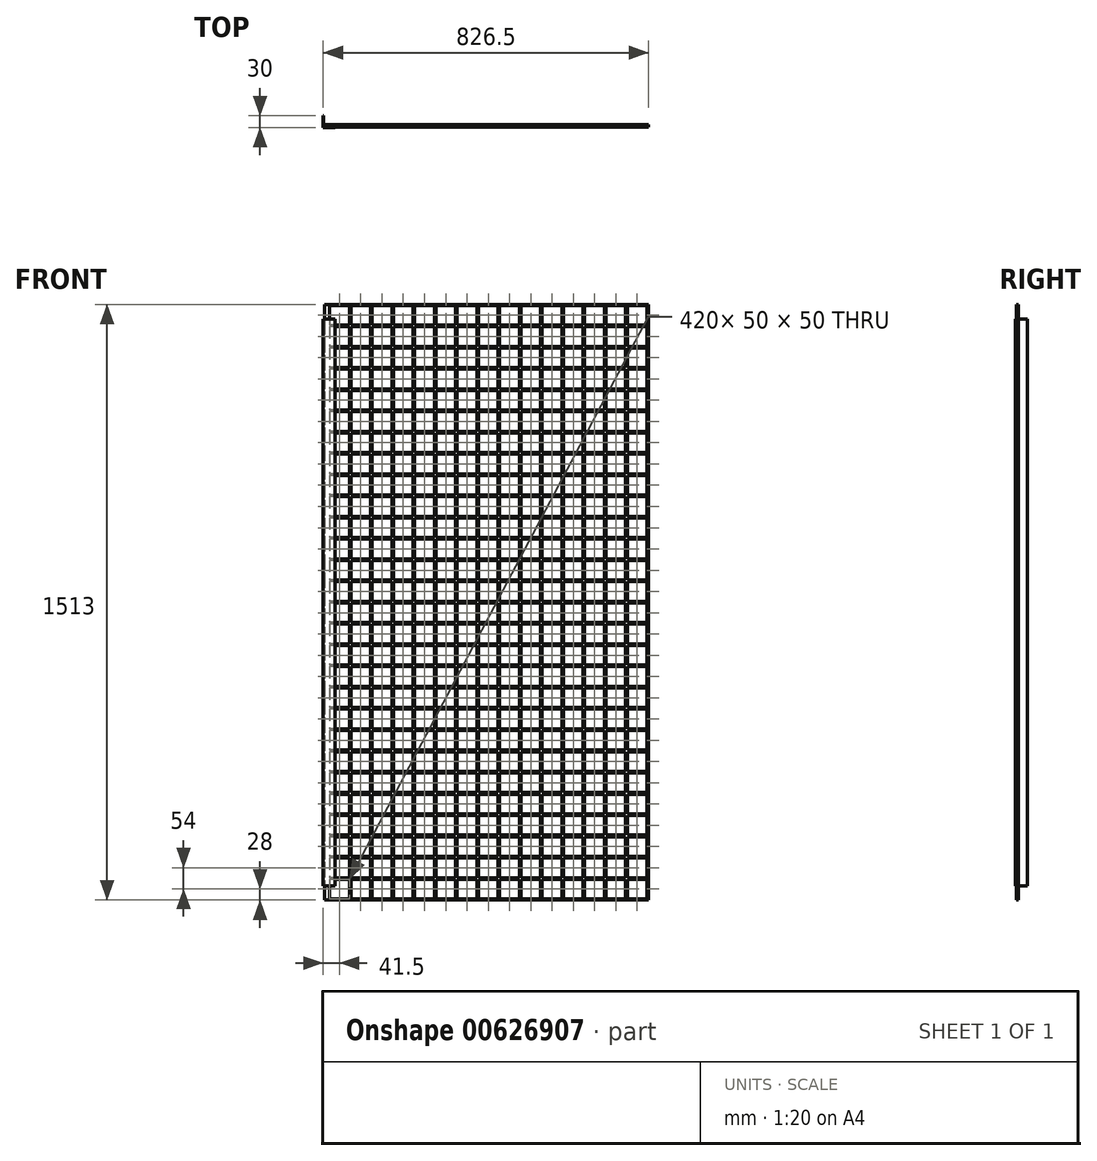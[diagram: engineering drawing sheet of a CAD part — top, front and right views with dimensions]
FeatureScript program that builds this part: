
annotation { "Feature Type Name" : "Feature", "Feature Type Description" : "" }
export const myFeature = defineFeature(function(context is Context, id is Id, definition is map)
    precondition{}
    {
        {
            var Q0;
            Q0=qCreatedBy(makeId("Front.planeOp"),FACE);
            var sketch = newSketch(context, id + "F0", { "sketchPlane" : qUnion([Q0])});
            skLineSegment(sketch, "E0.bottom", {"start": v(0, 0) * mm, "end": v(830, 0) * mm});
            skLineSegment(sketch, "E0.top", {"start": v(0, 1520) * mm, "end": v(830, 1520) * mm});
            skLineSegment(sketch, "E0.left", {"start": v(0, 0) * mm, "end": v(0, 1520) * mm});
            skLineSegment(sketch, "E0.right", {"start": v(830, 0) * mm, "end": v(830, 1520) * mm});
            skLineSegment(sketch, "E1.bottom", {"start": v(830, 1520) * mm, "end": v(800, 1520) * mm});
            skLineSegment(sketch, "E1.top", {"start": v(830, 0) * mm, "end": v(800, 0) * mm});
            skLineSegment(sketch, "E1.left", {"start": v(830, 1520) * mm, "end": v(830, 0) * mm});
            skLineSegment(sketch, "E1.right", {"start": v(800, 1520) * mm, "end": v(800, 0) * mm});
            skLineSegment(sketch, "E2.bottom", {"start": v(0, 1520) * mm, "end": v(800, 1520) * mm});
            skLineSegment(sketch, "E2.top", {"start": v(0, 1490) * mm, "end": v(800, 1490) * mm});
            skLineSegment(sketch, "E2.left", {"start": v(0, 1520) * mm, "end": v(0, 1490) * mm});
            skLineSegment(sketch, "E2.right", {"start": v(800, 1520) * mm, "end": v(800, 1490) * mm});
            skLineSegment(sketch, "E3.bottom", {"start": v(800, 0) * mm, "end": v(0, 0) * mm});
            skLineSegment(sketch, "E3.top", {"start": v(800, 30) * mm, "end": v(0, 30) * mm});
            skLineSegment(sketch, "E3.left", {"start": v(800, 0) * mm, "end": v(800, 30) * mm});
            skLineSegment(sketch, "E3.right", {"start": v(0, 0) * mm, "end": v(0, 30) * mm});
            skLineSegment(sketch, "E4.bottom", {"start": v(0, 1480) * mm, "end": v(30, 1480) * mm});
            skLineSegment(sketch, "E4.top", {"start": v(0, 40) * mm, "end": v(30, 40) * mm});
            skLineSegment(sketch, "E4.left", {"start": v(0, 1480) * mm, "end": v(0, 40) * mm});
            skLineSegment(sketch, "E4.right", {"start": v(30, 1480) * mm, "end": v(30, 40) * mm});
            skSolve(sketch);
        }
        {
            var Q0;
            Q0=makeQuery(id+"F0.imprint","IMPRINT",FACE,{"disambiguationData":[TD([[makeQuery(id+"F0.imprint","IMPRINT",EDGE,{"derivedFrom":sQuery(id+"F0.wireOp",EDGE,"E2.bottom")}),-1.0]])]});
            var Q1;
            Q1=makeQuery(id+"F0.imprint","IMPRINT",FACE,{"disambiguationData":[TD([[makeQuery(id+"F0.imprint","IMPRINT",EDGE,{"derivedFrom":sQuery(id+"F0.wireOp",EDGE,"E1.bottom")}),1.0]])]});
            var Q2;
            Q2=makeQuery(id+"F0.imprint","IMPRINT",FACE,{"disambiguationData":[TD([[makeQuery(id+"F0.imprint","IMPRINT",EDGE,{"derivedFrom":sQuery(id+"F0.wireOp",EDGE,"E3.bottom")}),-1.0]])]});
            var Q3;
            Q3=makeQuery(id+"F0.imprint","IMPRINT",FACE,{"disambiguationData":[TD([[makeQuery(id+"F0.imprint","IMPRINT",EDGE,{"derivedFrom":sQuery(id+"F0.wireOp",EDGE,"E4.bottom")}),-1.0]])]});
            extrude(context, id + "F1", {"entities" : qUnion([Q0, Q1, Q2, Q3]), "depth" : 30 * mm, "offsetDistance" : 25 * mm});
        }
        {
            var Q0;
            Q0=makeQuery(id+"F1.opExtrude","SWEPT_FACE",FACE,{"disambiguationData":[OSD([sQuery(id+"F0.wireOp",EDGE,"E2.top")])]});
            var Q1;
            Q1=makeQuery(id+"F1.opExtrude","SWEPT_FACE",FACE,{"disambiguationData":[OSD([sQuery(id+"F0.wireOp",EDGE,"E1.right")])]});
            var Q2;
            Q2=makeQuery(id+"F1.opExtrude","SWEPT_FACE",FACE,{"disambiguationData":[OSD([sQuery(id+"F0.wireOp",EDGE,"E3.top")])]});
            var Q3;
            Q3=makeQuery(id+"F1.opExtrude","SWEPT_FACE",FACE,{"disambiguationData":[OSD([sQuery(id+"F0.wireOp",EDGE,"E2.left")])]});
            var Q4;
            Q4=makeQuery(id+"F1.opExtrude","SWEPT_FACE",FACE,{"disambiguationData":[OSD([sQuery(id+"F0.wireOp",EDGE,"E3.right")])]});
            var Q5;
            Q5=makeQuery(id+"F1.opExtrude","SWEPT_FACE",FACE,{"disambiguationData":[OSD([sQuery(id+"F0.wireOp",EDGE,"E4.right")])]});
            var Q6;
            Q6=makeQuery(id+"F1.opExtrude","SWEPT_FACE",FACE,{"disambiguationData":[OSD([sQuery(id+"F0.wireOp",EDGE,"E4.bottom")])]});
            var Q7;
            Q7=makeQuery(id+"F1.opExtrude","SWEPT_FACE",FACE,{"disambiguationData":[OSD([sQuery(id+"F0.wireOp",EDGE,"E4.top")])]});
            var Q8;
            Q8=makeQuery(id+"F1.opExtrude","CAP_FACE",FACE,{"disambiguationData":[OSD([sQuery(id+"F0.wireOp",EDGE,"E4.bottom"),sQuery(id+"F0.wireOp",EDGE,"E4.top"),sQuery(id+"F0.wireOp",EDGE,"E4.left"),sQuery(id+"F0.wireOp",EDGE,"E4.right")])],"isStart":true});
            shell(context, id + "F2", {"entities" : qUnion([Q0, Q1, Q2, Q3, Q4, Q5, Q6, Q7, Q8]), "thickness" : 1.5 * mm});
        }
        {
            var Q0;
            Q0=makeQuery(id+"F2.opShell","OFFSET_FACE",FACE,{"disambiguationData":[OSD([sQuery(id+"F0.wireOp",EDGE,"E4.bottom"),sQuery(id+"F0.wireOp",EDGE,"E4.top"),sQuery(id+"F0.wireOp",EDGE,"E4.left"),sQuery(id+"F0.wireOp",EDGE,"E4.right")])]});
            var sketch = newSketch(context, id + "F3", { "sketchPlane" : qUnion([Q0])});
            skLineSegment(sketch, "E5.bottom", {"start": v(-3.5, 1516.5) * mm, "end": v(-826.5, 1516.5) * mm});
            skLineSegment(sketch, "E5.top", {"start": v(-3.5, 3.5) * mm, "end": v(-826.5, 3.5) * mm});
            skLineSegment(sketch, "E5.left", {"start": v(-3.5, 1516.5) * mm, "end": v(-3.5, 3.5) * mm});
            skLineSegment(sketch, "E5.right", {"start": v(-826.5, 1516.5) * mm, "end": v(-826.5, 3.5) * mm});
            skLineSegment(sketch, "E6.bottom", {"start": v(-822.5, 1514.5) * mm, "end": v(-772.5, 1514.5) * mm});
            skLineSegment(sketch, "E6.top", {"start": v(-822.5, 1464.5) * mm, "end": v(-772.5, 1464.5) * mm});
            skLineSegment(sketch, "E6.left", {"start": v(-822.5, 1514.5) * mm, "end": v(-822.5, 1464.5) * mm});
            skLineSegment(sketch, "E6.right", {"start": v(-772.5, 1514.5) * mm, "end": v(-772.5, 1464.5) * mm});
            skLineSegment(sketch, "E7.0.1.0", {"start": v(-772.5, 1460.5) * mm, "end": v(-772.5, 1410.5) * mm});
            skLineSegment(sketch, "E7.0.1.1", {"start": v(-822.5, 1460.5) * mm, "end": v(-772.5, 1460.5) * mm});
            skLineSegment(sketch, "E7.0.1.2", {"start": v(-822.5, 1460.5) * mm, "end": v(-822.5, 1410.5) * mm});
            skLineSegment(sketch, "E7.0.1.3", {"start": v(-822.5, 1410.5) * mm, "end": v(-772.5, 1410.5) * mm});
            skLineSegment(sketch, "E7.0.2.0", {"start": v(-772.5, 1406.5) * mm, "end": v(-772.5, 1356.5) * mm});
            skLineSegment(sketch, "E7.0.2.1", {"start": v(-822.5, 1406.5) * mm, "end": v(-772.5, 1406.5) * mm});
            skLineSegment(sketch, "E7.0.2.2", {"start": v(-822.5, 1406.5) * mm, "end": v(-822.5, 1356.5) * mm});
            skLineSegment(sketch, "E7.0.2.3", {"start": v(-822.5, 1356.5) * mm, "end": v(-772.5, 1356.5) * mm});
            skLineSegment(sketch, "E7.0.3.0", {"start": v(-772.5, 1352.5) * mm, "end": v(-772.5, 1302.5) * mm});
            skLineSegment(sketch, "E7.0.3.1", {"start": v(-822.5, 1352.5) * mm, "end": v(-772.5, 1352.5) * mm});
            skLineSegment(sketch, "E7.0.3.2", {"start": v(-822.5, 1352.5) * mm, "end": v(-822.5, 1302.5) * mm});
            skLineSegment(sketch, "E7.0.3.3", {"start": v(-822.5, 1302.5) * mm, "end": v(-772.5, 1302.5) * mm});
            skLineSegment(sketch, "E7.0.4.0", {"start": v(-772.5, 1298.5) * mm, "end": v(-772.5, 1248.5) * mm});
            skLineSegment(sketch, "E7.0.4.1", {"start": v(-822.5, 1298.5) * mm, "end": v(-772.5, 1298.5) * mm});
            skLineSegment(sketch, "E7.0.4.2", {"start": v(-822.5, 1298.5) * mm, "end": v(-822.5, 1248.5) * mm});
            skLineSegment(sketch, "E7.0.4.3", {"start": v(-822.5, 1248.5) * mm, "end": v(-772.5, 1248.5) * mm});
            skLineSegment(sketch, "E7.0.5.0", {"start": v(-772.5, 1244.5) * mm, "end": v(-772.5, 1194.5) * mm});
            skLineSegment(sketch, "E7.0.5.1", {"start": v(-822.5, 1244.5) * mm, "end": v(-772.5, 1244.5) * mm});
            skLineSegment(sketch, "E7.0.5.2", {"start": v(-822.5, 1244.5) * mm, "end": v(-822.5, 1194.5) * mm});
            skLineSegment(sketch, "E7.0.5.3", {"start": v(-822.5, 1194.5) * mm, "end": v(-772.5, 1194.5) * mm});
            skLineSegment(sketch, "E7.0.6.0", {"start": v(-772.5, 1190.5) * mm, "end": v(-772.5, 1140.5) * mm});
            skLineSegment(sketch, "E7.0.6.1", {"start": v(-822.5, 1190.5) * mm, "end": v(-772.5, 1190.5) * mm});
            skLineSegment(sketch, "E7.0.6.2", {"start": v(-822.5, 1190.5) * mm, "end": v(-822.5, 1140.5) * mm});
            skLineSegment(sketch, "E7.0.6.3", {"start": v(-822.5, 1140.5) * mm, "end": v(-772.5, 1140.5) * mm});
            skLineSegment(sketch, "E7.0.7.0", {"start": v(-772.5, 1136.5) * mm, "end": v(-772.5, 1086.5) * mm});
            skLineSegment(sketch, "E7.0.7.1", {"start": v(-822.5, 1136.5) * mm, "end": v(-772.5, 1136.5) * mm});
            skLineSegment(sketch, "E7.0.7.2", {"start": v(-822.5, 1136.5) * mm, "end": v(-822.5, 1086.5) * mm});
            skLineSegment(sketch, "E7.0.7.3", {"start": v(-822.5, 1086.5) * mm, "end": v(-772.5, 1086.5) * mm});
            skLineSegment(sketch, "E7.0.8.0", {"start": v(-772.5, 1082.5) * mm, "end": v(-772.5, 1032.5) * mm});
            skLineSegment(sketch, "E7.0.8.1", {"start": v(-822.5, 1082.5) * mm, "end": v(-772.5, 1082.5) * mm});
            skLineSegment(sketch, "E7.0.8.2", {"start": v(-822.5, 1082.5) * mm, "end": v(-822.5, 1032.5) * mm});
            skLineSegment(sketch, "E7.0.8.3", {"start": v(-822.5, 1032.5) * mm, "end": v(-772.5, 1032.5) * mm});
            skLineSegment(sketch, "E7.0.9.0", {"start": v(-772.5, 1028.5) * mm, "end": v(-772.5, 978.5) * mm});
            skLineSegment(sketch, "E7.0.9.1", {"start": v(-822.5, 1028.5) * mm, "end": v(-772.5, 1028.5) * mm});
            skLineSegment(sketch, "E7.0.9.2", {"start": v(-822.5, 1028.5) * mm, "end": v(-822.5, 978.5) * mm});
            skLineSegment(sketch, "E7.0.9.3", {"start": v(-822.5, 978.5) * mm, "end": v(-772.5, 978.5) * mm});
            skLineSegment(sketch, "E7.0.10.0", {"start": v(-772.5, 974.5) * mm, "end": v(-772.5, 924.5) * mm});
            skLineSegment(sketch, "E7.0.10.1", {"start": v(-822.5, 974.5) * mm, "end": v(-772.5, 974.5) * mm});
            skLineSegment(sketch, "E7.0.10.2", {"start": v(-822.5, 974.5) * mm, "end": v(-822.5, 924.5) * mm});
            skLineSegment(sketch, "E7.0.10.3", {"start": v(-822.5, 924.5) * mm, "end": v(-772.5, 924.5) * mm});
            skLineSegment(sketch, "E7.0.11.0", {"start": v(-772.5, 920.5) * mm, "end": v(-772.5, 870.5) * mm});
            skLineSegment(sketch, "E7.0.11.1", {"start": v(-822.5, 920.5) * mm, "end": v(-772.5, 920.5) * mm});
            skLineSegment(sketch, "E7.0.11.2", {"start": v(-822.5, 920.5) * mm, "end": v(-822.5, 870.5) * mm});
            skLineSegment(sketch, "E7.0.11.3", {"start": v(-822.5, 870.5) * mm, "end": v(-772.5, 870.5) * mm});
            skLineSegment(sketch, "E7.0.12.0", {"start": v(-772.5, 866.5) * mm, "end": v(-772.5, 816.5) * mm});
            skLineSegment(sketch, "E7.0.12.1", {"start": v(-822.5, 866.5) * mm, "end": v(-772.5, 866.5) * mm});
            skLineSegment(sketch, "E7.0.12.2", {"start": v(-822.5, 866.5) * mm, "end": v(-822.5, 816.5) * mm});
            skLineSegment(sketch, "E7.0.12.3", {"start": v(-822.5, 816.5) * mm, "end": v(-772.5, 816.5) * mm});
            skLineSegment(sketch, "E7.0.13.0", {"start": v(-772.5, 812.5) * mm, "end": v(-772.5, 762.5) * mm});
            skLineSegment(sketch, "E7.0.13.1", {"start": v(-822.5, 812.5) * mm, "end": v(-772.5, 812.5) * mm});
            skLineSegment(sketch, "E7.0.13.2", {"start": v(-822.5, 812.5) * mm, "end": v(-822.5, 762.5) * mm});
            skLineSegment(sketch, "E7.0.13.3", {"start": v(-822.5, 762.5) * mm, "end": v(-772.5, 762.5) * mm});
            skLineSegment(sketch, "E7.0.14.0", {"start": v(-772.5, 758.5) * mm, "end": v(-772.5, 708.5) * mm});
            skLineSegment(sketch, "E7.0.14.1", {"start": v(-822.5, 758.5) * mm, "end": v(-772.5, 758.5) * mm});
            skLineSegment(sketch, "E7.0.14.2", {"start": v(-822.5, 758.5) * mm, "end": v(-822.5, 708.5) * mm});
            skLineSegment(sketch, "E7.0.14.3", {"start": v(-822.5, 708.5) * mm, "end": v(-772.5, 708.5) * mm});
            skLineSegment(sketch, "E7.0.15.0", {"start": v(-772.5, 704.5) * mm, "end": v(-772.5, 654.5) * mm});
            skLineSegment(sketch, "E7.0.15.1", {"start": v(-822.5, 704.5) * mm, "end": v(-772.5, 704.5) * mm});
            skLineSegment(sketch, "E7.0.15.2", {"start": v(-822.5, 704.5) * mm, "end": v(-822.5, 654.5) * mm});
            skLineSegment(sketch, "E7.0.15.3", {"start": v(-822.5, 654.5) * mm, "end": v(-772.5, 654.5) * mm});
            skLineSegment(sketch, "E7.0.16.0", {"start": v(-772.5, 650.5) * mm, "end": v(-772.5, 600.5) * mm});
            skLineSegment(sketch, "E7.0.16.1", {"start": v(-822.5, 650.5) * mm, "end": v(-772.5, 650.5) * mm});
            skLineSegment(sketch, "E7.0.16.2", {"start": v(-822.5, 650.5) * mm, "end": v(-822.5, 600.5) * mm});
            skLineSegment(sketch, "E7.0.16.3", {"start": v(-822.5, 600.5) * mm, "end": v(-772.5, 600.5) * mm});
            skLineSegment(sketch, "E7.0.17.0", {"start": v(-772.5, 596.5) * mm, "end": v(-772.5, 546.5) * mm});
            skLineSegment(sketch, "E7.0.17.1", {"start": v(-822.5, 596.5) * mm, "end": v(-772.5, 596.5) * mm});
            skLineSegment(sketch, "E7.0.17.2", {"start": v(-822.5, 596.5) * mm, "end": v(-822.5, 546.5) * mm});
            skLineSegment(sketch, "E7.0.17.3", {"start": v(-822.5, 546.5) * mm, "end": v(-772.5, 546.5) * mm});
            skLineSegment(sketch, "E7.0.18.0", {"start": v(-772.5, 542.5) * mm, "end": v(-772.5, 492.5) * mm});
            skLineSegment(sketch, "E7.0.18.1", {"start": v(-822.5, 542.5) * mm, "end": v(-772.5, 542.5) * mm});
            skLineSegment(sketch, "E7.0.18.2", {"start": v(-822.5, 542.5) * mm, "end": v(-822.5, 492.5) * mm});
            skLineSegment(sketch, "E7.0.18.3", {"start": v(-822.5, 492.5) * mm, "end": v(-772.5, 492.5) * mm});
            skLineSegment(sketch, "E7.0.19.0", {"start": v(-772.5, 488.5) * mm, "end": v(-772.5, 438.5) * mm});
            skLineSegment(sketch, "E7.0.19.1", {"start": v(-822.5, 488.5) * mm, "end": v(-772.5, 488.5) * mm});
            skLineSegment(sketch, "E7.0.19.2", {"start": v(-822.5, 488.5) * mm, "end": v(-822.5, 438.5) * mm});
            skLineSegment(sketch, "E7.0.19.3", {"start": v(-822.5, 438.5) * mm, "end": v(-772.5, 438.5) * mm});
            skLineSegment(sketch, "E7.0.20.0", {"start": v(-772.5, 434.5) * mm, "end": v(-772.5, 384.5) * mm});
            skLineSegment(sketch, "E7.0.20.1", {"start": v(-822.5, 434.5) * mm, "end": v(-772.5, 434.5) * mm});
            skLineSegment(sketch, "E7.0.20.2", {"start": v(-822.5, 434.5) * mm, "end": v(-822.5, 384.5) * mm});
            skLineSegment(sketch, "E7.0.20.3", {"start": v(-822.5, 384.5) * mm, "end": v(-772.5, 384.5) * mm});
            skLineSegment(sketch, "E7.0.21.0", {"start": v(-772.5, 380.5) * mm, "end": v(-772.5, 330.5) * mm});
            skLineSegment(sketch, "E7.0.21.1", {"start": v(-822.5, 380.5) * mm, "end": v(-772.5, 380.5) * mm});
            skLineSegment(sketch, "E7.0.21.2", {"start": v(-822.5, 380.5) * mm, "end": v(-822.5, 330.5) * mm});
            skLineSegment(sketch, "E7.0.21.3", {"start": v(-822.5, 330.5) * mm, "end": v(-772.5, 330.5) * mm});
            skLineSegment(sketch, "E7.0.22.0", {"start": v(-772.5, 326.5) * mm, "end": v(-772.5, 276.5) * mm});
            skLineSegment(sketch, "E7.0.22.1", {"start": v(-822.5, 326.5) * mm, "end": v(-772.5, 326.5) * mm});
            skLineSegment(sketch, "E7.0.22.2", {"start": v(-822.5, 326.5) * mm, "end": v(-822.5, 276.5) * mm});
            skLineSegment(sketch, "E7.0.22.3", {"start": v(-822.5, 276.5) * mm, "end": v(-772.5, 276.5) * mm});
            skLineSegment(sketch, "E7.0.23.0", {"start": v(-772.5, 272.5) * mm, "end": v(-772.5, 222.5) * mm});
            skLineSegment(sketch, "E7.0.23.1", {"start": v(-822.5, 272.5) * mm, "end": v(-772.5, 272.5) * mm});
            skLineSegment(sketch, "E7.0.23.2", {"start": v(-822.5, 272.5) * mm, "end": v(-822.5, 222.5) * mm});
            skLineSegment(sketch, "E7.0.23.3", {"start": v(-822.5, 222.5) * mm, "end": v(-772.5, 222.5) * mm});
            skLineSegment(sketch, "E7.0.24.0", {"start": v(-772.5, 218.5) * mm, "end": v(-772.5, 168.5) * mm});
            skLineSegment(sketch, "E7.0.24.1", {"start": v(-822.5, 218.5) * mm, "end": v(-772.5, 218.5) * mm});
            skLineSegment(sketch, "E7.0.24.2", {"start": v(-822.5, 218.5) * mm, "end": v(-822.5, 168.5) * mm});
            skLineSegment(sketch, "E7.0.24.3", {"start": v(-822.5, 168.5) * mm, "end": v(-772.5, 168.5) * mm});
            skLineSegment(sketch, "E7.0.25.0", {"start": v(-772.5, 164.5) * mm, "end": v(-772.5, 114.5) * mm});
            skLineSegment(sketch, "E7.0.25.1", {"start": v(-822.5, 164.5) * mm, "end": v(-772.5, 164.5) * mm});
            skLineSegment(sketch, "E7.0.25.2", {"start": v(-822.5, 164.5) * mm, "end": v(-822.5, 114.5) * mm});
            skLineSegment(sketch, "E7.0.25.3", {"start": v(-822.5, 114.5) * mm, "end": v(-772.5, 114.5) * mm});
            skLineSegment(sketch, "E7.0.26.0", {"start": v(-772.5, 110.5) * mm, "end": v(-772.5, 60.5) * mm});
            skLineSegment(sketch, "E7.0.26.1", {"start": v(-822.5, 110.5) * mm, "end": v(-772.5, 110.5) * mm});
            skLineSegment(sketch, "E7.0.26.2", {"start": v(-822.5, 110.5) * mm, "end": v(-822.5, 60.5) * mm});
            skLineSegment(sketch, "E7.0.26.3", {"start": v(-822.5, 60.5) * mm, "end": v(-772.5, 60.5) * mm});
            skLineSegment(sketch, "E7.0.27.0", {"start": v(-772.5, 56.5) * mm, "end": v(-772.5, 6.5) * mm});
            skLineSegment(sketch, "E7.0.27.1", {"start": v(-822.5, 56.5) * mm, "end": v(-772.5, 56.5) * mm});
            skLineSegment(sketch, "E7.0.27.2", {"start": v(-822.5, 56.5) * mm, "end": v(-822.5, 6.5) * mm});
            skLineSegment(sketch, "E7.0.27.3", {"start": v(-822.5, 6.5) * mm, "end": v(-772.5, 6.5) * mm});
            skLineSegment(sketch, "E7.1.0.0", {"start": v(-718.5, 1514.5) * mm, "end": v(-718.5, 1464.5) * mm});
            skLineSegment(sketch, "E7.1.0.1", {"start": v(-768.5, 1514.5) * mm, "end": v(-718.5, 1514.5) * mm});
            skLineSegment(sketch, "E7.1.0.2", {"start": v(-768.5, 1514.5) * mm, "end": v(-768.5, 1464.5) * mm});
            skLineSegment(sketch, "E7.1.0.3", {"start": v(-768.5, 1464.5) * mm, "end": v(-718.5, 1464.5) * mm});
            skLineSegment(sketch, "E7.1.1.0", {"start": v(-718.5, 1460.5) * mm, "end": v(-718.5, 1410.5) * mm});
            skLineSegment(sketch, "E7.1.1.1", {"start": v(-768.5, 1460.5) * mm, "end": v(-718.5, 1460.5) * mm});
            skLineSegment(sketch, "E7.1.1.2", {"start": v(-768.5, 1460.5) * mm, "end": v(-768.5, 1410.5) * mm});
            skLineSegment(sketch, "E7.1.1.3", {"start": v(-768.5, 1410.5) * mm, "end": v(-718.5, 1410.5) * mm});
            skLineSegment(sketch, "E7.1.2.0", {"start": v(-718.5, 1406.5) * mm, "end": v(-718.5, 1356.5) * mm});
            skLineSegment(sketch, "E7.1.2.1", {"start": v(-768.5, 1406.5) * mm, "end": v(-718.5, 1406.5) * mm});
            skLineSegment(sketch, "E7.1.2.2", {"start": v(-768.5, 1406.5) * mm, "end": v(-768.5, 1356.5) * mm});
            skLineSegment(sketch, "E7.1.2.3", {"start": v(-768.5, 1356.5) * mm, "end": v(-718.5, 1356.5) * mm});
            skLineSegment(sketch, "E7.1.3.0", {"start": v(-718.5, 1352.5) * mm, "end": v(-718.5, 1302.5) * mm});
            skLineSegment(sketch, "E7.1.3.1", {"start": v(-768.5, 1352.5) * mm, "end": v(-718.5, 1352.5) * mm});
            skLineSegment(sketch, "E7.1.3.2", {"start": v(-768.5, 1352.5) * mm, "end": v(-768.5, 1302.5) * mm});
            skLineSegment(sketch, "E7.1.3.3", {"start": v(-768.5, 1302.5) * mm, "end": v(-718.5, 1302.5) * mm});
            skLineSegment(sketch, "E7.1.4.0", {"start": v(-718.5, 1298.5) * mm, "end": v(-718.5, 1248.5) * mm});
            skLineSegment(sketch, "E7.1.4.1", {"start": v(-768.5, 1298.5) * mm, "end": v(-718.5, 1298.5) * mm});
            skLineSegment(sketch, "E7.1.4.2", {"start": v(-768.5, 1298.5) * mm, "end": v(-768.5, 1248.5) * mm});
            skLineSegment(sketch, "E7.1.4.3", {"start": v(-768.5, 1248.5) * mm, "end": v(-718.5, 1248.5) * mm});
            skLineSegment(sketch, "E7.1.5.0", {"start": v(-718.5, 1244.5) * mm, "end": v(-718.5, 1194.5) * mm});
            skLineSegment(sketch, "E7.1.5.1", {"start": v(-768.5, 1244.5) * mm, "end": v(-718.5, 1244.5) * mm});
            skLineSegment(sketch, "E7.1.5.2", {"start": v(-768.5, 1244.5) * mm, "end": v(-768.5, 1194.5) * mm});
            skLineSegment(sketch, "E7.1.5.3", {"start": v(-768.5, 1194.5) * mm, "end": v(-718.5, 1194.5) * mm});
            skLineSegment(sketch, "E7.1.6.0", {"start": v(-718.5, 1190.5) * mm, "end": v(-718.5, 1140.5) * mm});
            skLineSegment(sketch, "E7.1.6.1", {"start": v(-768.5, 1190.5) * mm, "end": v(-718.5, 1190.5) * mm});
            skLineSegment(sketch, "E7.1.6.2", {"start": v(-768.5, 1190.5) * mm, "end": v(-768.5, 1140.5) * mm});
            skLineSegment(sketch, "E7.1.6.3", {"start": v(-768.5, 1140.5) * mm, "end": v(-718.5, 1140.5) * mm});
            skLineSegment(sketch, "E7.1.7.0", {"start": v(-718.5, 1136.5) * mm, "end": v(-718.5, 1086.5) * mm});
            skLineSegment(sketch, "E7.1.7.1", {"start": v(-768.5, 1136.5) * mm, "end": v(-718.5, 1136.5) * mm});
            skLineSegment(sketch, "E7.1.7.2", {"start": v(-768.5, 1136.5) * mm, "end": v(-768.5, 1086.5) * mm});
            skLineSegment(sketch, "E7.1.7.3", {"start": v(-768.5, 1086.5) * mm, "end": v(-718.5, 1086.5) * mm});
            skLineSegment(sketch, "E7.1.8.0", {"start": v(-718.5, 1082.5) * mm, "end": v(-718.5, 1032.5) * mm});
            skLineSegment(sketch, "E7.1.8.1", {"start": v(-768.5, 1082.5) * mm, "end": v(-718.5, 1082.5) * mm});
            skLineSegment(sketch, "E7.1.8.2", {"start": v(-768.5, 1082.5) * mm, "end": v(-768.5, 1032.5) * mm});
            skLineSegment(sketch, "E7.1.8.3", {"start": v(-768.5, 1032.5) * mm, "end": v(-718.5, 1032.5) * mm});
            skLineSegment(sketch, "E7.1.9.0", {"start": v(-718.5, 1028.5) * mm, "end": v(-718.5, 978.5) * mm});
            skLineSegment(sketch, "E7.1.9.1", {"start": v(-768.5, 1028.5) * mm, "end": v(-718.5, 1028.5) * mm});
            skLineSegment(sketch, "E7.1.9.2", {"start": v(-768.5, 1028.5) * mm, "end": v(-768.5, 978.5) * mm});
            skLineSegment(sketch, "E7.1.9.3", {"start": v(-768.5, 978.5) * mm, "end": v(-718.5, 978.5) * mm});
            skLineSegment(sketch, "E7.1.10.0", {"start": v(-718.5, 974.5) * mm, "end": v(-718.5, 924.5) * mm});
            skLineSegment(sketch, "E7.1.10.1", {"start": v(-768.5, 974.5) * mm, "end": v(-718.5, 974.5) * mm});
            skLineSegment(sketch, "E7.1.10.2", {"start": v(-768.5, 974.5) * mm, "end": v(-768.5, 924.5) * mm});
            skLineSegment(sketch, "E7.1.10.3", {"start": v(-768.5, 924.5) * mm, "end": v(-718.5, 924.5) * mm});
            skLineSegment(sketch, "E7.1.11.0", {"start": v(-718.5, 920.5) * mm, "end": v(-718.5, 870.5) * mm});
            skLineSegment(sketch, "E7.1.11.1", {"start": v(-768.5, 920.5) * mm, "end": v(-718.5, 920.5) * mm});
            skLineSegment(sketch, "E7.1.11.2", {"start": v(-768.5, 920.5) * mm, "end": v(-768.5, 870.5) * mm});
            skLineSegment(sketch, "E7.1.11.3", {"start": v(-768.5, 870.5) * mm, "end": v(-718.5, 870.5) * mm});
            skLineSegment(sketch, "E7.1.12.0", {"start": v(-718.5, 866.5) * mm, "end": v(-718.5, 816.5) * mm});
            skLineSegment(sketch, "E7.1.12.1", {"start": v(-768.5, 866.5) * mm, "end": v(-718.5, 866.5) * mm});
            skLineSegment(sketch, "E7.1.12.2", {"start": v(-768.5, 866.5) * mm, "end": v(-768.5, 816.5) * mm});
            skLineSegment(sketch, "E7.1.12.3", {"start": v(-768.5, 816.5) * mm, "end": v(-718.5, 816.5) * mm});
            skLineSegment(sketch, "E7.1.13.0", {"start": v(-718.5, 812.5) * mm, "end": v(-718.5, 762.5) * mm});
            skLineSegment(sketch, "E7.1.13.1", {"start": v(-768.5, 812.5) * mm, "end": v(-718.5, 812.5) * mm});
            skLineSegment(sketch, "E7.1.13.2", {"start": v(-768.5, 812.5) * mm, "end": v(-768.5, 762.5) * mm});
            skLineSegment(sketch, "E7.1.13.3", {"start": v(-768.5, 762.5) * mm, "end": v(-718.5, 762.5) * mm});
            skLineSegment(sketch, "E7.1.14.0", {"start": v(-718.5, 758.5) * mm, "end": v(-718.5, 708.5) * mm});
            skLineSegment(sketch, "E7.1.14.1", {"start": v(-768.5, 758.5) * mm, "end": v(-718.5, 758.5) * mm});
            skLineSegment(sketch, "E7.1.14.2", {"start": v(-768.5, 758.5) * mm, "end": v(-768.5, 708.5) * mm});
            skLineSegment(sketch, "E7.1.14.3", {"start": v(-768.5, 708.5) * mm, "end": v(-718.5, 708.5) * mm});
            skLineSegment(sketch, "E7.1.15.0", {"start": v(-718.5, 704.5) * mm, "end": v(-718.5, 654.5) * mm});
            skLineSegment(sketch, "E7.1.15.1", {"start": v(-768.5, 704.5) * mm, "end": v(-718.5, 704.5) * mm});
            skLineSegment(sketch, "E7.1.15.2", {"start": v(-768.5, 704.5) * mm, "end": v(-768.5, 654.5) * mm});
            skLineSegment(sketch, "E7.1.15.3", {"start": v(-768.5, 654.5) * mm, "end": v(-718.5, 654.5) * mm});
            skLineSegment(sketch, "E7.1.16.0", {"start": v(-718.5, 650.5) * mm, "end": v(-718.5, 600.5) * mm});
            skLineSegment(sketch, "E7.1.16.1", {"start": v(-768.5, 650.5) * mm, "end": v(-718.5, 650.5) * mm});
            skLineSegment(sketch, "E7.1.16.2", {"start": v(-768.5, 650.5) * mm, "end": v(-768.5, 600.5) * mm});
            skLineSegment(sketch, "E7.1.16.3", {"start": v(-768.5, 600.5) * mm, "end": v(-718.5, 600.5) * mm});
            skLineSegment(sketch, "E7.1.17.0", {"start": v(-718.5, 596.5) * mm, "end": v(-718.5, 546.5) * mm});
            skLineSegment(sketch, "E7.1.17.1", {"start": v(-768.5, 596.5) * mm, "end": v(-718.5, 596.5) * mm});
            skLineSegment(sketch, "E7.1.17.2", {"start": v(-768.5, 596.5) * mm, "end": v(-768.5, 546.5) * mm});
            skLineSegment(sketch, "E7.1.17.3", {"start": v(-768.5, 546.5) * mm, "end": v(-718.5, 546.5) * mm});
            skLineSegment(sketch, "E7.1.18.0", {"start": v(-718.5, 542.5) * mm, "end": v(-718.5, 492.5) * mm});
            skLineSegment(sketch, "E7.1.18.1", {"start": v(-768.5, 542.5) * mm, "end": v(-718.5, 542.5) * mm});
            skLineSegment(sketch, "E7.1.18.2", {"start": v(-768.5, 542.5) * mm, "end": v(-768.5, 492.5) * mm});
            skLineSegment(sketch, "E7.1.18.3", {"start": v(-768.5, 492.5) * mm, "end": v(-718.5, 492.5) * mm});
            skLineSegment(sketch, "E7.1.19.0", {"start": v(-718.5, 488.5) * mm, "end": v(-718.5, 438.5) * mm});
            skLineSegment(sketch, "E7.1.19.1", {"start": v(-768.5, 488.5) * mm, "end": v(-718.5, 488.5) * mm});
            skLineSegment(sketch, "E7.1.19.2", {"start": v(-768.5, 488.5) * mm, "end": v(-768.5, 438.5) * mm});
            skLineSegment(sketch, "E7.1.19.3", {"start": v(-768.5, 438.5) * mm, "end": v(-718.5, 438.5) * mm});
            skLineSegment(sketch, "E7.1.20.0", {"start": v(-718.5, 434.5) * mm, "end": v(-718.5, 384.5) * mm});
            skLineSegment(sketch, "E7.1.20.1", {"start": v(-768.5, 434.5) * mm, "end": v(-718.5, 434.5) * mm});
            skLineSegment(sketch, "E7.1.20.2", {"start": v(-768.5, 434.5) * mm, "end": v(-768.5, 384.5) * mm});
            skLineSegment(sketch, "E7.1.20.3", {"start": v(-768.5, 384.5) * mm, "end": v(-718.5, 384.5) * mm});
            skLineSegment(sketch, "E7.1.21.0", {"start": v(-718.5, 380.5) * mm, "end": v(-718.5, 330.5) * mm});
            skLineSegment(sketch, "E7.1.21.1", {"start": v(-768.5, 380.5) * mm, "end": v(-718.5, 380.5) * mm});
            skLineSegment(sketch, "E7.1.21.2", {"start": v(-768.5, 380.5) * mm, "end": v(-768.5, 330.5) * mm});
            skLineSegment(sketch, "E7.1.21.3", {"start": v(-768.5, 330.5) * mm, "end": v(-718.5, 330.5) * mm});
            skLineSegment(sketch, "E7.1.22.0", {"start": v(-718.5, 326.5) * mm, "end": v(-718.5, 276.5) * mm});
            skLineSegment(sketch, "E7.1.22.1", {"start": v(-768.5, 326.5) * mm, "end": v(-718.5, 326.5) * mm});
            skLineSegment(sketch, "E7.1.22.2", {"start": v(-768.5, 326.5) * mm, "end": v(-768.5, 276.5) * mm});
            skLineSegment(sketch, "E7.1.22.3", {"start": v(-768.5, 276.5) * mm, "end": v(-718.5, 276.5) * mm});
            skLineSegment(sketch, "E7.1.23.0", {"start": v(-718.5, 272.5) * mm, "end": v(-718.5, 222.5) * mm});
            skLineSegment(sketch, "E7.1.23.1", {"start": v(-768.5, 272.5) * mm, "end": v(-718.5, 272.5) * mm});
            skLineSegment(sketch, "E7.1.23.2", {"start": v(-768.5, 272.5) * mm, "end": v(-768.5, 222.5) * mm});
            skLineSegment(sketch, "E7.1.23.3", {"start": v(-768.5, 222.5) * mm, "end": v(-718.5, 222.5) * mm});
            skLineSegment(sketch, "E7.1.24.0", {"start": v(-718.5, 218.5) * mm, "end": v(-718.5, 168.5) * mm});
            skLineSegment(sketch, "E7.1.24.1", {"start": v(-768.5, 218.5) * mm, "end": v(-718.5, 218.5) * mm});
            skLineSegment(sketch, "E7.1.24.2", {"start": v(-768.5, 218.5) * mm, "end": v(-768.5, 168.5) * mm});
            skLineSegment(sketch, "E7.1.24.3", {"start": v(-768.5, 168.5) * mm, "end": v(-718.5, 168.5) * mm});
            skLineSegment(sketch, "E7.1.25.0", {"start": v(-718.5, 164.5) * mm, "end": v(-718.5, 114.5) * mm});
            skLineSegment(sketch, "E7.1.25.1", {"start": v(-768.5, 164.5) * mm, "end": v(-718.5, 164.5) * mm});
            skLineSegment(sketch, "E7.1.25.2", {"start": v(-768.5, 164.5) * mm, "end": v(-768.5, 114.5) * mm});
            skLineSegment(sketch, "E7.1.25.3", {"start": v(-768.5, 114.5) * mm, "end": v(-718.5, 114.5) * mm});
            skLineSegment(sketch, "E7.1.26.0", {"start": v(-718.5, 110.5) * mm, "end": v(-718.5, 60.5) * mm});
            skLineSegment(sketch, "E7.1.26.1", {"start": v(-768.5, 110.5) * mm, "end": v(-718.5, 110.5) * mm});
            skLineSegment(sketch, "E7.1.26.2", {"start": v(-768.5, 110.5) * mm, "end": v(-768.5, 60.5) * mm});
            skLineSegment(sketch, "E7.1.26.3", {"start": v(-768.5, 60.5) * mm, "end": v(-718.5, 60.5) * mm});
            skLineSegment(sketch, "E7.1.27.0", {"start": v(-718.5, 56.5) * mm, "end": v(-718.5, 6.5) * mm});
            skLineSegment(sketch, "E7.1.27.1", {"start": v(-768.5, 56.5) * mm, "end": v(-718.5, 56.5) * mm});
            skLineSegment(sketch, "E7.1.27.2", {"start": v(-768.5, 56.5) * mm, "end": v(-768.5, 6.5) * mm});
            skLineSegment(sketch, "E7.1.27.3", {"start": v(-768.5, 6.5) * mm, "end": v(-718.5, 6.5) * mm});
            skLineSegment(sketch, "E7.2.0.0", {"start": v(-664.5, 1514.5) * mm, "end": v(-664.5, 1464.5) * mm});
            skLineSegment(sketch, "E7.2.0.1", {"start": v(-714.5, 1514.5) * mm, "end": v(-664.5, 1514.5) * mm});
            skLineSegment(sketch, "E7.2.0.2", {"start": v(-714.5, 1514.5) * mm, "end": v(-714.5, 1464.5) * mm});
            skLineSegment(sketch, "E7.2.0.3", {"start": v(-714.5, 1464.5) * mm, "end": v(-664.5, 1464.5) * mm});
            skLineSegment(sketch, "E7.2.1.0", {"start": v(-664.5, 1460.5) * mm, "end": v(-664.5, 1410.5) * mm});
            skLineSegment(sketch, "E7.2.1.1", {"start": v(-714.5, 1460.5) * mm, "end": v(-664.5, 1460.5) * mm});
            skLineSegment(sketch, "E7.2.1.2", {"start": v(-714.5, 1460.5) * mm, "end": v(-714.5, 1410.5) * mm});
            skLineSegment(sketch, "E7.2.1.3", {"start": v(-714.5, 1410.5) * mm, "end": v(-664.5, 1410.5) * mm});
            skLineSegment(sketch, "E7.2.2.0", {"start": v(-664.5, 1406.5) * mm, "end": v(-664.5, 1356.5) * mm});
            skLineSegment(sketch, "E7.2.2.1", {"start": v(-714.5, 1406.5) * mm, "end": v(-664.5, 1406.5) * mm});
            skLineSegment(sketch, "E7.2.2.2", {"start": v(-714.5, 1406.5) * mm, "end": v(-714.5, 1356.5) * mm});
            skLineSegment(sketch, "E7.2.2.3", {"start": v(-714.5, 1356.5) * mm, "end": v(-664.5, 1356.5) * mm});
            skLineSegment(sketch, "E7.2.3.0", {"start": v(-664.5, 1352.5) * mm, "end": v(-664.5, 1302.5) * mm});
            skLineSegment(sketch, "E7.2.3.1", {"start": v(-714.5, 1352.5) * mm, "end": v(-664.5, 1352.5) * mm});
            skLineSegment(sketch, "E7.2.3.2", {"start": v(-714.5, 1352.5) * mm, "end": v(-714.5, 1302.5) * mm});
            skLineSegment(sketch, "E7.2.3.3", {"start": v(-714.5, 1302.5) * mm, "end": v(-664.5, 1302.5) * mm});
            skLineSegment(sketch, "E7.2.4.0", {"start": v(-664.5, 1298.5) * mm, "end": v(-664.5, 1248.5) * mm});
            skLineSegment(sketch, "E7.2.4.1", {"start": v(-714.5, 1298.5) * mm, "end": v(-664.5, 1298.5) * mm});
            skLineSegment(sketch, "E7.2.4.2", {"start": v(-714.5, 1298.5) * mm, "end": v(-714.5, 1248.5) * mm});
            skLineSegment(sketch, "E7.2.4.3", {"start": v(-714.5, 1248.5) * mm, "end": v(-664.5, 1248.5) * mm});
            skLineSegment(sketch, "E7.2.5.0", {"start": v(-664.5, 1244.5) * mm, "end": v(-664.5, 1194.5) * mm});
            skLineSegment(sketch, "E7.2.5.1", {"start": v(-714.5, 1244.5) * mm, "end": v(-664.5, 1244.5) * mm});
            skLineSegment(sketch, "E7.2.5.2", {"start": v(-714.5, 1244.5) * mm, "end": v(-714.5, 1194.5) * mm});
            skLineSegment(sketch, "E7.2.5.3", {"start": v(-714.5, 1194.5) * mm, "end": v(-664.5, 1194.5) * mm});
            skLineSegment(sketch, "E7.2.6.0", {"start": v(-664.5, 1190.5) * mm, "end": v(-664.5, 1140.5) * mm});
            skLineSegment(sketch, "E7.2.6.1", {"start": v(-714.5, 1190.5) * mm, "end": v(-664.5, 1190.5) * mm});
            skLineSegment(sketch, "E7.2.6.2", {"start": v(-714.5, 1190.5) * mm, "end": v(-714.5, 1140.5) * mm});
            skLineSegment(sketch, "E7.2.6.3", {"start": v(-714.5, 1140.5) * mm, "end": v(-664.5, 1140.5) * mm});
            skLineSegment(sketch, "E7.2.7.0", {"start": v(-664.5, 1136.5) * mm, "end": v(-664.5, 1086.5) * mm});
            skLineSegment(sketch, "E7.2.7.1", {"start": v(-714.5, 1136.5) * mm, "end": v(-664.5, 1136.5) * mm});
            skLineSegment(sketch, "E7.2.7.2", {"start": v(-714.5, 1136.5) * mm, "end": v(-714.5, 1086.5) * mm});
            skLineSegment(sketch, "E7.2.7.3", {"start": v(-714.5, 1086.5) * mm, "end": v(-664.5, 1086.5) * mm});
            skLineSegment(sketch, "E7.2.8.0", {"start": v(-664.5, 1082.5) * mm, "end": v(-664.5, 1032.5) * mm});
            skLineSegment(sketch, "E7.2.8.1", {"start": v(-714.5, 1082.5) * mm, "end": v(-664.5, 1082.5) * mm});
            skLineSegment(sketch, "E7.2.8.2", {"start": v(-714.5, 1082.5) * mm, "end": v(-714.5, 1032.5) * mm});
            skLineSegment(sketch, "E7.2.8.3", {"start": v(-714.5, 1032.5) * mm, "end": v(-664.5, 1032.5) * mm});
            skLineSegment(sketch, "E7.2.9.0", {"start": v(-664.5, 1028.5) * mm, "end": v(-664.5, 978.5) * mm});
            skLineSegment(sketch, "E7.2.9.1", {"start": v(-714.5, 1028.5) * mm, "end": v(-664.5, 1028.5) * mm});
            skLineSegment(sketch, "E7.2.9.2", {"start": v(-714.5, 1028.5) * mm, "end": v(-714.5, 978.5) * mm});
            skLineSegment(sketch, "E7.2.9.3", {"start": v(-714.5, 978.5) * mm, "end": v(-664.5, 978.5) * mm});
            skLineSegment(sketch, "E7.2.10.0", {"start": v(-664.5, 974.5) * mm, "end": v(-664.5, 924.5) * mm});
            skLineSegment(sketch, "E7.2.10.1", {"start": v(-714.5, 974.5) * mm, "end": v(-664.5, 974.5) * mm});
            skLineSegment(sketch, "E7.2.10.2", {"start": v(-714.5, 974.5) * mm, "end": v(-714.5, 924.5) * mm});
            skLineSegment(sketch, "E7.2.10.3", {"start": v(-714.5, 924.5) * mm, "end": v(-664.5, 924.5) * mm});
            skLineSegment(sketch, "E7.2.11.0", {"start": v(-664.5, 920.5) * mm, "end": v(-664.5, 870.5) * mm});
            skLineSegment(sketch, "E7.2.11.1", {"start": v(-714.5, 920.5) * mm, "end": v(-664.5, 920.5) * mm});
            skLineSegment(sketch, "E7.2.11.2", {"start": v(-714.5, 920.5) * mm, "end": v(-714.5, 870.5) * mm});
            skLineSegment(sketch, "E7.2.11.3", {"start": v(-714.5, 870.5) * mm, "end": v(-664.5, 870.5) * mm});
            skLineSegment(sketch, "E7.2.12.0", {"start": v(-664.5, 866.5) * mm, "end": v(-664.5, 816.5) * mm});
            skLineSegment(sketch, "E7.2.12.1", {"start": v(-714.5, 866.5) * mm, "end": v(-664.5, 866.5) * mm});
            skLineSegment(sketch, "E7.2.12.2", {"start": v(-714.5, 866.5) * mm, "end": v(-714.5, 816.5) * mm});
            skLineSegment(sketch, "E7.2.12.3", {"start": v(-714.5, 816.5) * mm, "end": v(-664.5, 816.5) * mm});
            skLineSegment(sketch, "E7.2.13.0", {"start": v(-664.5, 812.5) * mm, "end": v(-664.5, 762.5) * mm});
            skLineSegment(sketch, "E7.2.13.1", {"start": v(-714.5, 812.5) * mm, "end": v(-664.5, 812.5) * mm});
            skLineSegment(sketch, "E7.2.13.2", {"start": v(-714.5, 812.5) * mm, "end": v(-714.5, 762.5) * mm});
            skLineSegment(sketch, "E7.2.13.3", {"start": v(-714.5, 762.5) * mm, "end": v(-664.5, 762.5) * mm});
            skLineSegment(sketch, "E7.2.14.0", {"start": v(-664.5, 758.5) * mm, "end": v(-664.5, 708.5) * mm});
            skLineSegment(sketch, "E7.2.14.1", {"start": v(-714.5, 758.5) * mm, "end": v(-664.5, 758.5) * mm});
            skLineSegment(sketch, "E7.2.14.2", {"start": v(-714.5, 758.5) * mm, "end": v(-714.5, 708.5) * mm});
            skLineSegment(sketch, "E7.2.14.3", {"start": v(-714.5, 708.5) * mm, "end": v(-664.5, 708.5) * mm});
            skLineSegment(sketch, "E7.2.15.0", {"start": v(-664.5, 704.5) * mm, "end": v(-664.5, 654.5) * mm});
            skLineSegment(sketch, "E7.2.15.1", {"start": v(-714.5, 704.5) * mm, "end": v(-664.5, 704.5) * mm});
            skLineSegment(sketch, "E7.2.15.2", {"start": v(-714.5, 704.5) * mm, "end": v(-714.5, 654.5) * mm});
            skLineSegment(sketch, "E7.2.15.3", {"start": v(-714.5, 654.5) * mm, "end": v(-664.5, 654.5) * mm});
            skLineSegment(sketch, "E7.2.16.0", {"start": v(-664.5, 650.5) * mm, "end": v(-664.5, 600.5) * mm});
            skLineSegment(sketch, "E7.2.16.1", {"start": v(-714.5, 650.5) * mm, "end": v(-664.5, 650.5) * mm});
            skLineSegment(sketch, "E7.2.16.2", {"start": v(-714.5, 650.5) * mm, "end": v(-714.5, 600.5) * mm});
            skLineSegment(sketch, "E7.2.16.3", {"start": v(-714.5, 600.5) * mm, "end": v(-664.5, 600.5) * mm});
            skLineSegment(sketch, "E7.2.17.0", {"start": v(-664.5, 596.5) * mm, "end": v(-664.5, 546.5) * mm});
            skLineSegment(sketch, "E7.2.17.1", {"start": v(-714.5, 596.5) * mm, "end": v(-664.5, 596.5) * mm});
            skLineSegment(sketch, "E7.2.17.2", {"start": v(-714.5, 596.5) * mm, "end": v(-714.5, 546.5) * mm});
            skLineSegment(sketch, "E7.2.17.3", {"start": v(-714.5, 546.5) * mm, "end": v(-664.5, 546.5) * mm});
            skLineSegment(sketch, "E7.2.18.0", {"start": v(-664.5, 542.5) * mm, "end": v(-664.5, 492.5) * mm});
            skLineSegment(sketch, "E7.2.18.1", {"start": v(-714.5, 542.5) * mm, "end": v(-664.5, 542.5) * mm});
            skLineSegment(sketch, "E7.2.18.2", {"start": v(-714.5, 542.5) * mm, "end": v(-714.5, 492.5) * mm});
            skLineSegment(sketch, "E7.2.18.3", {"start": v(-714.5, 492.5) * mm, "end": v(-664.5, 492.5) * mm});
            skLineSegment(sketch, "E7.2.19.0", {"start": v(-664.5, 488.5) * mm, "end": v(-664.5, 438.5) * mm});
            skLineSegment(sketch, "E7.2.19.1", {"start": v(-714.5, 488.5) * mm, "end": v(-664.5, 488.5) * mm});
            skLineSegment(sketch, "E7.2.19.2", {"start": v(-714.5, 488.5) * mm, "end": v(-714.5, 438.5) * mm});
            skLineSegment(sketch, "E7.2.19.3", {"start": v(-714.5, 438.5) * mm, "end": v(-664.5, 438.5) * mm});
            skLineSegment(sketch, "E7.2.20.0", {"start": v(-664.5, 434.5) * mm, "end": v(-664.5, 384.5) * mm});
            skLineSegment(sketch, "E7.2.20.1", {"start": v(-714.5, 434.5) * mm, "end": v(-664.5, 434.5) * mm});
            skLineSegment(sketch, "E7.2.20.2", {"start": v(-714.5, 434.5) * mm, "end": v(-714.5, 384.5) * mm});
            skLineSegment(sketch, "E7.2.20.3", {"start": v(-714.5, 384.5) * mm, "end": v(-664.5, 384.5) * mm});
            skLineSegment(sketch, "E7.2.21.0", {"start": v(-664.5, 380.5) * mm, "end": v(-664.5, 330.5) * mm});
            skLineSegment(sketch, "E7.2.21.1", {"start": v(-714.5, 380.5) * mm, "end": v(-664.5, 380.5) * mm});
            skLineSegment(sketch, "E7.2.21.2", {"start": v(-714.5, 380.5) * mm, "end": v(-714.5, 330.5) * mm});
            skLineSegment(sketch, "E7.2.21.3", {"start": v(-714.5, 330.5) * mm, "end": v(-664.5, 330.5) * mm});
            skLineSegment(sketch, "E7.2.22.0", {"start": v(-664.5, 326.5) * mm, "end": v(-664.5, 276.5) * mm});
            skLineSegment(sketch, "E7.2.22.1", {"start": v(-714.5, 326.5) * mm, "end": v(-664.5, 326.5) * mm});
            skLineSegment(sketch, "E7.2.22.2", {"start": v(-714.5, 326.5) * mm, "end": v(-714.5, 276.5) * mm});
            skLineSegment(sketch, "E7.2.22.3", {"start": v(-714.5, 276.5) * mm, "end": v(-664.5, 276.5) * mm});
            skLineSegment(sketch, "E7.2.23.0", {"start": v(-664.5, 272.5) * mm, "end": v(-664.5, 222.5) * mm});
            skLineSegment(sketch, "E7.2.23.1", {"start": v(-714.5, 272.5) * mm, "end": v(-664.5, 272.5) * mm});
            skLineSegment(sketch, "E7.2.23.2", {"start": v(-714.5, 272.5) * mm, "end": v(-714.5, 222.5) * mm});
            skLineSegment(sketch, "E7.2.23.3", {"start": v(-714.5, 222.5) * mm, "end": v(-664.5, 222.5) * mm});
            skLineSegment(sketch, "E7.2.24.0", {"start": v(-664.5, 218.5) * mm, "end": v(-664.5, 168.5) * mm});
            skLineSegment(sketch, "E7.2.24.1", {"start": v(-714.5, 218.5) * mm, "end": v(-664.5, 218.5) * mm});
            skLineSegment(sketch, "E7.2.24.2", {"start": v(-714.5, 218.5) * mm, "end": v(-714.5, 168.5) * mm});
            skLineSegment(sketch, "E7.2.24.3", {"start": v(-714.5, 168.5) * mm, "end": v(-664.5, 168.5) * mm});
            skLineSegment(sketch, "E7.2.25.0", {"start": v(-664.5, 164.5) * mm, "end": v(-664.5, 114.5) * mm});
            skLineSegment(sketch, "E7.2.25.1", {"start": v(-714.5, 164.5) * mm, "end": v(-664.5, 164.5) * mm});
            skLineSegment(sketch, "E7.2.25.2", {"start": v(-714.5, 164.5) * mm, "end": v(-714.5, 114.5) * mm});
            skLineSegment(sketch, "E7.2.25.3", {"start": v(-714.5, 114.5) * mm, "end": v(-664.5, 114.5) * mm});
            skLineSegment(sketch, "E7.2.26.0", {"start": v(-664.5, 110.5) * mm, "end": v(-664.5, 60.5) * mm});
            skLineSegment(sketch, "E7.2.26.1", {"start": v(-714.5, 110.5) * mm, "end": v(-664.5, 110.5) * mm});
            skLineSegment(sketch, "E7.2.26.2", {"start": v(-714.5, 110.5) * mm, "end": v(-714.5, 60.5) * mm});
            skLineSegment(sketch, "E7.2.26.3", {"start": v(-714.5, 60.5) * mm, "end": v(-664.5, 60.5) * mm});
            skLineSegment(sketch, "E7.2.27.0", {"start": v(-664.5, 56.5) * mm, "end": v(-664.5, 6.5) * mm});
            skLineSegment(sketch, "E7.2.27.1", {"start": v(-714.5, 56.5) * mm, "end": v(-664.5, 56.5) * mm});
            skLineSegment(sketch, "E7.2.27.2", {"start": v(-714.5, 56.5) * mm, "end": v(-714.5, 6.5) * mm});
            skLineSegment(sketch, "E7.2.27.3", {"start": v(-714.5, 6.5) * mm, "end": v(-664.5, 6.5) * mm});
            skLineSegment(sketch, "E7.3.0.0", {"start": v(-610.5, 1514.5) * mm, "end": v(-610.5, 1464.5) * mm});
            skLineSegment(sketch, "E7.3.0.1", {"start": v(-660.5, 1514.5) * mm, "end": v(-610.5, 1514.5) * mm});
            skLineSegment(sketch, "E7.3.0.2", {"start": v(-660.5, 1514.5) * mm, "end": v(-660.5, 1464.5) * mm});
            skLineSegment(sketch, "E7.3.0.3", {"start": v(-660.5, 1464.5) * mm, "end": v(-610.5, 1464.5) * mm});
            skLineSegment(sketch, "E7.3.1.0", {"start": v(-610.5, 1460.5) * mm, "end": v(-610.5, 1410.5) * mm});
            skLineSegment(sketch, "E7.3.1.1", {"start": v(-660.5, 1460.5) * mm, "end": v(-610.5, 1460.5) * mm});
            skLineSegment(sketch, "E7.3.1.2", {"start": v(-660.5, 1460.5) * mm, "end": v(-660.5, 1410.5) * mm});
            skLineSegment(sketch, "E7.3.1.3", {"start": v(-660.5, 1410.5) * mm, "end": v(-610.5, 1410.5) * mm});
            skLineSegment(sketch, "E7.3.2.0", {"start": v(-610.5, 1406.5) * mm, "end": v(-610.5, 1356.5) * mm});
            skLineSegment(sketch, "E7.3.2.1", {"start": v(-660.5, 1406.5) * mm, "end": v(-610.5, 1406.5) * mm});
            skLineSegment(sketch, "E7.3.2.2", {"start": v(-660.5, 1406.5) * mm, "end": v(-660.5, 1356.5) * mm});
            skLineSegment(sketch, "E7.3.2.3", {"start": v(-660.5, 1356.5) * mm, "end": v(-610.5, 1356.5) * mm});
            skLineSegment(sketch, "E7.3.3.0", {"start": v(-610.5, 1352.5) * mm, "end": v(-610.5, 1302.5) * mm});
            skLineSegment(sketch, "E7.3.3.1", {"start": v(-660.5, 1352.5) * mm, "end": v(-610.5, 1352.5) * mm});
            skLineSegment(sketch, "E7.3.3.2", {"start": v(-660.5, 1352.5) * mm, "end": v(-660.5, 1302.5) * mm});
            skLineSegment(sketch, "E7.3.3.3", {"start": v(-660.5, 1302.5) * mm, "end": v(-610.5, 1302.5) * mm});
            skLineSegment(sketch, "E7.3.4.0", {"start": v(-610.5, 1298.5) * mm, "end": v(-610.5, 1248.5) * mm});
            skLineSegment(sketch, "E7.3.4.1", {"start": v(-660.5, 1298.5) * mm, "end": v(-610.5, 1298.5) * mm});
            skLineSegment(sketch, "E7.3.4.2", {"start": v(-660.5, 1298.5) * mm, "end": v(-660.5, 1248.5) * mm});
            skLineSegment(sketch, "E7.3.4.3", {"start": v(-660.5, 1248.5) * mm, "end": v(-610.5, 1248.5) * mm});
            skLineSegment(sketch, "E7.3.5.0", {"start": v(-610.5, 1244.5) * mm, "end": v(-610.5, 1194.5) * mm});
            skLineSegment(sketch, "E7.3.5.1", {"start": v(-660.5, 1244.5) * mm, "end": v(-610.5, 1244.5) * mm});
            skLineSegment(sketch, "E7.3.5.2", {"start": v(-660.5, 1244.5) * mm, "end": v(-660.5, 1194.5) * mm});
            skLineSegment(sketch, "E7.3.5.3", {"start": v(-660.5, 1194.5) * mm, "end": v(-610.5, 1194.5) * mm});
            skLineSegment(sketch, "E7.3.6.0", {"start": v(-610.5, 1190.5) * mm, "end": v(-610.5, 1140.5) * mm});
            skLineSegment(sketch, "E7.3.6.1", {"start": v(-660.5, 1190.5) * mm, "end": v(-610.5, 1190.5) * mm});
            skLineSegment(sketch, "E7.3.6.2", {"start": v(-660.5, 1190.5) * mm, "end": v(-660.5, 1140.5) * mm});
            skLineSegment(sketch, "E7.3.6.3", {"start": v(-660.5, 1140.5) * mm, "end": v(-610.5, 1140.5) * mm});
            skLineSegment(sketch, "E7.3.7.0", {"start": v(-610.5, 1136.5) * mm, "end": v(-610.5, 1086.5) * mm});
            skLineSegment(sketch, "E7.3.7.1", {"start": v(-660.5, 1136.5) * mm, "end": v(-610.5, 1136.5) * mm});
            skLineSegment(sketch, "E7.3.7.2", {"start": v(-660.5, 1136.5) * mm, "end": v(-660.5, 1086.5) * mm});
            skLineSegment(sketch, "E7.3.7.3", {"start": v(-660.5, 1086.5) * mm, "end": v(-610.5, 1086.5) * mm});
            skLineSegment(sketch, "E7.3.8.0", {"start": v(-610.5, 1082.5) * mm, "end": v(-610.5, 1032.5) * mm});
            skLineSegment(sketch, "E7.3.8.1", {"start": v(-660.5, 1082.5) * mm, "end": v(-610.5, 1082.5) * mm});
            skLineSegment(sketch, "E7.3.8.2", {"start": v(-660.5, 1082.5) * mm, "end": v(-660.5, 1032.5) * mm});
            skLineSegment(sketch, "E7.3.8.3", {"start": v(-660.5, 1032.5) * mm, "end": v(-610.5, 1032.5) * mm});
            skLineSegment(sketch, "E7.3.9.0", {"start": v(-610.5, 1028.5) * mm, "end": v(-610.5, 978.5) * mm});
            skLineSegment(sketch, "E7.3.9.1", {"start": v(-660.5, 1028.5) * mm, "end": v(-610.5, 1028.5) * mm});
            skLineSegment(sketch, "E7.3.9.2", {"start": v(-660.5, 1028.5) * mm, "end": v(-660.5, 978.5) * mm});
            skLineSegment(sketch, "E7.3.9.3", {"start": v(-660.5, 978.5) * mm, "end": v(-610.5, 978.5) * mm});
            skLineSegment(sketch, "E7.3.10.0", {"start": v(-610.5, 974.5) * mm, "end": v(-610.5, 924.5) * mm});
            skLineSegment(sketch, "E7.3.10.1", {"start": v(-660.5, 974.5) * mm, "end": v(-610.5, 974.5) * mm});
            skLineSegment(sketch, "E7.3.10.2", {"start": v(-660.5, 974.5) * mm, "end": v(-660.5, 924.5) * mm});
            skLineSegment(sketch, "E7.3.10.3", {"start": v(-660.5, 924.5) * mm, "end": v(-610.5, 924.5) * mm});
            skLineSegment(sketch, "E7.3.11.0", {"start": v(-610.5, 920.5) * mm, "end": v(-610.5, 870.5) * mm});
            skLineSegment(sketch, "E7.3.11.1", {"start": v(-660.5, 920.5) * mm, "end": v(-610.5, 920.5) * mm});
            skLineSegment(sketch, "E7.3.11.2", {"start": v(-660.5, 920.5) * mm, "end": v(-660.5, 870.5) * mm});
            skLineSegment(sketch, "E7.3.11.3", {"start": v(-660.5, 870.5) * mm, "end": v(-610.5, 870.5) * mm});
            skLineSegment(sketch, "E7.3.12.0", {"start": v(-610.5, 866.5) * mm, "end": v(-610.5, 816.5) * mm});
            skLineSegment(sketch, "E7.3.12.1", {"start": v(-660.5, 866.5) * mm, "end": v(-610.5, 866.5) * mm});
            skLineSegment(sketch, "E7.3.12.2", {"start": v(-660.5, 866.5) * mm, "end": v(-660.5, 816.5) * mm});
            skLineSegment(sketch, "E7.3.12.3", {"start": v(-660.5, 816.5) * mm, "end": v(-610.5, 816.5) * mm});
            skLineSegment(sketch, "E7.3.13.0", {"start": v(-610.5, 812.5) * mm, "end": v(-610.5, 762.5) * mm});
            skLineSegment(sketch, "E7.3.13.1", {"start": v(-660.5, 812.5) * mm, "end": v(-610.5, 812.5) * mm});
            skLineSegment(sketch, "E7.3.13.2", {"start": v(-660.5, 812.5) * mm, "end": v(-660.5, 762.5) * mm});
            skLineSegment(sketch, "E7.3.13.3", {"start": v(-660.5, 762.5) * mm, "end": v(-610.5, 762.5) * mm});
            skLineSegment(sketch, "E7.3.14.0", {"start": v(-610.5, 758.5) * mm, "end": v(-610.5, 708.5) * mm});
            skLineSegment(sketch, "E7.3.14.1", {"start": v(-660.5, 758.5) * mm, "end": v(-610.5, 758.5) * mm});
            skLineSegment(sketch, "E7.3.14.2", {"start": v(-660.5, 758.5) * mm, "end": v(-660.5, 708.5) * mm});
            skLineSegment(sketch, "E7.3.14.3", {"start": v(-660.5, 708.5) * mm, "end": v(-610.5, 708.5) * mm});
            skLineSegment(sketch, "E7.3.15.0", {"start": v(-610.5, 704.5) * mm, "end": v(-610.5, 654.5) * mm});
            skLineSegment(sketch, "E7.3.15.1", {"start": v(-660.5, 704.5) * mm, "end": v(-610.5, 704.5) * mm});
            skLineSegment(sketch, "E7.3.15.2", {"start": v(-660.5, 704.5) * mm, "end": v(-660.5, 654.5) * mm});
            skLineSegment(sketch, "E7.3.15.3", {"start": v(-660.5, 654.5) * mm, "end": v(-610.5, 654.5) * mm});
            skLineSegment(sketch, "E7.3.16.0", {"start": v(-610.5, 650.5) * mm, "end": v(-610.5, 600.5) * mm});
            skLineSegment(sketch, "E7.3.16.1", {"start": v(-660.5, 650.5) * mm, "end": v(-610.5, 650.5) * mm});
            skLineSegment(sketch, "E7.3.16.2", {"start": v(-660.5, 650.5) * mm, "end": v(-660.5, 600.5) * mm});
            skLineSegment(sketch, "E7.3.16.3", {"start": v(-660.5, 600.5) * mm, "end": v(-610.5, 600.5) * mm});
            skLineSegment(sketch, "E7.3.17.0", {"start": v(-610.5, 596.5) * mm, "end": v(-610.5, 546.5) * mm});
            skLineSegment(sketch, "E7.3.17.1", {"start": v(-660.5, 596.5) * mm, "end": v(-610.5, 596.5) * mm});
            skLineSegment(sketch, "E7.3.17.2", {"start": v(-660.5, 596.5) * mm, "end": v(-660.5, 546.5) * mm});
            skLineSegment(sketch, "E7.3.17.3", {"start": v(-660.5, 546.5) * mm, "end": v(-610.5, 546.5) * mm});
            skLineSegment(sketch, "E7.3.18.0", {"start": v(-610.5, 542.5) * mm, "end": v(-610.5, 492.5) * mm});
            skLineSegment(sketch, "E7.3.18.1", {"start": v(-660.5, 542.5) * mm, "end": v(-610.5, 542.5) * mm});
            skLineSegment(sketch, "E7.3.18.2", {"start": v(-660.5, 542.5) * mm, "end": v(-660.5, 492.5) * mm});
            skLineSegment(sketch, "E7.3.18.3", {"start": v(-660.5, 492.5) * mm, "end": v(-610.5, 492.5) * mm});
            skLineSegment(sketch, "E7.3.19.0", {"start": v(-610.5, 488.5) * mm, "end": v(-610.5, 438.5) * mm});
            skLineSegment(sketch, "E7.3.19.1", {"start": v(-660.5, 488.5) * mm, "end": v(-610.5, 488.5) * mm});
            skLineSegment(sketch, "E7.3.19.2", {"start": v(-660.5, 488.5) * mm, "end": v(-660.5, 438.5) * mm});
            skLineSegment(sketch, "E7.3.19.3", {"start": v(-660.5, 438.5) * mm, "end": v(-610.5, 438.5) * mm});
            skLineSegment(sketch, "E7.3.20.0", {"start": v(-610.5, 434.5) * mm, "end": v(-610.5, 384.5) * mm});
            skLineSegment(sketch, "E7.3.20.1", {"start": v(-660.5, 434.5) * mm, "end": v(-610.5, 434.5) * mm});
            skLineSegment(sketch, "E7.3.20.2", {"start": v(-660.5, 434.5) * mm, "end": v(-660.5, 384.5) * mm});
            skLineSegment(sketch, "E7.3.20.3", {"start": v(-660.5, 384.5) * mm, "end": v(-610.5, 384.5) * mm});
            skLineSegment(sketch, "E7.3.21.0", {"start": v(-610.5, 380.5) * mm, "end": v(-610.5, 330.5) * mm});
            skLineSegment(sketch, "E7.3.21.1", {"start": v(-660.5, 380.5) * mm, "end": v(-610.5, 380.5) * mm});
            skLineSegment(sketch, "E7.3.21.2", {"start": v(-660.5, 380.5) * mm, "end": v(-660.5, 330.5) * mm});
            skLineSegment(sketch, "E7.3.21.3", {"start": v(-660.5, 330.5) * mm, "end": v(-610.5, 330.5) * mm});
            skLineSegment(sketch, "E7.3.22.0", {"start": v(-610.5, 326.5) * mm, "end": v(-610.5, 276.5) * mm});
            skLineSegment(sketch, "E7.3.22.1", {"start": v(-660.5, 326.5) * mm, "end": v(-610.5, 326.5) * mm});
            skLineSegment(sketch, "E7.3.22.2", {"start": v(-660.5, 326.5) * mm, "end": v(-660.5, 276.5) * mm});
            skLineSegment(sketch, "E7.3.22.3", {"start": v(-660.5, 276.5) * mm, "end": v(-610.5, 276.5) * mm});
            skLineSegment(sketch, "E7.3.23.0", {"start": v(-610.5, 272.5) * mm, "end": v(-610.5, 222.5) * mm});
            skLineSegment(sketch, "E7.3.23.1", {"start": v(-660.5, 272.5) * mm, "end": v(-610.5, 272.5) * mm});
            skLineSegment(sketch, "E7.3.23.2", {"start": v(-660.5, 272.5) * mm, "end": v(-660.5, 222.5) * mm});
            skLineSegment(sketch, "E7.3.23.3", {"start": v(-660.5, 222.5) * mm, "end": v(-610.5, 222.5) * mm});
            skLineSegment(sketch, "E7.3.24.0", {"start": v(-610.5, 218.5) * mm, "end": v(-610.5, 168.5) * mm});
            skLineSegment(sketch, "E7.3.24.1", {"start": v(-660.5, 218.5) * mm, "end": v(-610.5, 218.5) * mm});
            skLineSegment(sketch, "E7.3.24.2", {"start": v(-660.5, 218.5) * mm, "end": v(-660.5, 168.5) * mm});
            skLineSegment(sketch, "E7.3.24.3", {"start": v(-660.5, 168.5) * mm, "end": v(-610.5, 168.5) * mm});
            skLineSegment(sketch, "E7.3.25.0", {"start": v(-610.5, 164.5) * mm, "end": v(-610.5, 114.5) * mm});
            skLineSegment(sketch, "E7.3.25.1", {"start": v(-660.5, 164.5) * mm, "end": v(-610.5, 164.5) * mm});
            skLineSegment(sketch, "E7.3.25.2", {"start": v(-660.5, 164.5) * mm, "end": v(-660.5, 114.5) * mm});
            skLineSegment(sketch, "E7.3.25.3", {"start": v(-660.5, 114.5) * mm, "end": v(-610.5, 114.5) * mm});
            skLineSegment(sketch, "E7.3.26.0", {"start": v(-610.5, 110.5) * mm, "end": v(-610.5, 60.5) * mm});
            skLineSegment(sketch, "E7.3.26.1", {"start": v(-660.5, 110.5) * mm, "end": v(-610.5, 110.5) * mm});
            skLineSegment(sketch, "E7.3.26.2", {"start": v(-660.5, 110.5) * mm, "end": v(-660.5, 60.5) * mm});
            skLineSegment(sketch, "E7.3.26.3", {"start": v(-660.5, 60.5) * mm, "end": v(-610.5, 60.5) * mm});
            skLineSegment(sketch, "E7.3.27.0", {"start": v(-610.5, 56.5) * mm, "end": v(-610.5, 6.5) * mm});
            skLineSegment(sketch, "E7.3.27.1", {"start": v(-660.5, 56.5) * mm, "end": v(-610.5, 56.5) * mm});
            skLineSegment(sketch, "E7.3.27.2", {"start": v(-660.5, 56.5) * mm, "end": v(-660.5, 6.5) * mm});
            skLineSegment(sketch, "E7.3.27.3", {"start": v(-660.5, 6.5) * mm, "end": v(-610.5, 6.5) * mm});
            skLineSegment(sketch, "E7.4.0.0", {"start": v(-556.5, 1514.5) * mm, "end": v(-556.5, 1464.5) * mm});
            skLineSegment(sketch, "E7.4.0.1", {"start": v(-606.5, 1514.5) * mm, "end": v(-556.5, 1514.5) * mm});
            skLineSegment(sketch, "E7.4.0.2", {"start": v(-606.5, 1514.5) * mm, "end": v(-606.5, 1464.5) * mm});
            skLineSegment(sketch, "E7.4.0.3", {"start": v(-606.5, 1464.5) * mm, "end": v(-556.5, 1464.5) * mm});
            skLineSegment(sketch, "E7.4.1.0", {"start": v(-556.5, 1460.5) * mm, "end": v(-556.5, 1410.5) * mm});
            skLineSegment(sketch, "E7.4.1.1", {"start": v(-606.5, 1460.5) * mm, "end": v(-556.5, 1460.5) * mm});
            skLineSegment(sketch, "E7.4.1.2", {"start": v(-606.5, 1460.5) * mm, "end": v(-606.5, 1410.5) * mm});
            skLineSegment(sketch, "E7.4.1.3", {"start": v(-606.5, 1410.5) * mm, "end": v(-556.5, 1410.5) * mm});
            skLineSegment(sketch, "E7.4.2.0", {"start": v(-556.5, 1406.5) * mm, "end": v(-556.5, 1356.5) * mm});
            skLineSegment(sketch, "E7.4.2.1", {"start": v(-606.5, 1406.5) * mm, "end": v(-556.5, 1406.5) * mm});
            skLineSegment(sketch, "E7.4.2.2", {"start": v(-606.5, 1406.5) * mm, "end": v(-606.5, 1356.5) * mm});
            skLineSegment(sketch, "E7.4.2.3", {"start": v(-606.5, 1356.5) * mm, "end": v(-556.5, 1356.5) * mm});
            skLineSegment(sketch, "E7.4.3.0", {"start": v(-556.5, 1352.5) * mm, "end": v(-556.5, 1302.5) * mm});
            skLineSegment(sketch, "E7.4.3.1", {"start": v(-606.5, 1352.5) * mm, "end": v(-556.5, 1352.5) * mm});
            skLineSegment(sketch, "E7.4.3.2", {"start": v(-606.5, 1352.5) * mm, "end": v(-606.5, 1302.5) * mm});
            skLineSegment(sketch, "E7.4.3.3", {"start": v(-606.5, 1302.5) * mm, "end": v(-556.5, 1302.5) * mm});
            skLineSegment(sketch, "E7.4.4.0", {"start": v(-556.5, 1298.5) * mm, "end": v(-556.5, 1248.5) * mm});
            skLineSegment(sketch, "E7.4.4.1", {"start": v(-606.5, 1298.5) * mm, "end": v(-556.5, 1298.5) * mm});
            skLineSegment(sketch, "E7.4.4.2", {"start": v(-606.5, 1298.5) * mm, "end": v(-606.5, 1248.5) * mm});
            skLineSegment(sketch, "E7.4.4.3", {"start": v(-606.5, 1248.5) * mm, "end": v(-556.5, 1248.5) * mm});
            skLineSegment(sketch, "E7.4.5.0", {"start": v(-556.5, 1244.5) * mm, "end": v(-556.5, 1194.5) * mm});
            skLineSegment(sketch, "E7.4.5.1", {"start": v(-606.5, 1244.5) * mm, "end": v(-556.5, 1244.5) * mm});
            skLineSegment(sketch, "E7.4.5.2", {"start": v(-606.5, 1244.5) * mm, "end": v(-606.5, 1194.5) * mm});
            skLineSegment(sketch, "E7.4.5.3", {"start": v(-606.5, 1194.5) * mm, "end": v(-556.5, 1194.5) * mm});
            skLineSegment(sketch, "E7.4.6.0", {"start": v(-556.5, 1190.5) * mm, "end": v(-556.5, 1140.5) * mm});
            skLineSegment(sketch, "E7.4.6.1", {"start": v(-606.5, 1190.5) * mm, "end": v(-556.5, 1190.5) * mm});
            skLineSegment(sketch, "E7.4.6.2", {"start": v(-606.5, 1190.5) * mm, "end": v(-606.5, 1140.5) * mm});
            skLineSegment(sketch, "E7.4.6.3", {"start": v(-606.5, 1140.5) * mm, "end": v(-556.5, 1140.5) * mm});
            skLineSegment(sketch, "E7.4.7.0", {"start": v(-556.5, 1136.5) * mm, "end": v(-556.5, 1086.5) * mm});
            skLineSegment(sketch, "E7.4.7.1", {"start": v(-606.5, 1136.5) * mm, "end": v(-556.5, 1136.5) * mm});
            skLineSegment(sketch, "E7.4.7.2", {"start": v(-606.5, 1136.5) * mm, "end": v(-606.5, 1086.5) * mm});
            skLineSegment(sketch, "E7.4.7.3", {"start": v(-606.5, 1086.5) * mm, "end": v(-556.5, 1086.5) * mm});
            skLineSegment(sketch, "E7.4.8.0", {"start": v(-556.5, 1082.5) * mm, "end": v(-556.5, 1032.5) * mm});
            skLineSegment(sketch, "E7.4.8.1", {"start": v(-606.5, 1082.5) * mm, "end": v(-556.5, 1082.5) * mm});
            skLineSegment(sketch, "E7.4.8.2", {"start": v(-606.5, 1082.5) * mm, "end": v(-606.5, 1032.5) * mm});
            skLineSegment(sketch, "E7.4.8.3", {"start": v(-606.5, 1032.5) * mm, "end": v(-556.5, 1032.5) * mm});
            skLineSegment(sketch, "E7.4.9.0", {"start": v(-556.5, 1028.5) * mm, "end": v(-556.5, 978.5) * mm});
            skLineSegment(sketch, "E7.4.9.1", {"start": v(-606.5, 1028.5) * mm, "end": v(-556.5, 1028.5) * mm});
            skLineSegment(sketch, "E7.4.9.2", {"start": v(-606.5, 1028.5) * mm, "end": v(-606.5, 978.5) * mm});
            skLineSegment(sketch, "E7.4.9.3", {"start": v(-606.5, 978.5) * mm, "end": v(-556.5, 978.5) * mm});
            skLineSegment(sketch, "E7.4.10.0", {"start": v(-556.5, 974.5) * mm, "end": v(-556.5, 924.5) * mm});
            skLineSegment(sketch, "E7.4.10.1", {"start": v(-606.5, 974.5) * mm, "end": v(-556.5, 974.5) * mm});
            skLineSegment(sketch, "E7.4.10.2", {"start": v(-606.5, 974.5) * mm, "end": v(-606.5, 924.5) * mm});
            skLineSegment(sketch, "E7.4.10.3", {"start": v(-606.5, 924.5) * mm, "end": v(-556.5, 924.5) * mm});
            skLineSegment(sketch, "E7.4.11.0", {"start": v(-556.5, 920.5) * mm, "end": v(-556.5, 870.5) * mm});
            skLineSegment(sketch, "E7.4.11.1", {"start": v(-606.5, 920.5) * mm, "end": v(-556.5, 920.5) * mm});
            skLineSegment(sketch, "E7.4.11.2", {"start": v(-606.5, 920.5) * mm, "end": v(-606.5, 870.5) * mm});
            skLineSegment(sketch, "E7.4.11.3", {"start": v(-606.5, 870.5) * mm, "end": v(-556.5, 870.5) * mm});
            skLineSegment(sketch, "E7.4.12.0", {"start": v(-556.5, 866.5) * mm, "end": v(-556.5, 816.5) * mm});
            skLineSegment(sketch, "E7.4.12.1", {"start": v(-606.5, 866.5) * mm, "end": v(-556.5, 866.5) * mm});
            skLineSegment(sketch, "E7.4.12.2", {"start": v(-606.5, 866.5) * mm, "end": v(-606.5, 816.5) * mm});
            skLineSegment(sketch, "E7.4.12.3", {"start": v(-606.5, 816.5) * mm, "end": v(-556.5, 816.5) * mm});
            skLineSegment(sketch, "E7.4.13.0", {"start": v(-556.5, 812.5) * mm, "end": v(-556.5, 762.5) * mm});
            skLineSegment(sketch, "E7.4.13.1", {"start": v(-606.5, 812.5) * mm, "end": v(-556.5, 812.5) * mm});
            skLineSegment(sketch, "E7.4.13.2", {"start": v(-606.5, 812.5) * mm, "end": v(-606.5, 762.5) * mm});
            skLineSegment(sketch, "E7.4.13.3", {"start": v(-606.5, 762.5) * mm, "end": v(-556.5, 762.5) * mm});
            skLineSegment(sketch, "E7.4.14.0", {"start": v(-556.5, 758.5) * mm, "end": v(-556.5, 708.5) * mm});
            skLineSegment(sketch, "E7.4.14.1", {"start": v(-606.5, 758.5) * mm, "end": v(-556.5, 758.5) * mm});
            skLineSegment(sketch, "E7.4.14.2", {"start": v(-606.5, 758.5) * mm, "end": v(-606.5, 708.5) * mm});
            skLineSegment(sketch, "E7.4.14.3", {"start": v(-606.5, 708.5) * mm, "end": v(-556.5, 708.5) * mm});
            skLineSegment(sketch, "E7.4.15.0", {"start": v(-556.5, 704.5) * mm, "end": v(-556.5, 654.5) * mm});
            skLineSegment(sketch, "E7.4.15.1", {"start": v(-606.5, 704.5) * mm, "end": v(-556.5, 704.5) * mm});
            skLineSegment(sketch, "E7.4.15.2", {"start": v(-606.5, 704.5) * mm, "end": v(-606.5, 654.5) * mm});
            skLineSegment(sketch, "E7.4.15.3", {"start": v(-606.5, 654.5) * mm, "end": v(-556.5, 654.5) * mm});
            skLineSegment(sketch, "E7.4.16.0", {"start": v(-556.5, 650.5) * mm, "end": v(-556.5, 600.5) * mm});
            skLineSegment(sketch, "E7.4.16.1", {"start": v(-606.5, 650.5) * mm, "end": v(-556.5, 650.5) * mm});
            skLineSegment(sketch, "E7.4.16.2", {"start": v(-606.5, 650.5) * mm, "end": v(-606.5, 600.5) * mm});
            skLineSegment(sketch, "E7.4.16.3", {"start": v(-606.5, 600.5) * mm, "end": v(-556.5, 600.5) * mm});
            skLineSegment(sketch, "E7.4.17.0", {"start": v(-556.5, 596.5) * mm, "end": v(-556.5, 546.5) * mm});
            skLineSegment(sketch, "E7.4.17.1", {"start": v(-606.5, 596.5) * mm, "end": v(-556.5, 596.5) * mm});
            skLineSegment(sketch, "E7.4.17.2", {"start": v(-606.5, 596.5) * mm, "end": v(-606.5, 546.5) * mm});
            skLineSegment(sketch, "E7.4.17.3", {"start": v(-606.5, 546.5) * mm, "end": v(-556.5, 546.5) * mm});
            skLineSegment(sketch, "E7.4.18.0", {"start": v(-556.5, 542.5) * mm, "end": v(-556.5, 492.5) * mm});
            skLineSegment(sketch, "E7.4.18.1", {"start": v(-606.5, 542.5) * mm, "end": v(-556.5, 542.5) * mm});
            skLineSegment(sketch, "E7.4.18.2", {"start": v(-606.5, 542.5) * mm, "end": v(-606.5, 492.5) * mm});
            skLineSegment(sketch, "E7.4.18.3", {"start": v(-606.5, 492.5) * mm, "end": v(-556.5, 492.5) * mm});
            skLineSegment(sketch, "E7.4.19.0", {"start": v(-556.5, 488.5) * mm, "end": v(-556.5, 438.5) * mm});
            skLineSegment(sketch, "E7.4.19.1", {"start": v(-606.5, 488.5) * mm, "end": v(-556.5, 488.5) * mm});
            skLineSegment(sketch, "E7.4.19.2", {"start": v(-606.5, 488.5) * mm, "end": v(-606.5, 438.5) * mm});
            skLineSegment(sketch, "E7.4.19.3", {"start": v(-606.5, 438.5) * mm, "end": v(-556.5, 438.5) * mm});
            skLineSegment(sketch, "E7.4.20.0", {"start": v(-556.5, 434.5) * mm, "end": v(-556.5, 384.5) * mm});
            skLineSegment(sketch, "E7.4.20.1", {"start": v(-606.5, 434.5) * mm, "end": v(-556.5, 434.5) * mm});
            skLineSegment(sketch, "E7.4.20.2", {"start": v(-606.5, 434.5) * mm, "end": v(-606.5, 384.5) * mm});
            skLineSegment(sketch, "E7.4.20.3", {"start": v(-606.5, 384.5) * mm, "end": v(-556.5, 384.5) * mm});
            skLineSegment(sketch, "E7.4.21.0", {"start": v(-556.5, 380.5) * mm, "end": v(-556.5, 330.5) * mm});
            skLineSegment(sketch, "E7.4.21.1", {"start": v(-606.5, 380.5) * mm, "end": v(-556.5, 380.5) * mm});
            skLineSegment(sketch, "E7.4.21.2", {"start": v(-606.5, 380.5) * mm, "end": v(-606.5, 330.5) * mm});
            skLineSegment(sketch, "E7.4.21.3", {"start": v(-606.5, 330.5) * mm, "end": v(-556.5, 330.5) * mm});
            skLineSegment(sketch, "E7.4.22.0", {"start": v(-556.5, 326.5) * mm, "end": v(-556.5, 276.5) * mm});
            skLineSegment(sketch, "E7.4.22.1", {"start": v(-606.5, 326.5) * mm, "end": v(-556.5, 326.5) * mm});
            skLineSegment(sketch, "E7.4.22.2", {"start": v(-606.5, 326.5) * mm, "end": v(-606.5, 276.5) * mm});
            skLineSegment(sketch, "E7.4.22.3", {"start": v(-606.5, 276.5) * mm, "end": v(-556.5, 276.5) * mm});
            skLineSegment(sketch, "E7.4.23.0", {"start": v(-556.5, 272.5) * mm, "end": v(-556.5, 222.5) * mm});
            skLineSegment(sketch, "E7.4.23.1", {"start": v(-606.5, 272.5) * mm, "end": v(-556.5, 272.5) * mm});
            skLineSegment(sketch, "E7.4.23.2", {"start": v(-606.5, 272.5) * mm, "end": v(-606.5, 222.5) * mm});
            skLineSegment(sketch, "E7.4.23.3", {"start": v(-606.5, 222.5) * mm, "end": v(-556.5, 222.5) * mm});
            skLineSegment(sketch, "E7.4.24.0", {"start": v(-556.5, 218.5) * mm, "end": v(-556.5, 168.5) * mm});
            skLineSegment(sketch, "E7.4.24.1", {"start": v(-606.5, 218.5) * mm, "end": v(-556.5, 218.5) * mm});
            skLineSegment(sketch, "E7.4.24.2", {"start": v(-606.5, 218.5) * mm, "end": v(-606.5, 168.5) * mm});
            skLineSegment(sketch, "E7.4.24.3", {"start": v(-606.5, 168.5) * mm, "end": v(-556.5, 168.5) * mm});
            skLineSegment(sketch, "E7.4.25.0", {"start": v(-556.5, 164.5) * mm, "end": v(-556.5, 114.5) * mm});
            skLineSegment(sketch, "E7.4.25.1", {"start": v(-606.5, 164.5) * mm, "end": v(-556.5, 164.5) * mm});
            skLineSegment(sketch, "E7.4.25.2", {"start": v(-606.5, 164.5) * mm, "end": v(-606.5, 114.5) * mm});
            skLineSegment(sketch, "E7.4.25.3", {"start": v(-606.5, 114.5) * mm, "end": v(-556.5, 114.5) * mm});
            skLineSegment(sketch, "E7.4.26.0", {"start": v(-556.5, 110.5) * mm, "end": v(-556.5, 60.5) * mm});
            skLineSegment(sketch, "E7.4.26.1", {"start": v(-606.5, 110.5) * mm, "end": v(-556.5, 110.5) * mm});
            skLineSegment(sketch, "E7.4.26.2", {"start": v(-606.5, 110.5) * mm, "end": v(-606.5, 60.5) * mm});
            skLineSegment(sketch, "E7.4.26.3", {"start": v(-606.5, 60.5) * mm, "end": v(-556.5, 60.5) * mm});
            skLineSegment(sketch, "E7.4.27.0", {"start": v(-556.5, 56.5) * mm, "end": v(-556.5, 6.5) * mm});
            skLineSegment(sketch, "E7.4.27.1", {"start": v(-606.5, 56.5) * mm, "end": v(-556.5, 56.5) * mm});
            skLineSegment(sketch, "E7.4.27.2", {"start": v(-606.5, 56.5) * mm, "end": v(-606.5, 6.5) * mm});
            skLineSegment(sketch, "E7.4.27.3", {"start": v(-606.5, 6.5) * mm, "end": v(-556.5, 6.5) * mm});
            skLineSegment(sketch, "E7.5.0.0", {"start": v(-502.5, 1514.5) * mm, "end": v(-502.5, 1464.5) * mm});
            skLineSegment(sketch, "E7.5.0.1", {"start": v(-552.5, 1514.5) * mm, "end": v(-502.5, 1514.5) * mm});
            skLineSegment(sketch, "E7.5.0.2", {"start": v(-552.5, 1514.5) * mm, "end": v(-552.5, 1464.5) * mm});
            skLineSegment(sketch, "E7.5.0.3", {"start": v(-552.5, 1464.5) * mm, "end": v(-502.5, 1464.5) * mm});
            skLineSegment(sketch, "E7.5.1.0", {"start": v(-502.5, 1460.5) * mm, "end": v(-502.5, 1410.5) * mm});
            skLineSegment(sketch, "E7.5.1.1", {"start": v(-552.5, 1460.5) * mm, "end": v(-502.5, 1460.5) * mm});
            skLineSegment(sketch, "E7.5.1.2", {"start": v(-552.5, 1460.5) * mm, "end": v(-552.5, 1410.5) * mm});
            skLineSegment(sketch, "E7.5.1.3", {"start": v(-552.5, 1410.5) * mm, "end": v(-502.5, 1410.5) * mm});
            skLineSegment(sketch, "E7.5.2.0", {"start": v(-502.5, 1406.5) * mm, "end": v(-502.5, 1356.5) * mm});
            skLineSegment(sketch, "E7.5.2.1", {"start": v(-552.5, 1406.5) * mm, "end": v(-502.5, 1406.5) * mm});
            skLineSegment(sketch, "E7.5.2.2", {"start": v(-552.5, 1406.5) * mm, "end": v(-552.5, 1356.5) * mm});
            skLineSegment(sketch, "E7.5.2.3", {"start": v(-552.5, 1356.5) * mm, "end": v(-502.5, 1356.5) * mm});
            skLineSegment(sketch, "E7.5.3.0", {"start": v(-502.5, 1352.5) * mm, "end": v(-502.5, 1302.5) * mm});
            skLineSegment(sketch, "E7.5.3.1", {"start": v(-552.5, 1352.5) * mm, "end": v(-502.5, 1352.5) * mm});
            skLineSegment(sketch, "E7.5.3.2", {"start": v(-552.5, 1352.5) * mm, "end": v(-552.5, 1302.5) * mm});
            skLineSegment(sketch, "E7.5.3.3", {"start": v(-552.5, 1302.5) * mm, "end": v(-502.5, 1302.5) * mm});
            skLineSegment(sketch, "E7.5.4.0", {"start": v(-502.5, 1298.5) * mm, "end": v(-502.5, 1248.5) * mm});
            skLineSegment(sketch, "E7.5.4.1", {"start": v(-552.5, 1298.5) * mm, "end": v(-502.5, 1298.5) * mm});
            skLineSegment(sketch, "E7.5.4.2", {"start": v(-552.5, 1298.5) * mm, "end": v(-552.5, 1248.5) * mm});
            skLineSegment(sketch, "E7.5.4.3", {"start": v(-552.5, 1248.5) * mm, "end": v(-502.5, 1248.5) * mm});
            skLineSegment(sketch, "E7.5.5.0", {"start": v(-502.5, 1244.5) * mm, "end": v(-502.5, 1194.5) * mm});
            skLineSegment(sketch, "E7.5.5.1", {"start": v(-552.5, 1244.5) * mm, "end": v(-502.5, 1244.5) * mm});
            skLineSegment(sketch, "E7.5.5.2", {"start": v(-552.5, 1244.5) * mm, "end": v(-552.5, 1194.5) * mm});
            skLineSegment(sketch, "E7.5.5.3", {"start": v(-552.5, 1194.5) * mm, "end": v(-502.5, 1194.5) * mm});
            skLineSegment(sketch, "E7.5.6.0", {"start": v(-502.5, 1190.5) * mm, "end": v(-502.5, 1140.5) * mm});
            skLineSegment(sketch, "E7.5.6.1", {"start": v(-552.5, 1190.5) * mm, "end": v(-502.5, 1190.5) * mm});
            skLineSegment(sketch, "E7.5.6.2", {"start": v(-552.5, 1190.5) * mm, "end": v(-552.5, 1140.5) * mm});
            skLineSegment(sketch, "E7.5.6.3", {"start": v(-552.5, 1140.5) * mm, "end": v(-502.5, 1140.5) * mm});
            skLineSegment(sketch, "E7.5.7.0", {"start": v(-502.5, 1136.5) * mm, "end": v(-502.5, 1086.5) * mm});
            skLineSegment(sketch, "E7.5.7.1", {"start": v(-552.5, 1136.5) * mm, "end": v(-502.5, 1136.5) * mm});
            skLineSegment(sketch, "E7.5.7.2", {"start": v(-552.5, 1136.5) * mm, "end": v(-552.5, 1086.5) * mm});
            skLineSegment(sketch, "E7.5.7.3", {"start": v(-552.5, 1086.5) * mm, "end": v(-502.5, 1086.5) * mm});
            skLineSegment(sketch, "E7.5.8.0", {"start": v(-502.5, 1082.5) * mm, "end": v(-502.5, 1032.5) * mm});
            skLineSegment(sketch, "E7.5.8.1", {"start": v(-552.5, 1082.5) * mm, "end": v(-502.5, 1082.5) * mm});
            skLineSegment(sketch, "E7.5.8.2", {"start": v(-552.5, 1082.5) * mm, "end": v(-552.5, 1032.5) * mm});
            skLineSegment(sketch, "E7.5.8.3", {"start": v(-552.5, 1032.5) * mm, "end": v(-502.5, 1032.5) * mm});
            skLineSegment(sketch, "E7.5.9.0", {"start": v(-502.5, 1028.5) * mm, "end": v(-502.5, 978.5) * mm});
            skLineSegment(sketch, "E7.5.9.1", {"start": v(-552.5, 1028.5) * mm, "end": v(-502.5, 1028.5) * mm});
            skLineSegment(sketch, "E7.5.9.2", {"start": v(-552.5, 1028.5) * mm, "end": v(-552.5, 978.5) * mm});
            skLineSegment(sketch, "E7.5.9.3", {"start": v(-552.5, 978.5) * mm, "end": v(-502.5, 978.5) * mm});
            skLineSegment(sketch, "E7.5.10.0", {"start": v(-502.5, 974.5) * mm, "end": v(-502.5, 924.5) * mm});
            skLineSegment(sketch, "E7.5.10.1", {"start": v(-552.5, 974.5) * mm, "end": v(-502.5, 974.5) * mm});
            skLineSegment(sketch, "E7.5.10.2", {"start": v(-552.5, 974.5) * mm, "end": v(-552.5, 924.5) * mm});
            skLineSegment(sketch, "E7.5.10.3", {"start": v(-552.5, 924.5) * mm, "end": v(-502.5, 924.5) * mm});
            skLineSegment(sketch, "E7.5.11.0", {"start": v(-502.5, 920.5) * mm, "end": v(-502.5, 870.5) * mm});
            skLineSegment(sketch, "E7.5.11.1", {"start": v(-552.5, 920.5) * mm, "end": v(-502.5, 920.5) * mm});
            skLineSegment(sketch, "E7.5.11.2", {"start": v(-552.5, 920.5) * mm, "end": v(-552.5, 870.5) * mm});
            skLineSegment(sketch, "E7.5.11.3", {"start": v(-552.5, 870.5) * mm, "end": v(-502.5, 870.5) * mm});
            skLineSegment(sketch, "E7.5.12.0", {"start": v(-502.5, 866.5) * mm, "end": v(-502.5, 816.5) * mm});
            skLineSegment(sketch, "E7.5.12.1", {"start": v(-552.5, 866.5) * mm, "end": v(-502.5, 866.5) * mm});
            skLineSegment(sketch, "E7.5.12.2", {"start": v(-552.5, 866.5) * mm, "end": v(-552.5, 816.5) * mm});
            skLineSegment(sketch, "E7.5.12.3", {"start": v(-552.5, 816.5) * mm, "end": v(-502.5, 816.5) * mm});
            skLineSegment(sketch, "E7.5.13.0", {"start": v(-502.5, 812.5) * mm, "end": v(-502.5, 762.5) * mm});
            skLineSegment(sketch, "E7.5.13.1", {"start": v(-552.5, 812.5) * mm, "end": v(-502.5, 812.5) * mm});
            skLineSegment(sketch, "E7.5.13.2", {"start": v(-552.5, 812.5) * mm, "end": v(-552.5, 762.5) * mm});
            skLineSegment(sketch, "E7.5.13.3", {"start": v(-552.5, 762.5) * mm, "end": v(-502.5, 762.5) * mm});
            skLineSegment(sketch, "E7.5.14.0", {"start": v(-502.5, 758.5) * mm, "end": v(-502.5, 708.5) * mm});
            skLineSegment(sketch, "E7.5.14.1", {"start": v(-552.5, 758.5) * mm, "end": v(-502.5, 758.5) * mm});
            skLineSegment(sketch, "E7.5.14.2", {"start": v(-552.5, 758.5) * mm, "end": v(-552.5, 708.5) * mm});
            skLineSegment(sketch, "E7.5.14.3", {"start": v(-552.5, 708.5) * mm, "end": v(-502.5, 708.5) * mm});
            skLineSegment(sketch, "E7.5.15.0", {"start": v(-502.5, 704.5) * mm, "end": v(-502.5, 654.5) * mm});
            skLineSegment(sketch, "E7.5.15.1", {"start": v(-552.5, 704.5) * mm, "end": v(-502.5, 704.5) * mm});
            skLineSegment(sketch, "E7.5.15.2", {"start": v(-552.5, 704.5) * mm, "end": v(-552.5, 654.5) * mm});
            skLineSegment(sketch, "E7.5.15.3", {"start": v(-552.5, 654.5) * mm, "end": v(-502.5, 654.5) * mm});
            skLineSegment(sketch, "E7.5.16.0", {"start": v(-502.5, 650.5) * mm, "end": v(-502.5, 600.5) * mm});
            skLineSegment(sketch, "E7.5.16.1", {"start": v(-552.5, 650.5) * mm, "end": v(-502.5, 650.5) * mm});
            skLineSegment(sketch, "E7.5.16.2", {"start": v(-552.5, 650.5) * mm, "end": v(-552.5, 600.5) * mm});
            skLineSegment(sketch, "E7.5.16.3", {"start": v(-552.5, 600.5) * mm, "end": v(-502.5, 600.5) * mm});
            skLineSegment(sketch, "E7.5.17.0", {"start": v(-502.5, 596.5) * mm, "end": v(-502.5, 546.5) * mm});
            skLineSegment(sketch, "E7.5.17.1", {"start": v(-552.5, 596.5) * mm, "end": v(-502.5, 596.5) * mm});
            skLineSegment(sketch, "E7.5.17.2", {"start": v(-552.5, 596.5) * mm, "end": v(-552.5, 546.5) * mm});
            skLineSegment(sketch, "E7.5.17.3", {"start": v(-552.5, 546.5) * mm, "end": v(-502.5, 546.5) * mm});
            skLineSegment(sketch, "E7.5.18.0", {"start": v(-502.5, 542.5) * mm, "end": v(-502.5, 492.5) * mm});
            skLineSegment(sketch, "E7.5.18.1", {"start": v(-552.5, 542.5) * mm, "end": v(-502.5, 542.5) * mm});
            skLineSegment(sketch, "E7.5.18.2", {"start": v(-552.5, 542.5) * mm, "end": v(-552.5, 492.5) * mm});
            skLineSegment(sketch, "E7.5.18.3", {"start": v(-552.5, 492.5) * mm, "end": v(-502.5, 492.5) * mm});
            skLineSegment(sketch, "E7.5.19.0", {"start": v(-502.5, 488.5) * mm, "end": v(-502.5, 438.5) * mm});
            skLineSegment(sketch, "E7.5.19.1", {"start": v(-552.5, 488.5) * mm, "end": v(-502.5, 488.5) * mm});
            skLineSegment(sketch, "E7.5.19.2", {"start": v(-552.5, 488.5) * mm, "end": v(-552.5, 438.5) * mm});
            skLineSegment(sketch, "E7.5.19.3", {"start": v(-552.5, 438.5) * mm, "end": v(-502.5, 438.5) * mm});
            skLineSegment(sketch, "E7.5.20.0", {"start": v(-502.5, 434.5) * mm, "end": v(-502.5, 384.5) * mm});
            skLineSegment(sketch, "E7.5.20.1", {"start": v(-552.5, 434.5) * mm, "end": v(-502.5, 434.5) * mm});
            skLineSegment(sketch, "E7.5.20.2", {"start": v(-552.5, 434.5) * mm, "end": v(-552.5, 384.5) * mm});
            skLineSegment(sketch, "E7.5.20.3", {"start": v(-552.5, 384.5) * mm, "end": v(-502.5, 384.5) * mm});
            skLineSegment(sketch, "E7.5.21.0", {"start": v(-502.5, 380.5) * mm, "end": v(-502.5, 330.5) * mm});
            skLineSegment(sketch, "E7.5.21.1", {"start": v(-552.5, 380.5) * mm, "end": v(-502.5, 380.5) * mm});
            skLineSegment(sketch, "E7.5.21.2", {"start": v(-552.5, 380.5) * mm, "end": v(-552.5, 330.5) * mm});
            skLineSegment(sketch, "E7.5.21.3", {"start": v(-552.5, 330.5) * mm, "end": v(-502.5, 330.5) * mm});
            skLineSegment(sketch, "E7.5.22.0", {"start": v(-502.5, 326.5) * mm, "end": v(-502.5, 276.5) * mm});
            skLineSegment(sketch, "E7.5.22.1", {"start": v(-552.5, 326.5) * mm, "end": v(-502.5, 326.5) * mm});
            skLineSegment(sketch, "E7.5.22.2", {"start": v(-552.5, 326.5) * mm, "end": v(-552.5, 276.5) * mm});
            skLineSegment(sketch, "E7.5.22.3", {"start": v(-552.5, 276.5) * mm, "end": v(-502.5, 276.5) * mm});
            skLineSegment(sketch, "E7.5.23.0", {"start": v(-502.5, 272.5) * mm, "end": v(-502.5, 222.5) * mm});
            skLineSegment(sketch, "E7.5.23.1", {"start": v(-552.5, 272.5) * mm, "end": v(-502.5, 272.5) * mm});
            skLineSegment(sketch, "E7.5.23.2", {"start": v(-552.5, 272.5) * mm, "end": v(-552.5, 222.5) * mm});
            skLineSegment(sketch, "E7.5.23.3", {"start": v(-552.5, 222.5) * mm, "end": v(-502.5, 222.5) * mm});
            skLineSegment(sketch, "E7.5.24.0", {"start": v(-502.5, 218.5) * mm, "end": v(-502.5, 168.5) * mm});
            skLineSegment(sketch, "E7.5.24.1", {"start": v(-552.5, 218.5) * mm, "end": v(-502.5, 218.5) * mm});
            skLineSegment(sketch, "E7.5.24.2", {"start": v(-552.5, 218.5) * mm, "end": v(-552.5, 168.5) * mm});
            skLineSegment(sketch, "E7.5.24.3", {"start": v(-552.5, 168.5) * mm, "end": v(-502.5, 168.5) * mm});
            skLineSegment(sketch, "E7.5.25.0", {"start": v(-502.5, 164.5) * mm, "end": v(-502.5, 114.5) * mm});
            skLineSegment(sketch, "E7.5.25.1", {"start": v(-552.5, 164.5) * mm, "end": v(-502.5, 164.5) * mm});
            skLineSegment(sketch, "E7.5.25.2", {"start": v(-552.5, 164.5) * mm, "end": v(-552.5, 114.5) * mm});
            skLineSegment(sketch, "E7.5.25.3", {"start": v(-552.5, 114.5) * mm, "end": v(-502.5, 114.5) * mm});
            skLineSegment(sketch, "E7.5.26.0", {"start": v(-502.5, 110.5) * mm, "end": v(-502.5, 60.5) * mm});
            skLineSegment(sketch, "E7.5.26.1", {"start": v(-552.5, 110.5) * mm, "end": v(-502.5, 110.5) * mm});
            skLineSegment(sketch, "E7.5.26.2", {"start": v(-552.5, 110.5) * mm, "end": v(-552.5, 60.5) * mm});
            skLineSegment(sketch, "E7.5.26.3", {"start": v(-552.5, 60.5) * mm, "end": v(-502.5, 60.5) * mm});
            skLineSegment(sketch, "E7.5.27.0", {"start": v(-502.5, 56.5) * mm, "end": v(-502.5, 6.5) * mm});
            skLineSegment(sketch, "E7.5.27.1", {"start": v(-552.5, 56.5) * mm, "end": v(-502.5, 56.5) * mm});
            skLineSegment(sketch, "E7.5.27.2", {"start": v(-552.5, 56.5) * mm, "end": v(-552.5, 6.5) * mm});
            skLineSegment(sketch, "E7.5.27.3", {"start": v(-552.5, 6.5) * mm, "end": v(-502.5, 6.5) * mm});
            skLineSegment(sketch, "E7.6.0.0", {"start": v(-448.5, 1514.5) * mm, "end": v(-448.5, 1464.5) * mm});
            skLineSegment(sketch, "E7.6.0.1", {"start": v(-498.5, 1514.5) * mm, "end": v(-448.5, 1514.5) * mm});
            skLineSegment(sketch, "E7.6.0.2", {"start": v(-498.5, 1514.5) * mm, "end": v(-498.5, 1464.5) * mm});
            skLineSegment(sketch, "E7.6.0.3", {"start": v(-498.5, 1464.5) * mm, "end": v(-448.5, 1464.5) * mm});
            skLineSegment(sketch, "E7.6.1.0", {"start": v(-448.5, 1460.5) * mm, "end": v(-448.5, 1410.5) * mm});
            skLineSegment(sketch, "E7.6.1.1", {"start": v(-498.5, 1460.5) * mm, "end": v(-448.5, 1460.5) * mm});
            skLineSegment(sketch, "E7.6.1.2", {"start": v(-498.5, 1460.5) * mm, "end": v(-498.5, 1410.5) * mm});
            skLineSegment(sketch, "E7.6.1.3", {"start": v(-498.5, 1410.5) * mm, "end": v(-448.5, 1410.5) * mm});
            skLineSegment(sketch, "E7.6.2.0", {"start": v(-448.5, 1406.5) * mm, "end": v(-448.5, 1356.5) * mm});
            skLineSegment(sketch, "E7.6.2.1", {"start": v(-498.5, 1406.5) * mm, "end": v(-448.5, 1406.5) * mm});
            skLineSegment(sketch, "E7.6.2.2", {"start": v(-498.5, 1406.5) * mm, "end": v(-498.5, 1356.5) * mm});
            skLineSegment(sketch, "E7.6.2.3", {"start": v(-498.5, 1356.5) * mm, "end": v(-448.5, 1356.5) * mm});
            skLineSegment(sketch, "E7.6.3.0", {"start": v(-448.5, 1352.5) * mm, "end": v(-448.5, 1302.5) * mm});
            skLineSegment(sketch, "E7.6.3.1", {"start": v(-498.5, 1352.5) * mm, "end": v(-448.5, 1352.5) * mm});
            skLineSegment(sketch, "E7.6.3.2", {"start": v(-498.5, 1352.5) * mm, "end": v(-498.5, 1302.5) * mm});
            skLineSegment(sketch, "E7.6.3.3", {"start": v(-498.5, 1302.5) * mm, "end": v(-448.5, 1302.5) * mm});
            skLineSegment(sketch, "E7.6.4.0", {"start": v(-448.5, 1298.5) * mm, "end": v(-448.5, 1248.5) * mm});
            skLineSegment(sketch, "E7.6.4.1", {"start": v(-498.5, 1298.5) * mm, "end": v(-448.5, 1298.5) * mm});
            skLineSegment(sketch, "E7.6.4.2", {"start": v(-498.5, 1298.5) * mm, "end": v(-498.5, 1248.5) * mm});
            skLineSegment(sketch, "E7.6.4.3", {"start": v(-498.5, 1248.5) * mm, "end": v(-448.5, 1248.5) * mm});
            skLineSegment(sketch, "E7.6.5.0", {"start": v(-448.5, 1244.5) * mm, "end": v(-448.5, 1194.5) * mm});
            skLineSegment(sketch, "E7.6.5.1", {"start": v(-498.5, 1244.5) * mm, "end": v(-448.5, 1244.5) * mm});
            skLineSegment(sketch, "E7.6.5.2", {"start": v(-498.5, 1244.5) * mm, "end": v(-498.5, 1194.5) * mm});
            skLineSegment(sketch, "E7.6.5.3", {"start": v(-498.5, 1194.5) * mm, "end": v(-448.5, 1194.5) * mm});
            skLineSegment(sketch, "E7.6.6.0", {"start": v(-448.5, 1190.5) * mm, "end": v(-448.5, 1140.5) * mm});
            skLineSegment(sketch, "E7.6.6.1", {"start": v(-498.5, 1190.5) * mm, "end": v(-448.5, 1190.5) * mm});
            skLineSegment(sketch, "E7.6.6.2", {"start": v(-498.5, 1190.5) * mm, "end": v(-498.5, 1140.5) * mm});
            skLineSegment(sketch, "E7.6.6.3", {"start": v(-498.5, 1140.5) * mm, "end": v(-448.5, 1140.5) * mm});
            skLineSegment(sketch, "E7.6.7.0", {"start": v(-448.5, 1136.5) * mm, "end": v(-448.5, 1086.5) * mm});
            skLineSegment(sketch, "E7.6.7.1", {"start": v(-498.5, 1136.5) * mm, "end": v(-448.5, 1136.5) * mm});
            skLineSegment(sketch, "E7.6.7.2", {"start": v(-498.5, 1136.5) * mm, "end": v(-498.5, 1086.5) * mm});
            skLineSegment(sketch, "E7.6.7.3", {"start": v(-498.5, 1086.5) * mm, "end": v(-448.5, 1086.5) * mm});
            skLineSegment(sketch, "E7.6.8.0", {"start": v(-448.5, 1082.5) * mm, "end": v(-448.5, 1032.5) * mm});
            skLineSegment(sketch, "E7.6.8.1", {"start": v(-498.5, 1082.5) * mm, "end": v(-448.5, 1082.5) * mm});
            skLineSegment(sketch, "E7.6.8.2", {"start": v(-498.5, 1082.5) * mm, "end": v(-498.5, 1032.5) * mm});
            skLineSegment(sketch, "E7.6.8.3", {"start": v(-498.5, 1032.5) * mm, "end": v(-448.5, 1032.5) * mm});
            skLineSegment(sketch, "E7.6.9.0", {"start": v(-448.5, 1028.5) * mm, "end": v(-448.5, 978.5) * mm});
            skLineSegment(sketch, "E7.6.9.1", {"start": v(-498.5, 1028.5) * mm, "end": v(-448.5, 1028.5) * mm});
            skLineSegment(sketch, "E7.6.9.2", {"start": v(-498.5, 1028.5) * mm, "end": v(-498.5, 978.5) * mm});
            skLineSegment(sketch, "E7.6.9.3", {"start": v(-498.5, 978.5) * mm, "end": v(-448.5, 978.5) * mm});
            skLineSegment(sketch, "E7.6.10.0", {"start": v(-448.5, 974.5) * mm, "end": v(-448.5, 924.5) * mm});
            skLineSegment(sketch, "E7.6.10.1", {"start": v(-498.5, 974.5) * mm, "end": v(-448.5, 974.5) * mm});
            skLineSegment(sketch, "E7.6.10.2", {"start": v(-498.5, 974.5) * mm, "end": v(-498.5, 924.5) * mm});
            skLineSegment(sketch, "E7.6.10.3", {"start": v(-498.5, 924.5) * mm, "end": v(-448.5, 924.5) * mm});
            skLineSegment(sketch, "E7.6.11.0", {"start": v(-448.5, 920.5) * mm, "end": v(-448.5, 870.5) * mm});
            skLineSegment(sketch, "E7.6.11.1", {"start": v(-498.5, 920.5) * mm, "end": v(-448.5, 920.5) * mm});
            skLineSegment(sketch, "E7.6.11.2", {"start": v(-498.5, 920.5) * mm, "end": v(-498.5, 870.5) * mm});
            skLineSegment(sketch, "E7.6.11.3", {"start": v(-498.5, 870.5) * mm, "end": v(-448.5, 870.5) * mm});
            skLineSegment(sketch, "E7.6.12.0", {"start": v(-448.5, 866.5) * mm, "end": v(-448.5, 816.5) * mm});
            skLineSegment(sketch, "E7.6.12.1", {"start": v(-498.5, 866.5) * mm, "end": v(-448.5, 866.5) * mm});
            skLineSegment(sketch, "E7.6.12.2", {"start": v(-498.5, 866.5) * mm, "end": v(-498.5, 816.5) * mm});
            skLineSegment(sketch, "E7.6.12.3", {"start": v(-498.5, 816.5) * mm, "end": v(-448.5, 816.5) * mm});
            skLineSegment(sketch, "E7.6.13.0", {"start": v(-448.5, 812.5) * mm, "end": v(-448.5, 762.5) * mm});
            skLineSegment(sketch, "E7.6.13.1", {"start": v(-498.5, 812.5) * mm, "end": v(-448.5, 812.5) * mm});
            skLineSegment(sketch, "E7.6.13.2", {"start": v(-498.5, 812.5) * mm, "end": v(-498.5, 762.5) * mm});
            skLineSegment(sketch, "E7.6.13.3", {"start": v(-498.5, 762.5) * mm, "end": v(-448.5, 762.5) * mm});
            skLineSegment(sketch, "E7.6.14.0", {"start": v(-448.5, 758.5) * mm, "end": v(-448.5, 708.5) * mm});
            skLineSegment(sketch, "E7.6.14.1", {"start": v(-498.5, 758.5) * mm, "end": v(-448.5, 758.5) * mm});
            skLineSegment(sketch, "E7.6.14.2", {"start": v(-498.5, 758.5) * mm, "end": v(-498.5, 708.5) * mm});
            skLineSegment(sketch, "E7.6.14.3", {"start": v(-498.5, 708.5) * mm, "end": v(-448.5, 708.5) * mm});
            skLineSegment(sketch, "E7.6.15.0", {"start": v(-448.5, 704.5) * mm, "end": v(-448.5, 654.5) * mm});
            skLineSegment(sketch, "E7.6.15.1", {"start": v(-498.5, 704.5) * mm, "end": v(-448.5, 704.5) * mm});
            skLineSegment(sketch, "E7.6.15.2", {"start": v(-498.5, 704.5) * mm, "end": v(-498.5, 654.5) * mm});
            skLineSegment(sketch, "E7.6.15.3", {"start": v(-498.5, 654.5) * mm, "end": v(-448.5, 654.5) * mm});
            skLineSegment(sketch, "E7.6.16.0", {"start": v(-448.5, 650.5) * mm, "end": v(-448.5, 600.5) * mm});
            skLineSegment(sketch, "E7.6.16.1", {"start": v(-498.5, 650.5) * mm, "end": v(-448.5, 650.5) * mm});
            skLineSegment(sketch, "E7.6.16.2", {"start": v(-498.5, 650.5) * mm, "end": v(-498.5, 600.5) * mm});
            skLineSegment(sketch, "E7.6.16.3", {"start": v(-498.5, 600.5) * mm, "end": v(-448.5, 600.5) * mm});
            skLineSegment(sketch, "E7.6.17.0", {"start": v(-448.5, 596.5) * mm, "end": v(-448.5, 546.5) * mm});
            skLineSegment(sketch, "E7.6.17.1", {"start": v(-498.5, 596.5) * mm, "end": v(-448.5, 596.5) * mm});
            skLineSegment(sketch, "E7.6.17.2", {"start": v(-498.5, 596.5) * mm, "end": v(-498.5, 546.5) * mm});
            skLineSegment(sketch, "E7.6.17.3", {"start": v(-498.5, 546.5) * mm, "end": v(-448.5, 546.5) * mm});
            skLineSegment(sketch, "E7.6.18.0", {"start": v(-448.5, 542.5) * mm, "end": v(-448.5, 492.5) * mm});
            skLineSegment(sketch, "E7.6.18.1", {"start": v(-498.5, 542.5) * mm, "end": v(-448.5, 542.5) * mm});
            skLineSegment(sketch, "E7.6.18.2", {"start": v(-498.5, 542.5) * mm, "end": v(-498.5, 492.5) * mm});
            skLineSegment(sketch, "E7.6.18.3", {"start": v(-498.5, 492.5) * mm, "end": v(-448.5, 492.5) * mm});
            skLineSegment(sketch, "E7.6.19.0", {"start": v(-448.5, 488.5) * mm, "end": v(-448.5, 438.5) * mm});
            skLineSegment(sketch, "E7.6.19.1", {"start": v(-498.5, 488.5) * mm, "end": v(-448.5, 488.5) * mm});
            skLineSegment(sketch, "E7.6.19.2", {"start": v(-498.5, 488.5) * mm, "end": v(-498.5, 438.5) * mm});
            skLineSegment(sketch, "E7.6.19.3", {"start": v(-498.5, 438.5) * mm, "end": v(-448.5, 438.5) * mm});
            skLineSegment(sketch, "E7.6.20.0", {"start": v(-448.5, 434.5) * mm, "end": v(-448.5, 384.5) * mm});
            skLineSegment(sketch, "E7.6.20.1", {"start": v(-498.5, 434.5) * mm, "end": v(-448.5, 434.5) * mm});
            skLineSegment(sketch, "E7.6.20.2", {"start": v(-498.5, 434.5) * mm, "end": v(-498.5, 384.5) * mm});
            skLineSegment(sketch, "E7.6.20.3", {"start": v(-498.5, 384.5) * mm, "end": v(-448.5, 384.5) * mm});
            skLineSegment(sketch, "E7.6.21.0", {"start": v(-448.5, 380.5) * mm, "end": v(-448.5, 330.5) * mm});
            skLineSegment(sketch, "E7.6.21.1", {"start": v(-498.5, 380.5) * mm, "end": v(-448.5, 380.5) * mm});
            skLineSegment(sketch, "E7.6.21.2", {"start": v(-498.5, 380.5) * mm, "end": v(-498.5, 330.5) * mm});
            skLineSegment(sketch, "E7.6.21.3", {"start": v(-498.5, 330.5) * mm, "end": v(-448.5, 330.5) * mm});
            skLineSegment(sketch, "E7.6.22.0", {"start": v(-448.5, 326.5) * mm, "end": v(-448.5, 276.5) * mm});
            skLineSegment(sketch, "E7.6.22.1", {"start": v(-498.5, 326.5) * mm, "end": v(-448.5, 326.5) * mm});
            skLineSegment(sketch, "E7.6.22.2", {"start": v(-498.5, 326.5) * mm, "end": v(-498.5, 276.5) * mm});
            skLineSegment(sketch, "E7.6.22.3", {"start": v(-498.5, 276.5) * mm, "end": v(-448.5, 276.5) * mm});
            skLineSegment(sketch, "E7.6.23.0", {"start": v(-448.5, 272.5) * mm, "end": v(-448.5, 222.5) * mm});
            skLineSegment(sketch, "E7.6.23.1", {"start": v(-498.5, 272.5) * mm, "end": v(-448.5, 272.5) * mm});
            skLineSegment(sketch, "E7.6.23.2", {"start": v(-498.5, 272.5) * mm, "end": v(-498.5, 222.5) * mm});
            skLineSegment(sketch, "E7.6.23.3", {"start": v(-498.5, 222.5) * mm, "end": v(-448.5, 222.5) * mm});
            skLineSegment(sketch, "E7.6.24.0", {"start": v(-448.5, 218.5) * mm, "end": v(-448.5, 168.5) * mm});
            skLineSegment(sketch, "E7.6.24.1", {"start": v(-498.5, 218.5) * mm, "end": v(-448.5, 218.5) * mm});
            skLineSegment(sketch, "E7.6.24.2", {"start": v(-498.5, 218.5) * mm, "end": v(-498.5, 168.5) * mm});
            skLineSegment(sketch, "E7.6.24.3", {"start": v(-498.5, 168.5) * mm, "end": v(-448.5, 168.5) * mm});
            skLineSegment(sketch, "E7.6.25.0", {"start": v(-448.5, 164.5) * mm, "end": v(-448.5, 114.5) * mm});
            skLineSegment(sketch, "E7.6.25.1", {"start": v(-498.5, 164.5) * mm, "end": v(-448.5, 164.5) * mm});
            skLineSegment(sketch, "E7.6.25.2", {"start": v(-498.5, 164.5) * mm, "end": v(-498.5, 114.5) * mm});
            skLineSegment(sketch, "E7.6.25.3", {"start": v(-498.5, 114.5) * mm, "end": v(-448.5, 114.5) * mm});
            skLineSegment(sketch, "E7.6.26.0", {"start": v(-448.5, 110.5) * mm, "end": v(-448.5, 60.5) * mm});
            skLineSegment(sketch, "E7.6.26.1", {"start": v(-498.5, 110.5) * mm, "end": v(-448.5, 110.5) * mm});
            skLineSegment(sketch, "E7.6.26.2", {"start": v(-498.5, 110.5) * mm, "end": v(-498.5, 60.5) * mm});
            skLineSegment(sketch, "E7.6.26.3", {"start": v(-498.5, 60.5) * mm, "end": v(-448.5, 60.5) * mm});
            skLineSegment(sketch, "E7.6.27.0", {"start": v(-448.5, 56.5) * mm, "end": v(-448.5, 6.5) * mm});
            skLineSegment(sketch, "E7.6.27.1", {"start": v(-498.5, 56.5) * mm, "end": v(-448.5, 56.5) * mm});
            skLineSegment(sketch, "E7.6.27.2", {"start": v(-498.5, 56.5) * mm, "end": v(-498.5, 6.5) * mm});
            skLineSegment(sketch, "E7.6.27.3", {"start": v(-498.5, 6.5) * mm, "end": v(-448.5, 6.5) * mm});
            skLineSegment(sketch, "E7.7.0.0", {"start": v(-394.5, 1514.5) * mm, "end": v(-394.5, 1464.5) * mm});
            skLineSegment(sketch, "E7.7.0.1", {"start": v(-444.5, 1514.5) * mm, "end": v(-394.5, 1514.5) * mm});
            skLineSegment(sketch, "E7.7.0.2", {"start": v(-444.5, 1514.5) * mm, "end": v(-444.5, 1464.5) * mm});
            skLineSegment(sketch, "E7.7.0.3", {"start": v(-444.5, 1464.5) * mm, "end": v(-394.5, 1464.5) * mm});
            skLineSegment(sketch, "E7.7.1.0", {"start": v(-394.5, 1460.5) * mm, "end": v(-394.5, 1410.5) * mm});
            skLineSegment(sketch, "E7.7.1.1", {"start": v(-444.5, 1460.5) * mm, "end": v(-394.5, 1460.5) * mm});
            skLineSegment(sketch, "E7.7.1.2", {"start": v(-444.5, 1460.5) * mm, "end": v(-444.5, 1410.5) * mm});
            skLineSegment(sketch, "E7.7.1.3", {"start": v(-444.5, 1410.5) * mm, "end": v(-394.5, 1410.5) * mm});
            skLineSegment(sketch, "E7.7.2.0", {"start": v(-394.5, 1406.5) * mm, "end": v(-394.5, 1356.5) * mm});
            skLineSegment(sketch, "E7.7.2.1", {"start": v(-444.5, 1406.5) * mm, "end": v(-394.5, 1406.5) * mm});
            skLineSegment(sketch, "E7.7.2.2", {"start": v(-444.5, 1406.5) * mm, "end": v(-444.5, 1356.5) * mm});
            skLineSegment(sketch, "E7.7.2.3", {"start": v(-444.5, 1356.5) * mm, "end": v(-394.5, 1356.5) * mm});
            skLineSegment(sketch, "E7.7.3.0", {"start": v(-394.5, 1352.5) * mm, "end": v(-394.5, 1302.5) * mm});
            skLineSegment(sketch, "E7.7.3.1", {"start": v(-444.5, 1352.5) * mm, "end": v(-394.5, 1352.5) * mm});
            skLineSegment(sketch, "E7.7.3.2", {"start": v(-444.5, 1352.5) * mm, "end": v(-444.5, 1302.5) * mm});
            skLineSegment(sketch, "E7.7.3.3", {"start": v(-444.5, 1302.5) * mm, "end": v(-394.5, 1302.5) * mm});
            skLineSegment(sketch, "E7.7.4.0", {"start": v(-394.5, 1298.5) * mm, "end": v(-394.5, 1248.5) * mm});
            skLineSegment(sketch, "E7.7.4.1", {"start": v(-444.5, 1298.5) * mm, "end": v(-394.5, 1298.5) * mm});
            skLineSegment(sketch, "E7.7.4.2", {"start": v(-444.5, 1298.5) * mm, "end": v(-444.5, 1248.5) * mm});
            skLineSegment(sketch, "E7.7.4.3", {"start": v(-444.5, 1248.5) * mm, "end": v(-394.5, 1248.5) * mm});
            skLineSegment(sketch, "E7.7.5.0", {"start": v(-394.5, 1244.5) * mm, "end": v(-394.5, 1194.5) * mm});
            skLineSegment(sketch, "E7.7.5.1", {"start": v(-444.5, 1244.5) * mm, "end": v(-394.5, 1244.5) * mm});
            skLineSegment(sketch, "E7.7.5.2", {"start": v(-444.5, 1244.5) * mm, "end": v(-444.5, 1194.5) * mm});
            skLineSegment(sketch, "E7.7.5.3", {"start": v(-444.5, 1194.5) * mm, "end": v(-394.5, 1194.5) * mm});
            skLineSegment(sketch, "E7.7.6.0", {"start": v(-394.5, 1190.5) * mm, "end": v(-394.5, 1140.5) * mm});
            skLineSegment(sketch, "E7.7.6.1", {"start": v(-444.5, 1190.5) * mm, "end": v(-394.5, 1190.5) * mm});
            skLineSegment(sketch, "E7.7.6.2", {"start": v(-444.5, 1190.5) * mm, "end": v(-444.5, 1140.5) * mm});
            skLineSegment(sketch, "E7.7.6.3", {"start": v(-444.5, 1140.5) * mm, "end": v(-394.5, 1140.5) * mm});
            skLineSegment(sketch, "E7.7.7.0", {"start": v(-394.5, 1136.5) * mm, "end": v(-394.5, 1086.5) * mm});
            skLineSegment(sketch, "E7.7.7.1", {"start": v(-444.5, 1136.5) * mm, "end": v(-394.5, 1136.5) * mm});
            skLineSegment(sketch, "E7.7.7.2", {"start": v(-444.5, 1136.5) * mm, "end": v(-444.5, 1086.5) * mm});
            skLineSegment(sketch, "E7.7.7.3", {"start": v(-444.5, 1086.5) * mm, "end": v(-394.5, 1086.5) * mm});
            skLineSegment(sketch, "E7.7.8.0", {"start": v(-394.5, 1082.5) * mm, "end": v(-394.5, 1032.5) * mm});
            skLineSegment(sketch, "E7.7.8.1", {"start": v(-444.5, 1082.5) * mm, "end": v(-394.5, 1082.5) * mm});
            skLineSegment(sketch, "E7.7.8.2", {"start": v(-444.5, 1082.5) * mm, "end": v(-444.5, 1032.5) * mm});
            skLineSegment(sketch, "E7.7.8.3", {"start": v(-444.5, 1032.5) * mm, "end": v(-394.5, 1032.5) * mm});
            skLineSegment(sketch, "E7.7.9.0", {"start": v(-394.5, 1028.5) * mm, "end": v(-394.5, 978.5) * mm});
            skLineSegment(sketch, "E7.7.9.1", {"start": v(-444.5, 1028.5) * mm, "end": v(-394.5, 1028.5) * mm});
            skLineSegment(sketch, "E7.7.9.2", {"start": v(-444.5, 1028.5) * mm, "end": v(-444.5, 978.5) * mm});
            skLineSegment(sketch, "E7.7.9.3", {"start": v(-444.5, 978.5) * mm, "end": v(-394.5, 978.5) * mm});
            skLineSegment(sketch, "E7.7.10.0", {"start": v(-394.5, 974.5) * mm, "end": v(-394.5, 924.5) * mm});
            skLineSegment(sketch, "E7.7.10.1", {"start": v(-444.5, 974.5) * mm, "end": v(-394.5, 974.5) * mm});
            skLineSegment(sketch, "E7.7.10.2", {"start": v(-444.5, 974.5) * mm, "end": v(-444.5, 924.5) * mm});
            skLineSegment(sketch, "E7.7.10.3", {"start": v(-444.5, 924.5) * mm, "end": v(-394.5, 924.5) * mm});
            skLineSegment(sketch, "E7.7.11.0", {"start": v(-394.5, 920.5) * mm, "end": v(-394.5, 870.5) * mm});
            skLineSegment(sketch, "E7.7.11.1", {"start": v(-444.5, 920.5) * mm, "end": v(-394.5, 920.5) * mm});
            skLineSegment(sketch, "E7.7.11.2", {"start": v(-444.5, 920.5) * mm, "end": v(-444.5, 870.5) * mm});
            skLineSegment(sketch, "E7.7.11.3", {"start": v(-444.5, 870.5) * mm, "end": v(-394.5, 870.5) * mm});
            skLineSegment(sketch, "E7.7.12.0", {"start": v(-394.5, 866.5) * mm, "end": v(-394.5, 816.5) * mm});
            skLineSegment(sketch, "E7.7.12.1", {"start": v(-444.5, 866.5) * mm, "end": v(-394.5, 866.5) * mm});
            skLineSegment(sketch, "E7.7.12.2", {"start": v(-444.5, 866.5) * mm, "end": v(-444.5, 816.5) * mm});
            skLineSegment(sketch, "E7.7.12.3", {"start": v(-444.5, 816.5) * mm, "end": v(-394.5, 816.5) * mm});
            skLineSegment(sketch, "E7.7.13.0", {"start": v(-394.5, 812.5) * mm, "end": v(-394.5, 762.5) * mm});
            skLineSegment(sketch, "E7.7.13.1", {"start": v(-444.5, 812.5) * mm, "end": v(-394.5, 812.5) * mm});
            skLineSegment(sketch, "E7.7.13.2", {"start": v(-444.5, 812.5) * mm, "end": v(-444.5, 762.5) * mm});
            skLineSegment(sketch, "E7.7.13.3", {"start": v(-444.5, 762.5) * mm, "end": v(-394.5, 762.5) * mm});
            skLineSegment(sketch, "E7.7.14.0", {"start": v(-394.5, 758.5) * mm, "end": v(-394.5, 708.5) * mm});
            skLineSegment(sketch, "E7.7.14.1", {"start": v(-444.5, 758.5) * mm, "end": v(-394.5, 758.5) * mm});
            skLineSegment(sketch, "E7.7.14.2", {"start": v(-444.5, 758.5) * mm, "end": v(-444.5, 708.5) * mm});
            skLineSegment(sketch, "E7.7.14.3", {"start": v(-444.5, 708.5) * mm, "end": v(-394.5, 708.5) * mm});
            skLineSegment(sketch, "E7.7.15.0", {"start": v(-394.5, 704.5) * mm, "end": v(-394.5, 654.5) * mm});
            skLineSegment(sketch, "E7.7.15.1", {"start": v(-444.5, 704.5) * mm, "end": v(-394.5, 704.5) * mm});
            skLineSegment(sketch, "E7.7.15.2", {"start": v(-444.5, 704.5) * mm, "end": v(-444.5, 654.5) * mm});
            skLineSegment(sketch, "E7.7.15.3", {"start": v(-444.5, 654.5) * mm, "end": v(-394.5, 654.5) * mm});
            skLineSegment(sketch, "E7.7.16.0", {"start": v(-394.5, 650.5) * mm, "end": v(-394.5, 600.5) * mm});
            skLineSegment(sketch, "E7.7.16.1", {"start": v(-444.5, 650.5) * mm, "end": v(-394.5, 650.5) * mm});
            skLineSegment(sketch, "E7.7.16.2", {"start": v(-444.5, 650.5) * mm, "end": v(-444.5, 600.5) * mm});
            skLineSegment(sketch, "E7.7.16.3", {"start": v(-444.5, 600.5) * mm, "end": v(-394.5, 600.5) * mm});
            skLineSegment(sketch, "E7.7.17.0", {"start": v(-394.5, 596.5) * mm, "end": v(-394.5, 546.5) * mm});
            skLineSegment(sketch, "E7.7.17.1", {"start": v(-444.5, 596.5) * mm, "end": v(-394.5, 596.5) * mm});
            skLineSegment(sketch, "E7.7.17.2", {"start": v(-444.5, 596.5) * mm, "end": v(-444.5, 546.5) * mm});
            skLineSegment(sketch, "E7.7.17.3", {"start": v(-444.5, 546.5) * mm, "end": v(-394.5, 546.5) * mm});
            skLineSegment(sketch, "E7.7.18.0", {"start": v(-394.5, 542.5) * mm, "end": v(-394.5, 492.5) * mm});
            skLineSegment(sketch, "E7.7.18.1", {"start": v(-444.5, 542.5) * mm, "end": v(-394.5, 542.5) * mm});
            skLineSegment(sketch, "E7.7.18.2", {"start": v(-444.5, 542.5) * mm, "end": v(-444.5, 492.5) * mm});
            skLineSegment(sketch, "E7.7.18.3", {"start": v(-444.5, 492.5) * mm, "end": v(-394.5, 492.5) * mm});
            skLineSegment(sketch, "E7.7.19.0", {"start": v(-394.5, 488.5) * mm, "end": v(-394.5, 438.5) * mm});
            skLineSegment(sketch, "E7.7.19.1", {"start": v(-444.5, 488.5) * mm, "end": v(-394.5, 488.5) * mm});
            skLineSegment(sketch, "E7.7.19.2", {"start": v(-444.5, 488.5) * mm, "end": v(-444.5, 438.5) * mm});
            skLineSegment(sketch, "E7.7.19.3", {"start": v(-444.5, 438.5) * mm, "end": v(-394.5, 438.5) * mm});
            skLineSegment(sketch, "E7.7.20.0", {"start": v(-394.5, 434.5) * mm, "end": v(-394.5, 384.5) * mm});
            skLineSegment(sketch, "E7.7.20.1", {"start": v(-444.5, 434.5) * mm, "end": v(-394.5, 434.5) * mm});
            skLineSegment(sketch, "E7.7.20.2", {"start": v(-444.5, 434.5) * mm, "end": v(-444.5, 384.5) * mm});
            skLineSegment(sketch, "E7.7.20.3", {"start": v(-444.5, 384.5) * mm, "end": v(-394.5, 384.5) * mm});
            skLineSegment(sketch, "E7.7.21.0", {"start": v(-394.5, 380.5) * mm, "end": v(-394.5, 330.5) * mm});
            skLineSegment(sketch, "E7.7.21.1", {"start": v(-444.5, 380.5) * mm, "end": v(-394.5, 380.5) * mm});
            skLineSegment(sketch, "E7.7.21.2", {"start": v(-444.5, 380.5) * mm, "end": v(-444.5, 330.5) * mm});
            skLineSegment(sketch, "E7.7.21.3", {"start": v(-444.5, 330.5) * mm, "end": v(-394.5, 330.5) * mm});
            skLineSegment(sketch, "E7.7.22.0", {"start": v(-394.5, 326.5) * mm, "end": v(-394.5, 276.5) * mm});
            skLineSegment(sketch, "E7.7.22.1", {"start": v(-444.5, 326.5) * mm, "end": v(-394.5, 326.5) * mm});
            skLineSegment(sketch, "E7.7.22.2", {"start": v(-444.5, 326.5) * mm, "end": v(-444.5, 276.5) * mm});
            skLineSegment(sketch, "E7.7.22.3", {"start": v(-444.5, 276.5) * mm, "end": v(-394.5, 276.5) * mm});
            skLineSegment(sketch, "E7.7.23.0", {"start": v(-394.5, 272.5) * mm, "end": v(-394.5, 222.5) * mm});
            skLineSegment(sketch, "E7.7.23.1", {"start": v(-444.5, 272.5) * mm, "end": v(-394.5, 272.5) * mm});
            skLineSegment(sketch, "E7.7.23.2", {"start": v(-444.5, 272.5) * mm, "end": v(-444.5, 222.5) * mm});
            skLineSegment(sketch, "E7.7.23.3", {"start": v(-444.5, 222.5) * mm, "end": v(-394.5, 222.5) * mm});
            skLineSegment(sketch, "E7.7.24.0", {"start": v(-394.5, 218.5) * mm, "end": v(-394.5, 168.5) * mm});
            skLineSegment(sketch, "E7.7.24.1", {"start": v(-444.5, 218.5) * mm, "end": v(-394.5, 218.5) * mm});
            skLineSegment(sketch, "E7.7.24.2", {"start": v(-444.5, 218.5) * mm, "end": v(-444.5, 168.5) * mm});
            skLineSegment(sketch, "E7.7.24.3", {"start": v(-444.5, 168.5) * mm, "end": v(-394.5, 168.5) * mm});
            skLineSegment(sketch, "E7.7.25.0", {"start": v(-394.5, 164.5) * mm, "end": v(-394.5, 114.5) * mm});
            skLineSegment(sketch, "E7.7.25.1", {"start": v(-444.5, 164.5) * mm, "end": v(-394.5, 164.5) * mm});
            skLineSegment(sketch, "E7.7.25.2", {"start": v(-444.5, 164.5) * mm, "end": v(-444.5, 114.5) * mm});
            skLineSegment(sketch, "E7.7.25.3", {"start": v(-444.5, 114.5) * mm, "end": v(-394.5, 114.5) * mm});
            skLineSegment(sketch, "E7.7.26.0", {"start": v(-394.5, 110.5) * mm, "end": v(-394.5, 60.5) * mm});
            skLineSegment(sketch, "E7.7.26.1", {"start": v(-444.5, 110.5) * mm, "end": v(-394.5, 110.5) * mm});
            skLineSegment(sketch, "E7.7.26.2", {"start": v(-444.5, 110.5) * mm, "end": v(-444.5, 60.5) * mm});
            skLineSegment(sketch, "E7.7.26.3", {"start": v(-444.5, 60.5) * mm, "end": v(-394.5, 60.5) * mm});
            skLineSegment(sketch, "E7.7.27.0", {"start": v(-394.5, 56.5) * mm, "end": v(-394.5, 6.5) * mm});
            skLineSegment(sketch, "E7.7.27.1", {"start": v(-444.5, 56.5) * mm, "end": v(-394.5, 56.5) * mm});
            skLineSegment(sketch, "E7.7.27.2", {"start": v(-444.5, 56.5) * mm, "end": v(-444.5, 6.5) * mm});
            skLineSegment(sketch, "E7.7.27.3", {"start": v(-444.5, 6.5) * mm, "end": v(-394.5, 6.5) * mm});
            skLineSegment(sketch, "E7.8.0.0", {"start": v(-340.5, 1514.5) * mm, "end": v(-340.5, 1464.5) * mm});
            skLineSegment(sketch, "E7.8.0.1", {"start": v(-390.5, 1514.5) * mm, "end": v(-340.5, 1514.5) * mm});
            skLineSegment(sketch, "E7.8.0.2", {"start": v(-390.5, 1514.5) * mm, "end": v(-390.5, 1464.5) * mm});
            skLineSegment(sketch, "E7.8.0.3", {"start": v(-390.5, 1464.5) * mm, "end": v(-340.5, 1464.5) * mm});
            skLineSegment(sketch, "E7.8.1.0", {"start": v(-340.5, 1460.5) * mm, "end": v(-340.5, 1410.5) * mm});
            skLineSegment(sketch, "E7.8.1.1", {"start": v(-390.5, 1460.5) * mm, "end": v(-340.5, 1460.5) * mm});
            skLineSegment(sketch, "E7.8.1.2", {"start": v(-390.5, 1460.5) * mm, "end": v(-390.5, 1410.5) * mm});
            skLineSegment(sketch, "E7.8.1.3", {"start": v(-390.5, 1410.5) * mm, "end": v(-340.5, 1410.5) * mm});
            skLineSegment(sketch, "E7.8.2.0", {"start": v(-340.5, 1406.5) * mm, "end": v(-340.5, 1356.5) * mm});
            skLineSegment(sketch, "E7.8.2.1", {"start": v(-390.5, 1406.5) * mm, "end": v(-340.5, 1406.5) * mm});
            skLineSegment(sketch, "E7.8.2.2", {"start": v(-390.5, 1406.5) * mm, "end": v(-390.5, 1356.5) * mm});
            skLineSegment(sketch, "E7.8.2.3", {"start": v(-390.5, 1356.5) * mm, "end": v(-340.5, 1356.5) * mm});
            skLineSegment(sketch, "E7.8.3.0", {"start": v(-340.5, 1352.5) * mm, "end": v(-340.5, 1302.5) * mm});
            skLineSegment(sketch, "E7.8.3.1", {"start": v(-390.5, 1352.5) * mm, "end": v(-340.5, 1352.5) * mm});
            skLineSegment(sketch, "E7.8.3.2", {"start": v(-390.5, 1352.5) * mm, "end": v(-390.5, 1302.5) * mm});
            skLineSegment(sketch, "E7.8.3.3", {"start": v(-390.5, 1302.5) * mm, "end": v(-340.5, 1302.5) * mm});
            skLineSegment(sketch, "E7.8.4.0", {"start": v(-340.5, 1298.5) * mm, "end": v(-340.5, 1248.5) * mm});
            skLineSegment(sketch, "E7.8.4.1", {"start": v(-390.5, 1298.5) * mm, "end": v(-340.5, 1298.5) * mm});
            skLineSegment(sketch, "E7.8.4.2", {"start": v(-390.5, 1298.5) * mm, "end": v(-390.5, 1248.5) * mm});
            skLineSegment(sketch, "E7.8.4.3", {"start": v(-390.5, 1248.5) * mm, "end": v(-340.5, 1248.5) * mm});
            skLineSegment(sketch, "E7.8.5.0", {"start": v(-340.5, 1244.5) * mm, "end": v(-340.5, 1194.5) * mm});
            skLineSegment(sketch, "E7.8.5.1", {"start": v(-390.5, 1244.5) * mm, "end": v(-340.5, 1244.5) * mm});
            skLineSegment(sketch, "E7.8.5.2", {"start": v(-390.5, 1244.5) * mm, "end": v(-390.5, 1194.5) * mm});
            skLineSegment(sketch, "E7.8.5.3", {"start": v(-390.5, 1194.5) * mm, "end": v(-340.5, 1194.5) * mm});
            skLineSegment(sketch, "E7.8.6.0", {"start": v(-340.5, 1190.5) * mm, "end": v(-340.5, 1140.5) * mm});
            skLineSegment(sketch, "E7.8.6.1", {"start": v(-390.5, 1190.5) * mm, "end": v(-340.5, 1190.5) * mm});
            skLineSegment(sketch, "E7.8.6.2", {"start": v(-390.5, 1190.5) * mm, "end": v(-390.5, 1140.5) * mm});
            skLineSegment(sketch, "E7.8.6.3", {"start": v(-390.5, 1140.5) * mm, "end": v(-340.5, 1140.5) * mm});
            skLineSegment(sketch, "E7.8.7.0", {"start": v(-340.5, 1136.5) * mm, "end": v(-340.5, 1086.5) * mm});
            skLineSegment(sketch, "E7.8.7.1", {"start": v(-390.5, 1136.5) * mm, "end": v(-340.5, 1136.5) * mm});
            skLineSegment(sketch, "E7.8.7.2", {"start": v(-390.5, 1136.5) * mm, "end": v(-390.5, 1086.5) * mm});
            skLineSegment(sketch, "E7.8.7.3", {"start": v(-390.5, 1086.5) * mm, "end": v(-340.5, 1086.5) * mm});
            skLineSegment(sketch, "E7.8.8.0", {"start": v(-340.5, 1082.5) * mm, "end": v(-340.5, 1032.5) * mm});
            skLineSegment(sketch, "E7.8.8.1", {"start": v(-390.5, 1082.5) * mm, "end": v(-340.5, 1082.5) * mm});
            skLineSegment(sketch, "E7.8.8.2", {"start": v(-390.5, 1082.5) * mm, "end": v(-390.5, 1032.5) * mm});
            skLineSegment(sketch, "E7.8.8.3", {"start": v(-390.5, 1032.5) * mm, "end": v(-340.5, 1032.5) * mm});
            skLineSegment(sketch, "E7.8.9.0", {"start": v(-340.5, 1028.5) * mm, "end": v(-340.5, 978.5) * mm});
            skLineSegment(sketch, "E7.8.9.1", {"start": v(-390.5, 1028.5) * mm, "end": v(-340.5, 1028.5) * mm});
            skLineSegment(sketch, "E7.8.9.2", {"start": v(-390.5, 1028.5) * mm, "end": v(-390.5, 978.5) * mm});
            skLineSegment(sketch, "E7.8.9.3", {"start": v(-390.5, 978.5) * mm, "end": v(-340.5, 978.5) * mm});
            skLineSegment(sketch, "E7.8.10.0", {"start": v(-340.5, 974.5) * mm, "end": v(-340.5, 924.5) * mm});
            skLineSegment(sketch, "E7.8.10.1", {"start": v(-390.5, 974.5) * mm, "end": v(-340.5, 974.5) * mm});
            skLineSegment(sketch, "E7.8.10.2", {"start": v(-390.5, 974.5) * mm, "end": v(-390.5, 924.5) * mm});
            skLineSegment(sketch, "E7.8.10.3", {"start": v(-390.5, 924.5) * mm, "end": v(-340.5, 924.5) * mm});
            skLineSegment(sketch, "E7.8.11.0", {"start": v(-340.5, 920.5) * mm, "end": v(-340.5, 870.5) * mm});
            skLineSegment(sketch, "E7.8.11.1", {"start": v(-390.5, 920.5) * mm, "end": v(-340.5, 920.5) * mm});
            skLineSegment(sketch, "E7.8.11.2", {"start": v(-390.5, 920.5) * mm, "end": v(-390.5, 870.5) * mm});
            skLineSegment(sketch, "E7.8.11.3", {"start": v(-390.5, 870.5) * mm, "end": v(-340.5, 870.5) * mm});
            skLineSegment(sketch, "E7.8.12.0", {"start": v(-340.5, 866.5) * mm, "end": v(-340.5, 816.5) * mm});
            skLineSegment(sketch, "E7.8.12.1", {"start": v(-390.5, 866.5) * mm, "end": v(-340.5, 866.5) * mm});
            skLineSegment(sketch, "E7.8.12.2", {"start": v(-390.5, 866.5) * mm, "end": v(-390.5, 816.5) * mm});
            skLineSegment(sketch, "E7.8.12.3", {"start": v(-390.5, 816.5) * mm, "end": v(-340.5, 816.5) * mm});
            skLineSegment(sketch, "E7.8.13.0", {"start": v(-340.5, 812.5) * mm, "end": v(-340.5, 762.5) * mm});
            skLineSegment(sketch, "E7.8.13.1", {"start": v(-390.5, 812.5) * mm, "end": v(-340.5, 812.5) * mm});
            skLineSegment(sketch, "E7.8.13.2", {"start": v(-390.5, 812.5) * mm, "end": v(-390.5, 762.5) * mm});
            skLineSegment(sketch, "E7.8.13.3", {"start": v(-390.5, 762.5) * mm, "end": v(-340.5, 762.5) * mm});
            skLineSegment(sketch, "E7.8.14.0", {"start": v(-340.5, 758.5) * mm, "end": v(-340.5, 708.5) * mm});
            skLineSegment(sketch, "E7.8.14.1", {"start": v(-390.5, 758.5) * mm, "end": v(-340.5, 758.5) * mm});
            skLineSegment(sketch, "E7.8.14.2", {"start": v(-390.5, 758.5) * mm, "end": v(-390.5, 708.5) * mm});
            skLineSegment(sketch, "E7.8.14.3", {"start": v(-390.5, 708.5) * mm, "end": v(-340.5, 708.5) * mm});
            skLineSegment(sketch, "E7.8.15.0", {"start": v(-340.5, 704.5) * mm, "end": v(-340.5, 654.5) * mm});
            skLineSegment(sketch, "E7.8.15.1", {"start": v(-390.5, 704.5) * mm, "end": v(-340.5, 704.5) * mm});
            skLineSegment(sketch, "E7.8.15.2", {"start": v(-390.5, 704.5) * mm, "end": v(-390.5, 654.5) * mm});
            skLineSegment(sketch, "E7.8.15.3", {"start": v(-390.5, 654.5) * mm, "end": v(-340.5, 654.5) * mm});
            skLineSegment(sketch, "E7.8.16.0", {"start": v(-340.5, 650.5) * mm, "end": v(-340.5, 600.5) * mm});
            skLineSegment(sketch, "E7.8.16.1", {"start": v(-390.5, 650.5) * mm, "end": v(-340.5, 650.5) * mm});
            skLineSegment(sketch, "E7.8.16.2", {"start": v(-390.5, 650.5) * mm, "end": v(-390.5, 600.5) * mm});
            skLineSegment(sketch, "E7.8.16.3", {"start": v(-390.5, 600.5) * mm, "end": v(-340.5, 600.5) * mm});
            skLineSegment(sketch, "E7.8.17.0", {"start": v(-340.5, 596.5) * mm, "end": v(-340.5, 546.5) * mm});
            skLineSegment(sketch, "E7.8.17.1", {"start": v(-390.5, 596.5) * mm, "end": v(-340.5, 596.5) * mm});
            skLineSegment(sketch, "E7.8.17.2", {"start": v(-390.5, 596.5) * mm, "end": v(-390.5, 546.5) * mm});
            skLineSegment(sketch, "E7.8.17.3", {"start": v(-390.5, 546.5) * mm, "end": v(-340.5, 546.5) * mm});
            skLineSegment(sketch, "E7.8.18.0", {"start": v(-340.5, 542.5) * mm, "end": v(-340.5, 492.5) * mm});
            skLineSegment(sketch, "E7.8.18.1", {"start": v(-390.5, 542.5) * mm, "end": v(-340.5, 542.5) * mm});
            skLineSegment(sketch, "E7.8.18.2", {"start": v(-390.5, 542.5) * mm, "end": v(-390.5, 492.5) * mm});
            skLineSegment(sketch, "E7.8.18.3", {"start": v(-390.5, 492.5) * mm, "end": v(-340.5, 492.5) * mm});
            skLineSegment(sketch, "E7.8.19.0", {"start": v(-340.5, 488.5) * mm, "end": v(-340.5, 438.5) * mm});
            skLineSegment(sketch, "E7.8.19.1", {"start": v(-390.5, 488.5) * mm, "end": v(-340.5, 488.5) * mm});
            skLineSegment(sketch, "E7.8.19.2", {"start": v(-390.5, 488.5) * mm, "end": v(-390.5, 438.5) * mm});
            skLineSegment(sketch, "E7.8.19.3", {"start": v(-390.5, 438.5) * mm, "end": v(-340.5, 438.5) * mm});
            skLineSegment(sketch, "E7.8.20.0", {"start": v(-340.5, 434.5) * mm, "end": v(-340.5, 384.5) * mm});
            skLineSegment(sketch, "E7.8.20.1", {"start": v(-390.5, 434.5) * mm, "end": v(-340.5, 434.5) * mm});
            skLineSegment(sketch, "E7.8.20.2", {"start": v(-390.5, 434.5) * mm, "end": v(-390.5, 384.5) * mm});
            skLineSegment(sketch, "E7.8.20.3", {"start": v(-390.5, 384.5) * mm, "end": v(-340.5, 384.5) * mm});
            skLineSegment(sketch, "E7.8.21.0", {"start": v(-340.5, 380.5) * mm, "end": v(-340.5, 330.5) * mm});
            skLineSegment(sketch, "E7.8.21.1", {"start": v(-390.5, 380.5) * mm, "end": v(-340.5, 380.5) * mm});
            skLineSegment(sketch, "E7.8.21.2", {"start": v(-390.5, 380.5) * mm, "end": v(-390.5, 330.5) * mm});
            skLineSegment(sketch, "E7.8.21.3", {"start": v(-390.5, 330.5) * mm, "end": v(-340.5, 330.5) * mm});
            skLineSegment(sketch, "E7.8.22.0", {"start": v(-340.5, 326.5) * mm, "end": v(-340.5, 276.5) * mm});
            skLineSegment(sketch, "E7.8.22.1", {"start": v(-390.5, 326.5) * mm, "end": v(-340.5, 326.5) * mm});
            skLineSegment(sketch, "E7.8.22.2", {"start": v(-390.5, 326.5) * mm, "end": v(-390.5, 276.5) * mm});
            skLineSegment(sketch, "E7.8.22.3", {"start": v(-390.5, 276.5) * mm, "end": v(-340.5, 276.5) * mm});
            skLineSegment(sketch, "E7.8.23.0", {"start": v(-340.5, 272.5) * mm, "end": v(-340.5, 222.5) * mm});
            skLineSegment(sketch, "E7.8.23.1", {"start": v(-390.5, 272.5) * mm, "end": v(-340.5, 272.5) * mm});
            skLineSegment(sketch, "E7.8.23.2", {"start": v(-390.5, 272.5) * mm, "end": v(-390.5, 222.5) * mm});
            skLineSegment(sketch, "E7.8.23.3", {"start": v(-390.5, 222.5) * mm, "end": v(-340.5, 222.5) * mm});
            skLineSegment(sketch, "E7.8.24.0", {"start": v(-340.5, 218.5) * mm, "end": v(-340.5, 168.5) * mm});
            skLineSegment(sketch, "E7.8.24.1", {"start": v(-390.5, 218.5) * mm, "end": v(-340.5, 218.5) * mm});
            skLineSegment(sketch, "E7.8.24.2", {"start": v(-390.5, 218.5) * mm, "end": v(-390.5, 168.5) * mm});
            skLineSegment(sketch, "E7.8.24.3", {"start": v(-390.5, 168.5) * mm, "end": v(-340.5, 168.5) * mm});
            skLineSegment(sketch, "E7.8.25.0", {"start": v(-340.5, 164.5) * mm, "end": v(-340.5, 114.5) * mm});
            skLineSegment(sketch, "E7.8.25.1", {"start": v(-390.5, 164.5) * mm, "end": v(-340.5, 164.5) * mm});
            skLineSegment(sketch, "E7.8.25.2", {"start": v(-390.5, 164.5) * mm, "end": v(-390.5, 114.5) * mm});
            skLineSegment(sketch, "E7.8.25.3", {"start": v(-390.5, 114.5) * mm, "end": v(-340.5, 114.5) * mm});
            skLineSegment(sketch, "E7.8.26.0", {"start": v(-340.5, 110.5) * mm, "end": v(-340.5, 60.5) * mm});
            skLineSegment(sketch, "E7.8.26.1", {"start": v(-390.5, 110.5) * mm, "end": v(-340.5, 110.5) * mm});
            skLineSegment(sketch, "E7.8.26.2", {"start": v(-390.5, 110.5) * mm, "end": v(-390.5, 60.5) * mm});
            skLineSegment(sketch, "E7.8.26.3", {"start": v(-390.5, 60.5) * mm, "end": v(-340.5, 60.5) * mm});
            skLineSegment(sketch, "E7.8.27.0", {"start": v(-340.5, 56.5) * mm, "end": v(-340.5, 6.5) * mm});
            skLineSegment(sketch, "E7.8.27.1", {"start": v(-390.5, 56.5) * mm, "end": v(-340.5, 56.5) * mm});
            skLineSegment(sketch, "E7.8.27.2", {"start": v(-390.5, 56.5) * mm, "end": v(-390.5, 6.5) * mm});
            skLineSegment(sketch, "E7.8.27.3", {"start": v(-390.5, 6.5) * mm, "end": v(-340.5, 6.5) * mm});
            skLineSegment(sketch, "E7.9.0.0", {"start": v(-286.5, 1514.5) * mm, "end": v(-286.5, 1464.5) * mm});
            skLineSegment(sketch, "E7.9.0.1", {"start": v(-336.5, 1514.5) * mm, "end": v(-286.5, 1514.5) * mm});
            skLineSegment(sketch, "E7.9.0.2", {"start": v(-336.5, 1514.5) * mm, "end": v(-336.5, 1464.5) * mm});
            skLineSegment(sketch, "E7.9.0.3", {"start": v(-336.5, 1464.5) * mm, "end": v(-286.5, 1464.5) * mm});
            skLineSegment(sketch, "E7.9.1.0", {"start": v(-286.5, 1460.5) * mm, "end": v(-286.5, 1410.5) * mm});
            skLineSegment(sketch, "E7.9.1.1", {"start": v(-336.5, 1460.5) * mm, "end": v(-286.5, 1460.5) * mm});
            skLineSegment(sketch, "E7.9.1.2", {"start": v(-336.5, 1460.5) * mm, "end": v(-336.5, 1410.5) * mm});
            skLineSegment(sketch, "E7.9.1.3", {"start": v(-336.5, 1410.5) * mm, "end": v(-286.5, 1410.5) * mm});
            skLineSegment(sketch, "E7.9.2.0", {"start": v(-286.5, 1406.5) * mm, "end": v(-286.5, 1356.5) * mm});
            skLineSegment(sketch, "E7.9.2.1", {"start": v(-336.5, 1406.5) * mm, "end": v(-286.5, 1406.5) * mm});
            skLineSegment(sketch, "E7.9.2.2", {"start": v(-336.5, 1406.5) * mm, "end": v(-336.5, 1356.5) * mm});
            skLineSegment(sketch, "E7.9.2.3", {"start": v(-336.5, 1356.5) * mm, "end": v(-286.5, 1356.5) * mm});
            skLineSegment(sketch, "E7.9.3.0", {"start": v(-286.5, 1352.5) * mm, "end": v(-286.5, 1302.5) * mm});
            skLineSegment(sketch, "E7.9.3.1", {"start": v(-336.5, 1352.5) * mm, "end": v(-286.5, 1352.5) * mm});
            skLineSegment(sketch, "E7.9.3.2", {"start": v(-336.5, 1352.5) * mm, "end": v(-336.5, 1302.5) * mm});
            skLineSegment(sketch, "E7.9.3.3", {"start": v(-336.5, 1302.5) * mm, "end": v(-286.5, 1302.5) * mm});
            skLineSegment(sketch, "E7.9.4.0", {"start": v(-286.5, 1298.5) * mm, "end": v(-286.5, 1248.5) * mm});
            skLineSegment(sketch, "E7.9.4.1", {"start": v(-336.5, 1298.5) * mm, "end": v(-286.5, 1298.5) * mm});
            skLineSegment(sketch, "E7.9.4.2", {"start": v(-336.5, 1298.5) * mm, "end": v(-336.5, 1248.5) * mm});
            skLineSegment(sketch, "E7.9.4.3", {"start": v(-336.5, 1248.5) * mm, "end": v(-286.5, 1248.5) * mm});
            skLineSegment(sketch, "E7.9.5.0", {"start": v(-286.5, 1244.5) * mm, "end": v(-286.5, 1194.5) * mm});
            skLineSegment(sketch, "E7.9.5.1", {"start": v(-336.5, 1244.5) * mm, "end": v(-286.5, 1244.5) * mm});
            skLineSegment(sketch, "E7.9.5.2", {"start": v(-336.5, 1244.5) * mm, "end": v(-336.5, 1194.5) * mm});
            skLineSegment(sketch, "E7.9.5.3", {"start": v(-336.5, 1194.5) * mm, "end": v(-286.5, 1194.5) * mm});
            skLineSegment(sketch, "E7.9.6.0", {"start": v(-286.5, 1190.5) * mm, "end": v(-286.5, 1140.5) * mm});
            skLineSegment(sketch, "E7.9.6.1", {"start": v(-336.5, 1190.5) * mm, "end": v(-286.5, 1190.5) * mm});
            skLineSegment(sketch, "E7.9.6.2", {"start": v(-336.5, 1190.5) * mm, "end": v(-336.5, 1140.5) * mm});
            skLineSegment(sketch, "E7.9.6.3", {"start": v(-336.5, 1140.5) * mm, "end": v(-286.5, 1140.5) * mm});
            skLineSegment(sketch, "E7.9.7.0", {"start": v(-286.5, 1136.5) * mm, "end": v(-286.5, 1086.5) * mm});
            skLineSegment(sketch, "E7.9.7.1", {"start": v(-336.5, 1136.5) * mm, "end": v(-286.5, 1136.5) * mm});
            skLineSegment(sketch, "E7.9.7.2", {"start": v(-336.5, 1136.5) * mm, "end": v(-336.5, 1086.5) * mm});
            skLineSegment(sketch, "E7.9.7.3", {"start": v(-336.5, 1086.5) * mm, "end": v(-286.5, 1086.5) * mm});
            skLineSegment(sketch, "E7.9.8.0", {"start": v(-286.5, 1082.5) * mm, "end": v(-286.5, 1032.5) * mm});
            skLineSegment(sketch, "E7.9.8.1", {"start": v(-336.5, 1082.5) * mm, "end": v(-286.5, 1082.5) * mm});
            skLineSegment(sketch, "E7.9.8.2", {"start": v(-336.5, 1082.5) * mm, "end": v(-336.5, 1032.5) * mm});
            skLineSegment(sketch, "E7.9.8.3", {"start": v(-336.5, 1032.5) * mm, "end": v(-286.5, 1032.5) * mm});
            skLineSegment(sketch, "E7.9.9.0", {"start": v(-286.5, 1028.5) * mm, "end": v(-286.5, 978.5) * mm});
            skLineSegment(sketch, "E7.9.9.1", {"start": v(-336.5, 1028.5) * mm, "end": v(-286.5, 1028.5) * mm});
            skLineSegment(sketch, "E7.9.9.2", {"start": v(-336.5, 1028.5) * mm, "end": v(-336.5, 978.5) * mm});
            skLineSegment(sketch, "E7.9.9.3", {"start": v(-336.5, 978.5) * mm, "end": v(-286.5, 978.5) * mm});
            skLineSegment(sketch, "E7.9.10.0", {"start": v(-286.5, 974.5) * mm, "end": v(-286.5, 924.5) * mm});
            skLineSegment(sketch, "E7.9.10.1", {"start": v(-336.5, 974.5) * mm, "end": v(-286.5, 974.5) * mm});
            skLineSegment(sketch, "E7.9.10.2", {"start": v(-336.5, 974.5) * mm, "end": v(-336.5, 924.5) * mm});
            skLineSegment(sketch, "E7.9.10.3", {"start": v(-336.5, 924.5) * mm, "end": v(-286.5, 924.5) * mm});
            skLineSegment(sketch, "E7.9.11.0", {"start": v(-286.5, 920.5) * mm, "end": v(-286.5, 870.5) * mm});
            skLineSegment(sketch, "E7.9.11.1", {"start": v(-336.5, 920.5) * mm, "end": v(-286.5, 920.5) * mm});
            skLineSegment(sketch, "E7.9.11.2", {"start": v(-336.5, 920.5) * mm, "end": v(-336.5, 870.5) * mm});
            skLineSegment(sketch, "E7.9.11.3", {"start": v(-336.5, 870.5) * mm, "end": v(-286.5, 870.5) * mm});
            skLineSegment(sketch, "E7.9.12.0", {"start": v(-286.5, 866.5) * mm, "end": v(-286.5, 816.5) * mm});
            skLineSegment(sketch, "E7.9.12.1", {"start": v(-336.5, 866.5) * mm, "end": v(-286.5, 866.5) * mm});
            skLineSegment(sketch, "E7.9.12.2", {"start": v(-336.5, 866.5) * mm, "end": v(-336.5, 816.5) * mm});
            skLineSegment(sketch, "E7.9.12.3", {"start": v(-336.5, 816.5) * mm, "end": v(-286.5, 816.5) * mm});
            skLineSegment(sketch, "E7.9.13.0", {"start": v(-286.5, 812.5) * mm, "end": v(-286.5, 762.5) * mm});
            skLineSegment(sketch, "E7.9.13.1", {"start": v(-336.5, 812.5) * mm, "end": v(-286.5, 812.5) * mm});
            skLineSegment(sketch, "E7.9.13.2", {"start": v(-336.5, 812.5) * mm, "end": v(-336.5, 762.5) * mm});
            skLineSegment(sketch, "E7.9.13.3", {"start": v(-336.5, 762.5) * mm, "end": v(-286.5, 762.5) * mm});
            skLineSegment(sketch, "E7.9.14.0", {"start": v(-286.5, 758.5) * mm, "end": v(-286.5, 708.5) * mm});
            skLineSegment(sketch, "E7.9.14.1", {"start": v(-336.5, 758.5) * mm, "end": v(-286.5, 758.5) * mm});
            skLineSegment(sketch, "E7.9.14.2", {"start": v(-336.5, 758.5) * mm, "end": v(-336.5, 708.5) * mm});
            skLineSegment(sketch, "E7.9.14.3", {"start": v(-336.5, 708.5) * mm, "end": v(-286.5, 708.5) * mm});
            skLineSegment(sketch, "E7.9.15.0", {"start": v(-286.5, 704.5) * mm, "end": v(-286.5, 654.5) * mm});
            skLineSegment(sketch, "E7.9.15.1", {"start": v(-336.5, 704.5) * mm, "end": v(-286.5, 704.5) * mm});
            skLineSegment(sketch, "E7.9.15.2", {"start": v(-336.5, 704.5) * mm, "end": v(-336.5, 654.5) * mm});
            skLineSegment(sketch, "E7.9.15.3", {"start": v(-336.5, 654.5) * mm, "end": v(-286.5, 654.5) * mm});
            skLineSegment(sketch, "E7.9.16.0", {"start": v(-286.5, 650.5) * mm, "end": v(-286.5, 600.5) * mm});
            skLineSegment(sketch, "E7.9.16.1", {"start": v(-336.5, 650.5) * mm, "end": v(-286.5, 650.5) * mm});
            skLineSegment(sketch, "E7.9.16.2", {"start": v(-336.5, 650.5) * mm, "end": v(-336.5, 600.5) * mm});
            skLineSegment(sketch, "E7.9.16.3", {"start": v(-336.5, 600.5) * mm, "end": v(-286.5, 600.5) * mm});
            skLineSegment(sketch, "E7.9.17.0", {"start": v(-286.5, 596.5) * mm, "end": v(-286.5, 546.5) * mm});
            skLineSegment(sketch, "E7.9.17.1", {"start": v(-336.5, 596.5) * mm, "end": v(-286.5, 596.5) * mm});
            skLineSegment(sketch, "E7.9.17.2", {"start": v(-336.5, 596.5) * mm, "end": v(-336.5, 546.5) * mm});
            skLineSegment(sketch, "E7.9.17.3", {"start": v(-336.5, 546.5) * mm, "end": v(-286.5, 546.5) * mm});
            skLineSegment(sketch, "E7.9.18.0", {"start": v(-286.5, 542.5) * mm, "end": v(-286.5, 492.5) * mm});
            skLineSegment(sketch, "E7.9.18.1", {"start": v(-336.5, 542.5) * mm, "end": v(-286.5, 542.5) * mm});
            skLineSegment(sketch, "E7.9.18.2", {"start": v(-336.5, 542.5) * mm, "end": v(-336.5, 492.5) * mm});
            skLineSegment(sketch, "E7.9.18.3", {"start": v(-336.5, 492.5) * mm, "end": v(-286.5, 492.5) * mm});
            skLineSegment(sketch, "E7.9.19.0", {"start": v(-286.5, 488.5) * mm, "end": v(-286.5, 438.5) * mm});
            skLineSegment(sketch, "E7.9.19.1", {"start": v(-336.5, 488.5) * mm, "end": v(-286.5, 488.5) * mm});
            skLineSegment(sketch, "E7.9.19.2", {"start": v(-336.5, 488.5) * mm, "end": v(-336.5, 438.5) * mm});
            skLineSegment(sketch, "E7.9.19.3", {"start": v(-336.5, 438.5) * mm, "end": v(-286.5, 438.5) * mm});
            skLineSegment(sketch, "E7.9.20.0", {"start": v(-286.5, 434.5) * mm, "end": v(-286.5, 384.5) * mm});
            skLineSegment(sketch, "E7.9.20.1", {"start": v(-336.5, 434.5) * mm, "end": v(-286.5, 434.5) * mm});
            skLineSegment(sketch, "E7.9.20.2", {"start": v(-336.5, 434.5) * mm, "end": v(-336.5, 384.5) * mm});
            skLineSegment(sketch, "E7.9.20.3", {"start": v(-336.5, 384.5) * mm, "end": v(-286.5, 384.5) * mm});
            skLineSegment(sketch, "E7.9.21.0", {"start": v(-286.5, 380.5) * mm, "end": v(-286.5, 330.5) * mm});
            skLineSegment(sketch, "E7.9.21.1", {"start": v(-336.5, 380.5) * mm, "end": v(-286.5, 380.5) * mm});
            skLineSegment(sketch, "E7.9.21.2", {"start": v(-336.5, 380.5) * mm, "end": v(-336.5, 330.5) * mm});
            skLineSegment(sketch, "E7.9.21.3", {"start": v(-336.5, 330.5) * mm, "end": v(-286.5, 330.5) * mm});
            skLineSegment(sketch, "E7.9.22.0", {"start": v(-286.5, 326.5) * mm, "end": v(-286.5, 276.5) * mm});
            skLineSegment(sketch, "E7.9.22.1", {"start": v(-336.5, 326.5) * mm, "end": v(-286.5, 326.5) * mm});
            skLineSegment(sketch, "E7.9.22.2", {"start": v(-336.5, 326.5) * mm, "end": v(-336.5, 276.5) * mm});
            skLineSegment(sketch, "E7.9.22.3", {"start": v(-336.5, 276.5) * mm, "end": v(-286.5, 276.5) * mm});
            skLineSegment(sketch, "E7.9.23.0", {"start": v(-286.5, 272.5) * mm, "end": v(-286.5, 222.5) * mm});
            skLineSegment(sketch, "E7.9.23.1", {"start": v(-336.5, 272.5) * mm, "end": v(-286.5, 272.5) * mm});
            skLineSegment(sketch, "E7.9.23.2", {"start": v(-336.5, 272.5) * mm, "end": v(-336.5, 222.5) * mm});
            skLineSegment(sketch, "E7.9.23.3", {"start": v(-336.5, 222.5) * mm, "end": v(-286.5, 222.5) * mm});
            skLineSegment(sketch, "E7.9.24.0", {"start": v(-286.5, 218.5) * mm, "end": v(-286.5, 168.5) * mm});
            skLineSegment(sketch, "E7.9.24.1", {"start": v(-336.5, 218.5) * mm, "end": v(-286.5, 218.5) * mm});
            skLineSegment(sketch, "E7.9.24.2", {"start": v(-336.5, 218.5) * mm, "end": v(-336.5, 168.5) * mm});
            skLineSegment(sketch, "E7.9.24.3", {"start": v(-336.5, 168.5) * mm, "end": v(-286.5, 168.5) * mm});
            skLineSegment(sketch, "E7.9.25.0", {"start": v(-286.5, 164.5) * mm, "end": v(-286.5, 114.5) * mm});
            skLineSegment(sketch, "E7.9.25.1", {"start": v(-336.5, 164.5) * mm, "end": v(-286.5, 164.5) * mm});
            skLineSegment(sketch, "E7.9.25.2", {"start": v(-336.5, 164.5) * mm, "end": v(-336.5, 114.5) * mm});
            skLineSegment(sketch, "E7.9.25.3", {"start": v(-336.5, 114.5) * mm, "end": v(-286.5, 114.5) * mm});
            skLineSegment(sketch, "E7.9.26.0", {"start": v(-286.5, 110.5) * mm, "end": v(-286.5, 60.5) * mm});
            skLineSegment(sketch, "E7.9.26.1", {"start": v(-336.5, 110.5) * mm, "end": v(-286.5, 110.5) * mm});
            skLineSegment(sketch, "E7.9.26.2", {"start": v(-336.5, 110.5) * mm, "end": v(-336.5, 60.5) * mm});
            skLineSegment(sketch, "E7.9.26.3", {"start": v(-336.5, 60.5) * mm, "end": v(-286.5, 60.5) * mm});
            skLineSegment(sketch, "E7.9.27.0", {"start": v(-286.5, 56.5) * mm, "end": v(-286.5, 6.5) * mm});
            skLineSegment(sketch, "E7.9.27.1", {"start": v(-336.5, 56.5) * mm, "end": v(-286.5, 56.5) * mm});
            skLineSegment(sketch, "E7.9.27.2", {"start": v(-336.5, 56.5) * mm, "end": v(-336.5, 6.5) * mm});
            skLineSegment(sketch, "E7.9.27.3", {"start": v(-336.5, 6.5) * mm, "end": v(-286.5, 6.5) * mm});
            skLineSegment(sketch, "E7.10.0.0", {"start": v(-232.5, 1514.5) * mm, "end": v(-232.5, 1464.5) * mm});
            skLineSegment(sketch, "E7.10.0.1", {"start": v(-282.5, 1514.5) * mm, "end": v(-232.5, 1514.5) * mm});
            skLineSegment(sketch, "E7.10.0.2", {"start": v(-282.5, 1514.5) * mm, "end": v(-282.5, 1464.5) * mm});
            skLineSegment(sketch, "E7.10.0.3", {"start": v(-282.5, 1464.5) * mm, "end": v(-232.5, 1464.5) * mm});
            skLineSegment(sketch, "E7.10.1.0", {"start": v(-232.5, 1460.5) * mm, "end": v(-232.5, 1410.5) * mm});
            skLineSegment(sketch, "E7.10.1.1", {"start": v(-282.5, 1460.5) * mm, "end": v(-232.5, 1460.5) * mm});
            skLineSegment(sketch, "E7.10.1.2", {"start": v(-282.5, 1460.5) * mm, "end": v(-282.5, 1410.5) * mm});
            skLineSegment(sketch, "E7.10.1.3", {"start": v(-282.5, 1410.5) * mm, "end": v(-232.5, 1410.5) * mm});
            skLineSegment(sketch, "E7.10.2.0", {"start": v(-232.5, 1406.5) * mm, "end": v(-232.5, 1356.5) * mm});
            skLineSegment(sketch, "E7.10.2.1", {"start": v(-282.5, 1406.5) * mm, "end": v(-232.5, 1406.5) * mm});
            skLineSegment(sketch, "E7.10.2.2", {"start": v(-282.5, 1406.5) * mm, "end": v(-282.5, 1356.5) * mm});
            skLineSegment(sketch, "E7.10.2.3", {"start": v(-282.5, 1356.5) * mm, "end": v(-232.5, 1356.5) * mm});
            skLineSegment(sketch, "E7.10.3.0", {"start": v(-232.5, 1352.5) * mm, "end": v(-232.5, 1302.5) * mm});
            skLineSegment(sketch, "E7.10.3.1", {"start": v(-282.5, 1352.5) * mm, "end": v(-232.5, 1352.5) * mm});
            skLineSegment(sketch, "E7.10.3.2", {"start": v(-282.5, 1352.5) * mm, "end": v(-282.5, 1302.5) * mm});
            skLineSegment(sketch, "E7.10.3.3", {"start": v(-282.5, 1302.5) * mm, "end": v(-232.5, 1302.5) * mm});
            skLineSegment(sketch, "E7.10.4.0", {"start": v(-232.5, 1298.5) * mm, "end": v(-232.5, 1248.5) * mm});
            skLineSegment(sketch, "E7.10.4.1", {"start": v(-282.5, 1298.5) * mm, "end": v(-232.5, 1298.5) * mm});
            skLineSegment(sketch, "E7.10.4.2", {"start": v(-282.5, 1298.5) * mm, "end": v(-282.5, 1248.5) * mm});
            skLineSegment(sketch, "E7.10.4.3", {"start": v(-282.5, 1248.5) * mm, "end": v(-232.5, 1248.5) * mm});
            skLineSegment(sketch, "E7.10.5.0", {"start": v(-232.5, 1244.5) * mm, "end": v(-232.5, 1194.5) * mm});
            skLineSegment(sketch, "E7.10.5.1", {"start": v(-282.5, 1244.5) * mm, "end": v(-232.5, 1244.5) * mm});
            skLineSegment(sketch, "E7.10.5.2", {"start": v(-282.5, 1244.5) * mm, "end": v(-282.5, 1194.5) * mm});
            skLineSegment(sketch, "E7.10.5.3", {"start": v(-282.5, 1194.5) * mm, "end": v(-232.5, 1194.5) * mm});
            skLineSegment(sketch, "E7.10.6.0", {"start": v(-232.5, 1190.5) * mm, "end": v(-232.5, 1140.5) * mm});
            skLineSegment(sketch, "E7.10.6.1", {"start": v(-282.5, 1190.5) * mm, "end": v(-232.5, 1190.5) * mm});
            skLineSegment(sketch, "E7.10.6.2", {"start": v(-282.5, 1190.5) * mm, "end": v(-282.5, 1140.5) * mm});
            skLineSegment(sketch, "E7.10.6.3", {"start": v(-282.5, 1140.5) * mm, "end": v(-232.5, 1140.5) * mm});
            skLineSegment(sketch, "E7.10.7.0", {"start": v(-232.5, 1136.5) * mm, "end": v(-232.5, 1086.5) * mm});
            skLineSegment(sketch, "E7.10.7.1", {"start": v(-282.5, 1136.5) * mm, "end": v(-232.5, 1136.5) * mm});
            skLineSegment(sketch, "E7.10.7.2", {"start": v(-282.5, 1136.5) * mm, "end": v(-282.5, 1086.5) * mm});
            skLineSegment(sketch, "E7.10.7.3", {"start": v(-282.5, 1086.5) * mm, "end": v(-232.5, 1086.5) * mm});
            skLineSegment(sketch, "E7.10.8.0", {"start": v(-232.5, 1082.5) * mm, "end": v(-232.5, 1032.5) * mm});
            skLineSegment(sketch, "E7.10.8.1", {"start": v(-282.5, 1082.5) * mm, "end": v(-232.5, 1082.5) * mm});
            skLineSegment(sketch, "E7.10.8.2", {"start": v(-282.5, 1082.5) * mm, "end": v(-282.5, 1032.5) * mm});
            skLineSegment(sketch, "E7.10.8.3", {"start": v(-282.5, 1032.5) * mm, "end": v(-232.5, 1032.5) * mm});
            skLineSegment(sketch, "E7.10.9.0", {"start": v(-232.5, 1028.5) * mm, "end": v(-232.5, 978.5) * mm});
            skLineSegment(sketch, "E7.10.9.1", {"start": v(-282.5, 1028.5) * mm, "end": v(-232.5, 1028.5) * mm});
            skLineSegment(sketch, "E7.10.9.2", {"start": v(-282.5, 1028.5) * mm, "end": v(-282.5, 978.5) * mm});
            skLineSegment(sketch, "E7.10.9.3", {"start": v(-282.5, 978.5) * mm, "end": v(-232.5, 978.5) * mm});
            skLineSegment(sketch, "E7.10.10.0", {"start": v(-232.5, 974.5) * mm, "end": v(-232.5, 924.5) * mm});
            skLineSegment(sketch, "E7.10.10.1", {"start": v(-282.5, 974.5) * mm, "end": v(-232.5, 974.5) * mm});
            skLineSegment(sketch, "E7.10.10.2", {"start": v(-282.5, 974.5) * mm, "end": v(-282.5, 924.5) * mm});
            skLineSegment(sketch, "E7.10.10.3", {"start": v(-282.5, 924.5) * mm, "end": v(-232.5, 924.5) * mm});
            skLineSegment(sketch, "E7.10.11.0", {"start": v(-232.5, 920.5) * mm, "end": v(-232.5, 870.5) * mm});
            skLineSegment(sketch, "E7.10.11.1", {"start": v(-282.5, 920.5) * mm, "end": v(-232.5, 920.5) * mm});
            skLineSegment(sketch, "E7.10.11.2", {"start": v(-282.5, 920.5) * mm, "end": v(-282.5, 870.5) * mm});
            skLineSegment(sketch, "E7.10.11.3", {"start": v(-282.5, 870.5) * mm, "end": v(-232.5, 870.5) * mm});
            skLineSegment(sketch, "E7.10.12.0", {"start": v(-232.5, 866.5) * mm, "end": v(-232.5, 816.5) * mm});
            skLineSegment(sketch, "E7.10.12.1", {"start": v(-282.5, 866.5) * mm, "end": v(-232.5, 866.5) * mm});
            skLineSegment(sketch, "E7.10.12.2", {"start": v(-282.5, 866.5) * mm, "end": v(-282.5, 816.5) * mm});
            skLineSegment(sketch, "E7.10.12.3", {"start": v(-282.5, 816.5) * mm, "end": v(-232.5, 816.5) * mm});
            skLineSegment(sketch, "E7.10.13.0", {"start": v(-232.5, 812.5) * mm, "end": v(-232.5, 762.5) * mm});
            skLineSegment(sketch, "E7.10.13.1", {"start": v(-282.5, 812.5) * mm, "end": v(-232.5, 812.5) * mm});
            skLineSegment(sketch, "E7.10.13.2", {"start": v(-282.5, 812.5) * mm, "end": v(-282.5, 762.5) * mm});
            skLineSegment(sketch, "E7.10.13.3", {"start": v(-282.5, 762.5) * mm, "end": v(-232.5, 762.5) * mm});
            skLineSegment(sketch, "E7.10.14.0", {"start": v(-232.5, 758.5) * mm, "end": v(-232.5, 708.5) * mm});
            skLineSegment(sketch, "E7.10.14.1", {"start": v(-282.5, 758.5) * mm, "end": v(-232.5, 758.5) * mm});
            skLineSegment(sketch, "E7.10.14.2", {"start": v(-282.5, 758.5) * mm, "end": v(-282.5, 708.5) * mm});
            skLineSegment(sketch, "E7.10.14.3", {"start": v(-282.5, 708.5) * mm, "end": v(-232.5, 708.5) * mm});
            skLineSegment(sketch, "E7.10.15.0", {"start": v(-232.5, 704.5) * mm, "end": v(-232.5, 654.5) * mm});
            skLineSegment(sketch, "E7.10.15.1", {"start": v(-282.5, 704.5) * mm, "end": v(-232.5, 704.5) * mm});
            skLineSegment(sketch, "E7.10.15.2", {"start": v(-282.5, 704.5) * mm, "end": v(-282.5, 654.5) * mm});
            skLineSegment(sketch, "E7.10.15.3", {"start": v(-282.5, 654.5) * mm, "end": v(-232.5, 654.5) * mm});
            skLineSegment(sketch, "E7.10.16.0", {"start": v(-232.5, 650.5) * mm, "end": v(-232.5, 600.5) * mm});
            skLineSegment(sketch, "E7.10.16.1", {"start": v(-282.5, 650.5) * mm, "end": v(-232.5, 650.5) * mm});
            skLineSegment(sketch, "E7.10.16.2", {"start": v(-282.5, 650.5) * mm, "end": v(-282.5, 600.5) * mm});
            skLineSegment(sketch, "E7.10.16.3", {"start": v(-282.5, 600.5) * mm, "end": v(-232.5, 600.5) * mm});
            skLineSegment(sketch, "E7.10.17.0", {"start": v(-232.5, 596.5) * mm, "end": v(-232.5, 546.5) * mm});
            skLineSegment(sketch, "E7.10.17.1", {"start": v(-282.5, 596.5) * mm, "end": v(-232.5, 596.5) * mm});
            skLineSegment(sketch, "E7.10.17.2", {"start": v(-282.5, 596.5) * mm, "end": v(-282.5, 546.5) * mm});
            skLineSegment(sketch, "E7.10.17.3", {"start": v(-282.5, 546.5) * mm, "end": v(-232.5, 546.5) * mm});
            skLineSegment(sketch, "E7.10.18.0", {"start": v(-232.5, 542.5) * mm, "end": v(-232.5, 492.5) * mm});
            skLineSegment(sketch, "E7.10.18.1", {"start": v(-282.5, 542.5) * mm, "end": v(-232.5, 542.5) * mm});
            skLineSegment(sketch, "E7.10.18.2", {"start": v(-282.5, 542.5) * mm, "end": v(-282.5, 492.5) * mm});
            skLineSegment(sketch, "E7.10.18.3", {"start": v(-282.5, 492.5) * mm, "end": v(-232.5, 492.5) * mm});
            skLineSegment(sketch, "E7.10.19.0", {"start": v(-232.5, 488.5) * mm, "end": v(-232.5, 438.5) * mm});
            skLineSegment(sketch, "E7.10.19.1", {"start": v(-282.5, 488.5) * mm, "end": v(-232.5, 488.5) * mm});
            skLineSegment(sketch, "E7.10.19.2", {"start": v(-282.5, 488.5) * mm, "end": v(-282.5, 438.5) * mm});
            skLineSegment(sketch, "E7.10.19.3", {"start": v(-282.5, 438.5) * mm, "end": v(-232.5, 438.5) * mm});
            skLineSegment(sketch, "E7.10.20.0", {"start": v(-232.5, 434.5) * mm, "end": v(-232.5, 384.5) * mm});
            skLineSegment(sketch, "E7.10.20.1", {"start": v(-282.5, 434.5) * mm, "end": v(-232.5, 434.5) * mm});
            skLineSegment(sketch, "E7.10.20.2", {"start": v(-282.5, 434.5) * mm, "end": v(-282.5, 384.5) * mm});
            skLineSegment(sketch, "E7.10.20.3", {"start": v(-282.5, 384.5) * mm, "end": v(-232.5, 384.5) * mm});
            skLineSegment(sketch, "E7.10.21.0", {"start": v(-232.5, 380.5) * mm, "end": v(-232.5, 330.5) * mm});
            skLineSegment(sketch, "E7.10.21.1", {"start": v(-282.5, 380.5) * mm, "end": v(-232.5, 380.5) * mm});
            skLineSegment(sketch, "E7.10.21.2", {"start": v(-282.5, 380.5) * mm, "end": v(-282.5, 330.5) * mm});
            skLineSegment(sketch, "E7.10.21.3", {"start": v(-282.5, 330.5) * mm, "end": v(-232.5, 330.5) * mm});
            skLineSegment(sketch, "E7.10.22.0", {"start": v(-232.5, 326.5) * mm, "end": v(-232.5, 276.5) * mm});
            skLineSegment(sketch, "E7.10.22.1", {"start": v(-282.5, 326.5) * mm, "end": v(-232.5, 326.5) * mm});
            skLineSegment(sketch, "E7.10.22.2", {"start": v(-282.5, 326.5) * mm, "end": v(-282.5, 276.5) * mm});
            skLineSegment(sketch, "E7.10.22.3", {"start": v(-282.5, 276.5) * mm, "end": v(-232.5, 276.5) * mm});
            skLineSegment(sketch, "E7.10.23.0", {"start": v(-232.5, 272.5) * mm, "end": v(-232.5, 222.5) * mm});
            skLineSegment(sketch, "E7.10.23.1", {"start": v(-282.5, 272.5) * mm, "end": v(-232.5, 272.5) * mm});
            skLineSegment(sketch, "E7.10.23.2", {"start": v(-282.5, 272.5) * mm, "end": v(-282.5, 222.5) * mm});
            skLineSegment(sketch, "E7.10.23.3", {"start": v(-282.5, 222.5) * mm, "end": v(-232.5, 222.5) * mm});
            skLineSegment(sketch, "E7.10.24.0", {"start": v(-232.5, 218.5) * mm, "end": v(-232.5, 168.5) * mm});
            skLineSegment(sketch, "E7.10.24.1", {"start": v(-282.5, 218.5) * mm, "end": v(-232.5, 218.5) * mm});
            skLineSegment(sketch, "E7.10.24.2", {"start": v(-282.5, 218.5) * mm, "end": v(-282.5, 168.5) * mm});
            skLineSegment(sketch, "E7.10.24.3", {"start": v(-282.5, 168.5) * mm, "end": v(-232.5, 168.5) * mm});
            skLineSegment(sketch, "E7.10.25.0", {"start": v(-232.5, 164.5) * mm, "end": v(-232.5, 114.5) * mm});
            skLineSegment(sketch, "E7.10.25.1", {"start": v(-282.5, 164.5) * mm, "end": v(-232.5, 164.5) * mm});
            skLineSegment(sketch, "E7.10.25.2", {"start": v(-282.5, 164.5) * mm, "end": v(-282.5, 114.5) * mm});
            skLineSegment(sketch, "E7.10.25.3", {"start": v(-282.5, 114.5) * mm, "end": v(-232.5, 114.5) * mm});
            skLineSegment(sketch, "E7.10.26.0", {"start": v(-232.5, 110.5) * mm, "end": v(-232.5, 60.5) * mm});
            skLineSegment(sketch, "E7.10.26.1", {"start": v(-282.5, 110.5) * mm, "end": v(-232.5, 110.5) * mm});
            skLineSegment(sketch, "E7.10.26.2", {"start": v(-282.5, 110.5) * mm, "end": v(-282.5, 60.5) * mm});
            skLineSegment(sketch, "E7.10.26.3", {"start": v(-282.5, 60.5) * mm, "end": v(-232.5, 60.5) * mm});
            skLineSegment(sketch, "E7.10.27.0", {"start": v(-232.5, 56.5) * mm, "end": v(-232.5, 6.5) * mm});
            skLineSegment(sketch, "E7.10.27.1", {"start": v(-282.5, 56.5) * mm, "end": v(-232.5, 56.5) * mm});
            skLineSegment(sketch, "E7.10.27.2", {"start": v(-282.5, 56.5) * mm, "end": v(-282.5, 6.5) * mm});
            skLineSegment(sketch, "E7.10.27.3", {"start": v(-282.5, 6.5) * mm, "end": v(-232.5, 6.5) * mm});
            skLineSegment(sketch, "E7.11.0.0", {"start": v(-178.5, 1514.5) * mm, "end": v(-178.5, 1464.5) * mm});
            skLineSegment(sketch, "E7.11.0.1", {"start": v(-228.5, 1514.5) * mm, "end": v(-178.5, 1514.5) * mm});
            skLineSegment(sketch, "E7.11.0.2", {"start": v(-228.5, 1514.5) * mm, "end": v(-228.5, 1464.5) * mm});
            skLineSegment(sketch, "E7.11.0.3", {"start": v(-228.5, 1464.5) * mm, "end": v(-178.5, 1464.5) * mm});
            skLineSegment(sketch, "E7.11.1.0", {"start": v(-178.5, 1460.5) * mm, "end": v(-178.5, 1410.5) * mm});
            skLineSegment(sketch, "E7.11.1.1", {"start": v(-228.5, 1460.5) * mm, "end": v(-178.5, 1460.5) * mm});
            skLineSegment(sketch, "E7.11.1.2", {"start": v(-228.5, 1460.5) * mm, "end": v(-228.5, 1410.5) * mm});
            skLineSegment(sketch, "E7.11.1.3", {"start": v(-228.5, 1410.5) * mm, "end": v(-178.5, 1410.5) * mm});
            skLineSegment(sketch, "E7.11.2.0", {"start": v(-178.5, 1406.5) * mm, "end": v(-178.5, 1356.5) * mm});
            skLineSegment(sketch, "E7.11.2.1", {"start": v(-228.5, 1406.5) * mm, "end": v(-178.5, 1406.5) * mm});
            skLineSegment(sketch, "E7.11.2.2", {"start": v(-228.5, 1406.5) * mm, "end": v(-228.5, 1356.5) * mm});
            skLineSegment(sketch, "E7.11.2.3", {"start": v(-228.5, 1356.5) * mm, "end": v(-178.5, 1356.5) * mm});
            skLineSegment(sketch, "E7.11.3.0", {"start": v(-178.5, 1352.5) * mm, "end": v(-178.5, 1302.5) * mm});
            skLineSegment(sketch, "E7.11.3.1", {"start": v(-228.5, 1352.5) * mm, "end": v(-178.5, 1352.5) * mm});
            skLineSegment(sketch, "E7.11.3.2", {"start": v(-228.5, 1352.5) * mm, "end": v(-228.5, 1302.5) * mm});
            skLineSegment(sketch, "E7.11.3.3", {"start": v(-228.5, 1302.5) * mm, "end": v(-178.5, 1302.5) * mm});
            skLineSegment(sketch, "E7.11.4.0", {"start": v(-178.5, 1298.5) * mm, "end": v(-178.5, 1248.5) * mm});
            skLineSegment(sketch, "E7.11.4.1", {"start": v(-228.5, 1298.5) * mm, "end": v(-178.5, 1298.5) * mm});
            skLineSegment(sketch, "E7.11.4.2", {"start": v(-228.5, 1298.5) * mm, "end": v(-228.5, 1248.5) * mm});
            skLineSegment(sketch, "E7.11.4.3", {"start": v(-228.5, 1248.5) * mm, "end": v(-178.5, 1248.5) * mm});
            skLineSegment(sketch, "E7.11.5.0", {"start": v(-178.5, 1244.5) * mm, "end": v(-178.5, 1194.5) * mm});
            skLineSegment(sketch, "E7.11.5.1", {"start": v(-228.5, 1244.5) * mm, "end": v(-178.5, 1244.5) * mm});
            skLineSegment(sketch, "E7.11.5.2", {"start": v(-228.5, 1244.5) * mm, "end": v(-228.5, 1194.5) * mm});
            skLineSegment(sketch, "E7.11.5.3", {"start": v(-228.5, 1194.5) * mm, "end": v(-178.5, 1194.5) * mm});
            skLineSegment(sketch, "E7.11.6.0", {"start": v(-178.5, 1190.5) * mm, "end": v(-178.5, 1140.5) * mm});
            skLineSegment(sketch, "E7.11.6.1", {"start": v(-228.5, 1190.5) * mm, "end": v(-178.5, 1190.5) * mm});
            skLineSegment(sketch, "E7.11.6.2", {"start": v(-228.5, 1190.5) * mm, "end": v(-228.5, 1140.5) * mm});
            skLineSegment(sketch, "E7.11.6.3", {"start": v(-228.5, 1140.5) * mm, "end": v(-178.5, 1140.5) * mm});
            skLineSegment(sketch, "E7.11.7.0", {"start": v(-178.5, 1136.5) * mm, "end": v(-178.5, 1086.5) * mm});
            skLineSegment(sketch, "E7.11.7.1", {"start": v(-228.5, 1136.5) * mm, "end": v(-178.5, 1136.5) * mm});
            skLineSegment(sketch, "E7.11.7.2", {"start": v(-228.5, 1136.5) * mm, "end": v(-228.5, 1086.5) * mm});
            skLineSegment(sketch, "E7.11.7.3", {"start": v(-228.5, 1086.5) * mm, "end": v(-178.5, 1086.5) * mm});
            skLineSegment(sketch, "E7.11.8.0", {"start": v(-178.5, 1082.5) * mm, "end": v(-178.5, 1032.5) * mm});
            skLineSegment(sketch, "E7.11.8.1", {"start": v(-228.5, 1082.5) * mm, "end": v(-178.5, 1082.5) * mm});
            skLineSegment(sketch, "E7.11.8.2", {"start": v(-228.5, 1082.5) * mm, "end": v(-228.5, 1032.5) * mm});
            skLineSegment(sketch, "E7.11.8.3", {"start": v(-228.5, 1032.5) * mm, "end": v(-178.5, 1032.5) * mm});
            skLineSegment(sketch, "E7.11.9.0", {"start": v(-178.5, 1028.5) * mm, "end": v(-178.5, 978.5) * mm});
            skLineSegment(sketch, "E7.11.9.1", {"start": v(-228.5, 1028.5) * mm, "end": v(-178.5, 1028.5) * mm});
            skLineSegment(sketch, "E7.11.9.2", {"start": v(-228.5, 1028.5) * mm, "end": v(-228.5, 978.5) * mm});
            skLineSegment(sketch, "E7.11.9.3", {"start": v(-228.5, 978.5) * mm, "end": v(-178.5, 978.5) * mm});
            skLineSegment(sketch, "E7.11.10.0", {"start": v(-178.5, 974.5) * mm, "end": v(-178.5, 924.5) * mm});
            skLineSegment(sketch, "E7.11.10.1", {"start": v(-228.5, 974.5) * mm, "end": v(-178.5, 974.5) * mm});
            skLineSegment(sketch, "E7.11.10.2", {"start": v(-228.5, 974.5) * mm, "end": v(-228.5, 924.5) * mm});
            skLineSegment(sketch, "E7.11.10.3", {"start": v(-228.5, 924.5) * mm, "end": v(-178.5, 924.5) * mm});
            skLineSegment(sketch, "E7.11.11.0", {"start": v(-178.5, 920.5) * mm, "end": v(-178.5, 870.5) * mm});
            skLineSegment(sketch, "E7.11.11.1", {"start": v(-228.5, 920.5) * mm, "end": v(-178.5, 920.5) * mm});
            skLineSegment(sketch, "E7.11.11.2", {"start": v(-228.5, 920.5) * mm, "end": v(-228.5, 870.5) * mm});
            skLineSegment(sketch, "E7.11.11.3", {"start": v(-228.5, 870.5) * mm, "end": v(-178.5, 870.5) * mm});
            skLineSegment(sketch, "E7.11.12.0", {"start": v(-178.5, 866.5) * mm, "end": v(-178.5, 816.5) * mm});
            skLineSegment(sketch, "E7.11.12.1", {"start": v(-228.5, 866.5) * mm, "end": v(-178.5, 866.5) * mm});
            skLineSegment(sketch, "E7.11.12.2", {"start": v(-228.5, 866.5) * mm, "end": v(-228.5, 816.5) * mm});
            skLineSegment(sketch, "E7.11.12.3", {"start": v(-228.5, 816.5) * mm, "end": v(-178.5, 816.5) * mm});
            skLineSegment(sketch, "E7.11.13.0", {"start": v(-178.5, 812.5) * mm, "end": v(-178.5, 762.5) * mm});
            skLineSegment(sketch, "E7.11.13.1", {"start": v(-228.5, 812.5) * mm, "end": v(-178.5, 812.5) * mm});
            skLineSegment(sketch, "E7.11.13.2", {"start": v(-228.5, 812.5) * mm, "end": v(-228.5, 762.5) * mm});
            skLineSegment(sketch, "E7.11.13.3", {"start": v(-228.5, 762.5) * mm, "end": v(-178.5, 762.5) * mm});
            skLineSegment(sketch, "E7.11.14.0", {"start": v(-178.5, 758.5) * mm, "end": v(-178.5, 708.5) * mm});
            skLineSegment(sketch, "E7.11.14.1", {"start": v(-228.5, 758.5) * mm, "end": v(-178.5, 758.5) * mm});
            skLineSegment(sketch, "E7.11.14.2", {"start": v(-228.5, 758.5) * mm, "end": v(-228.5, 708.5) * mm});
            skLineSegment(sketch, "E7.11.14.3", {"start": v(-228.5, 708.5) * mm, "end": v(-178.5, 708.5) * mm});
            skLineSegment(sketch, "E7.11.15.0", {"start": v(-178.5, 704.5) * mm, "end": v(-178.5, 654.5) * mm});
            skLineSegment(sketch, "E7.11.15.1", {"start": v(-228.5, 704.5) * mm, "end": v(-178.5, 704.5) * mm});
            skLineSegment(sketch, "E7.11.15.2", {"start": v(-228.5, 704.5) * mm, "end": v(-228.5, 654.5) * mm});
            skLineSegment(sketch, "E7.11.15.3", {"start": v(-228.5, 654.5) * mm, "end": v(-178.5, 654.5) * mm});
            skLineSegment(sketch, "E7.11.16.0", {"start": v(-178.5, 650.5) * mm, "end": v(-178.5, 600.5) * mm});
            skLineSegment(sketch, "E7.11.16.1", {"start": v(-228.5, 650.5) * mm, "end": v(-178.5, 650.5) * mm});
            skLineSegment(sketch, "E7.11.16.2", {"start": v(-228.5, 650.5) * mm, "end": v(-228.5, 600.5) * mm});
            skLineSegment(sketch, "E7.11.16.3", {"start": v(-228.5, 600.5) * mm, "end": v(-178.5, 600.5) * mm});
            skLineSegment(sketch, "E7.11.17.0", {"start": v(-178.5, 596.5) * mm, "end": v(-178.5, 546.5) * mm});
            skLineSegment(sketch, "E7.11.17.1", {"start": v(-228.5, 596.5) * mm, "end": v(-178.5, 596.5) * mm});
            skLineSegment(sketch, "E7.11.17.2", {"start": v(-228.5, 596.5) * mm, "end": v(-228.5, 546.5) * mm});
            skLineSegment(sketch, "E7.11.17.3", {"start": v(-228.5, 546.5) * mm, "end": v(-178.5, 546.5) * mm});
            skLineSegment(sketch, "E7.11.18.0", {"start": v(-178.5, 542.5) * mm, "end": v(-178.5, 492.5) * mm});
            skLineSegment(sketch, "E7.11.18.1", {"start": v(-228.5, 542.5) * mm, "end": v(-178.5, 542.5) * mm});
            skLineSegment(sketch, "E7.11.18.2", {"start": v(-228.5, 542.5) * mm, "end": v(-228.5, 492.5) * mm});
            skLineSegment(sketch, "E7.11.18.3", {"start": v(-228.5, 492.5) * mm, "end": v(-178.5, 492.5) * mm});
            skLineSegment(sketch, "E7.11.19.0", {"start": v(-178.5, 488.5) * mm, "end": v(-178.5, 438.5) * mm});
            skLineSegment(sketch, "E7.11.19.1", {"start": v(-228.5, 488.5) * mm, "end": v(-178.5, 488.5) * mm});
            skLineSegment(sketch, "E7.11.19.2", {"start": v(-228.5, 488.5) * mm, "end": v(-228.5, 438.5) * mm});
            skLineSegment(sketch, "E7.11.19.3", {"start": v(-228.5, 438.5) * mm, "end": v(-178.5, 438.5) * mm});
            skLineSegment(sketch, "E7.11.20.0", {"start": v(-178.5, 434.5) * mm, "end": v(-178.5, 384.5) * mm});
            skLineSegment(sketch, "E7.11.20.1", {"start": v(-228.5, 434.5) * mm, "end": v(-178.5, 434.5) * mm});
            skLineSegment(sketch, "E7.11.20.2", {"start": v(-228.5, 434.5) * mm, "end": v(-228.5, 384.5) * mm});
            skLineSegment(sketch, "E7.11.20.3", {"start": v(-228.5, 384.5) * mm, "end": v(-178.5, 384.5) * mm});
            skLineSegment(sketch, "E7.11.21.0", {"start": v(-178.5, 380.5) * mm, "end": v(-178.5, 330.5) * mm});
            skLineSegment(sketch, "E7.11.21.1", {"start": v(-228.5, 380.5) * mm, "end": v(-178.5, 380.5) * mm});
            skLineSegment(sketch, "E7.11.21.2", {"start": v(-228.5, 380.5) * mm, "end": v(-228.5, 330.5) * mm});
            skLineSegment(sketch, "E7.11.21.3", {"start": v(-228.5, 330.5) * mm, "end": v(-178.5, 330.5) * mm});
            skLineSegment(sketch, "E7.11.22.0", {"start": v(-178.5, 326.5) * mm, "end": v(-178.5, 276.5) * mm});
            skLineSegment(sketch, "E7.11.22.1", {"start": v(-228.5, 326.5) * mm, "end": v(-178.5, 326.5) * mm});
            skLineSegment(sketch, "E7.11.22.2", {"start": v(-228.5, 326.5) * mm, "end": v(-228.5, 276.5) * mm});
            skLineSegment(sketch, "E7.11.22.3", {"start": v(-228.5, 276.5) * mm, "end": v(-178.5, 276.5) * mm});
            skLineSegment(sketch, "E7.11.23.0", {"start": v(-178.5, 272.5) * mm, "end": v(-178.5, 222.5) * mm});
            skLineSegment(sketch, "E7.11.23.1", {"start": v(-228.5, 272.5) * mm, "end": v(-178.5, 272.5) * mm});
            skLineSegment(sketch, "E7.11.23.2", {"start": v(-228.5, 272.5) * mm, "end": v(-228.5, 222.5) * mm});
            skLineSegment(sketch, "E7.11.23.3", {"start": v(-228.5, 222.5) * mm, "end": v(-178.5, 222.5) * mm});
            skLineSegment(sketch, "E7.11.24.0", {"start": v(-178.5, 218.5) * mm, "end": v(-178.5, 168.5) * mm});
            skLineSegment(sketch, "E7.11.24.1", {"start": v(-228.5, 218.5) * mm, "end": v(-178.5, 218.5) * mm});
            skLineSegment(sketch, "E7.11.24.2", {"start": v(-228.5, 218.5) * mm, "end": v(-228.5, 168.5) * mm});
            skLineSegment(sketch, "E7.11.24.3", {"start": v(-228.5, 168.5) * mm, "end": v(-178.5, 168.5) * mm});
            skLineSegment(sketch, "E7.11.25.0", {"start": v(-178.5, 164.5) * mm, "end": v(-178.5, 114.5) * mm});
            skLineSegment(sketch, "E7.11.25.1", {"start": v(-228.5, 164.5) * mm, "end": v(-178.5, 164.5) * mm});
            skLineSegment(sketch, "E7.11.25.2", {"start": v(-228.5, 164.5) * mm, "end": v(-228.5, 114.5) * mm});
            skLineSegment(sketch, "E7.11.25.3", {"start": v(-228.5, 114.5) * mm, "end": v(-178.5, 114.5) * mm});
            skLineSegment(sketch, "E7.11.26.0", {"start": v(-178.5, 110.5) * mm, "end": v(-178.5, 60.5) * mm});
            skLineSegment(sketch, "E7.11.26.1", {"start": v(-228.5, 110.5) * mm, "end": v(-178.5, 110.5) * mm});
            skLineSegment(sketch, "E7.11.26.2", {"start": v(-228.5, 110.5) * mm, "end": v(-228.5, 60.5) * mm});
            skLineSegment(sketch, "E7.11.26.3", {"start": v(-228.5, 60.5) * mm, "end": v(-178.5, 60.5) * mm});
            skLineSegment(sketch, "E7.11.27.0", {"start": v(-178.5, 56.5) * mm, "end": v(-178.5, 6.5) * mm});
            skLineSegment(sketch, "E7.11.27.1", {"start": v(-228.5, 56.5) * mm, "end": v(-178.5, 56.5) * mm});
            skLineSegment(sketch, "E7.11.27.2", {"start": v(-228.5, 56.5) * mm, "end": v(-228.5, 6.5) * mm});
            skLineSegment(sketch, "E7.11.27.3", {"start": v(-228.5, 6.5) * mm, "end": v(-178.5, 6.5) * mm});
            skLineSegment(sketch, "E7.12.0.0", {"start": v(-124.5, 1514.5) * mm, "end": v(-124.5, 1464.5) * mm});
            skLineSegment(sketch, "E7.12.0.1", {"start": v(-174.5, 1514.5) * mm, "end": v(-124.5, 1514.5) * mm});
            skLineSegment(sketch, "E7.12.0.2", {"start": v(-174.5, 1514.5) * mm, "end": v(-174.5, 1464.5) * mm});
            skLineSegment(sketch, "E7.12.0.3", {"start": v(-174.5, 1464.5) * mm, "end": v(-124.5, 1464.5) * mm});
            skLineSegment(sketch, "E7.12.1.0", {"start": v(-124.5, 1460.5) * mm, "end": v(-124.5, 1410.5) * mm});
            skLineSegment(sketch, "E7.12.1.1", {"start": v(-174.5, 1460.5) * mm, "end": v(-124.5, 1460.5) * mm});
            skLineSegment(sketch, "E7.12.1.2", {"start": v(-174.5, 1460.5) * mm, "end": v(-174.5, 1410.5) * mm});
            skLineSegment(sketch, "E7.12.1.3", {"start": v(-174.5, 1410.5) * mm, "end": v(-124.5, 1410.5) * mm});
            skLineSegment(sketch, "E7.12.2.0", {"start": v(-124.5, 1406.5) * mm, "end": v(-124.5, 1356.5) * mm});
            skLineSegment(sketch, "E7.12.2.1", {"start": v(-174.5, 1406.5) * mm, "end": v(-124.5, 1406.5) * mm});
            skLineSegment(sketch, "E7.12.2.2", {"start": v(-174.5, 1406.5) * mm, "end": v(-174.5, 1356.5) * mm});
            skLineSegment(sketch, "E7.12.2.3", {"start": v(-174.5, 1356.5) * mm, "end": v(-124.5, 1356.5) * mm});
            skLineSegment(sketch, "E7.12.3.0", {"start": v(-124.5, 1352.5) * mm, "end": v(-124.5, 1302.5) * mm});
            skLineSegment(sketch, "E7.12.3.1", {"start": v(-174.5, 1352.5) * mm, "end": v(-124.5, 1352.5) * mm});
            skLineSegment(sketch, "E7.12.3.2", {"start": v(-174.5, 1352.5) * mm, "end": v(-174.5, 1302.5) * mm});
            skLineSegment(sketch, "E7.12.3.3", {"start": v(-174.5, 1302.5) * mm, "end": v(-124.5, 1302.5) * mm});
            skLineSegment(sketch, "E7.12.4.0", {"start": v(-124.5, 1298.5) * mm, "end": v(-124.5, 1248.5) * mm});
            skLineSegment(sketch, "E7.12.4.1", {"start": v(-174.5, 1298.5) * mm, "end": v(-124.5, 1298.5) * mm});
            skLineSegment(sketch, "E7.12.4.2", {"start": v(-174.5, 1298.5) * mm, "end": v(-174.5, 1248.5) * mm});
            skLineSegment(sketch, "E7.12.4.3", {"start": v(-174.5, 1248.5) * mm, "end": v(-124.5, 1248.5) * mm});
            skLineSegment(sketch, "E7.12.5.0", {"start": v(-124.5, 1244.5) * mm, "end": v(-124.5, 1194.5) * mm});
            skLineSegment(sketch, "E7.12.5.1", {"start": v(-174.5, 1244.5) * mm, "end": v(-124.5, 1244.5) * mm});
            skLineSegment(sketch, "E7.12.5.2", {"start": v(-174.5, 1244.5) * mm, "end": v(-174.5, 1194.5) * mm});
            skLineSegment(sketch, "E7.12.5.3", {"start": v(-174.5, 1194.5) * mm, "end": v(-124.5, 1194.5) * mm});
            skLineSegment(sketch, "E7.12.6.0", {"start": v(-124.5, 1190.5) * mm, "end": v(-124.5, 1140.5) * mm});
            skLineSegment(sketch, "E7.12.6.1", {"start": v(-174.5, 1190.5) * mm, "end": v(-124.5, 1190.5) * mm});
            skLineSegment(sketch, "E7.12.6.2", {"start": v(-174.5, 1190.5) * mm, "end": v(-174.5, 1140.5) * mm});
            skLineSegment(sketch, "E7.12.6.3", {"start": v(-174.5, 1140.5) * mm, "end": v(-124.5, 1140.5) * mm});
            skLineSegment(sketch, "E7.12.7.0", {"start": v(-124.5, 1136.5) * mm, "end": v(-124.5, 1086.5) * mm});
            skLineSegment(sketch, "E7.12.7.1", {"start": v(-174.5, 1136.5) * mm, "end": v(-124.5, 1136.5) * mm});
            skLineSegment(sketch, "E7.12.7.2", {"start": v(-174.5, 1136.5) * mm, "end": v(-174.5, 1086.5) * mm});
            skLineSegment(sketch, "E7.12.7.3", {"start": v(-174.5, 1086.5) * mm, "end": v(-124.5, 1086.5) * mm});
            skLineSegment(sketch, "E7.12.8.0", {"start": v(-124.5, 1082.5) * mm, "end": v(-124.5, 1032.5) * mm});
            skLineSegment(sketch, "E7.12.8.1", {"start": v(-174.5, 1082.5) * mm, "end": v(-124.5, 1082.5) * mm});
            skLineSegment(sketch, "E7.12.8.2", {"start": v(-174.5, 1082.5) * mm, "end": v(-174.5, 1032.5) * mm});
            skLineSegment(sketch, "E7.12.8.3", {"start": v(-174.5, 1032.5) * mm, "end": v(-124.5, 1032.5) * mm});
            skLineSegment(sketch, "E7.12.9.0", {"start": v(-124.5, 1028.5) * mm, "end": v(-124.5, 978.5) * mm});
            skLineSegment(sketch, "E7.12.9.1", {"start": v(-174.5, 1028.5) * mm, "end": v(-124.5, 1028.5) * mm});
            skLineSegment(sketch, "E7.12.9.2", {"start": v(-174.5, 1028.5) * mm, "end": v(-174.5, 978.5) * mm});
            skLineSegment(sketch, "E7.12.9.3", {"start": v(-174.5, 978.5) * mm, "end": v(-124.5, 978.5) * mm});
            skLineSegment(sketch, "E7.12.10.0", {"start": v(-124.5, 974.5) * mm, "end": v(-124.5, 924.5) * mm});
            skLineSegment(sketch, "E7.12.10.1", {"start": v(-174.5, 974.5) * mm, "end": v(-124.5, 974.5) * mm});
            skLineSegment(sketch, "E7.12.10.2", {"start": v(-174.5, 974.5) * mm, "end": v(-174.5, 924.5) * mm});
            skLineSegment(sketch, "E7.12.10.3", {"start": v(-174.5, 924.5) * mm, "end": v(-124.5, 924.5) * mm});
            skLineSegment(sketch, "E7.12.11.0", {"start": v(-124.5, 920.5) * mm, "end": v(-124.5, 870.5) * mm});
            skLineSegment(sketch, "E7.12.11.1", {"start": v(-174.5, 920.5) * mm, "end": v(-124.5, 920.5) * mm});
            skLineSegment(sketch, "E7.12.11.2", {"start": v(-174.5, 920.5) * mm, "end": v(-174.5, 870.5) * mm});
            skLineSegment(sketch, "E7.12.11.3", {"start": v(-174.5, 870.5) * mm, "end": v(-124.5, 870.5) * mm});
            skLineSegment(sketch, "E7.12.12.0", {"start": v(-124.5, 866.5) * mm, "end": v(-124.5, 816.5) * mm});
            skLineSegment(sketch, "E7.12.12.1", {"start": v(-174.5, 866.5) * mm, "end": v(-124.5, 866.5) * mm});
            skLineSegment(sketch, "E7.12.12.2", {"start": v(-174.5, 866.5) * mm, "end": v(-174.5, 816.5) * mm});
            skLineSegment(sketch, "E7.12.12.3", {"start": v(-174.5, 816.5) * mm, "end": v(-124.5, 816.5) * mm});
            skLineSegment(sketch, "E7.12.13.0", {"start": v(-124.5, 812.5) * mm, "end": v(-124.5, 762.5) * mm});
            skLineSegment(sketch, "E7.12.13.1", {"start": v(-174.5, 812.5) * mm, "end": v(-124.5, 812.5) * mm});
            skLineSegment(sketch, "E7.12.13.2", {"start": v(-174.5, 812.5) * mm, "end": v(-174.5, 762.5) * mm});
            skLineSegment(sketch, "E7.12.13.3", {"start": v(-174.5, 762.5) * mm, "end": v(-124.5, 762.5) * mm});
            skLineSegment(sketch, "E7.12.14.0", {"start": v(-124.5, 758.5) * mm, "end": v(-124.5, 708.5) * mm});
            skLineSegment(sketch, "E7.12.14.1", {"start": v(-174.5, 758.5) * mm, "end": v(-124.5, 758.5) * mm});
            skLineSegment(sketch, "E7.12.14.2", {"start": v(-174.5, 758.5) * mm, "end": v(-174.5, 708.5) * mm});
            skLineSegment(sketch, "E7.12.14.3", {"start": v(-174.5, 708.5) * mm, "end": v(-124.5, 708.5) * mm});
            skLineSegment(sketch, "E7.12.15.0", {"start": v(-124.5, 704.5) * mm, "end": v(-124.5, 654.5) * mm});
            skLineSegment(sketch, "E7.12.15.1", {"start": v(-174.5, 704.5) * mm, "end": v(-124.5, 704.5) * mm});
            skLineSegment(sketch, "E7.12.15.2", {"start": v(-174.5, 704.5) * mm, "end": v(-174.5, 654.5) * mm});
            skLineSegment(sketch, "E7.12.15.3", {"start": v(-174.5, 654.5) * mm, "end": v(-124.5, 654.5) * mm});
            skLineSegment(sketch, "E7.12.16.0", {"start": v(-124.5, 650.5) * mm, "end": v(-124.5, 600.5) * mm});
            skLineSegment(sketch, "E7.12.16.1", {"start": v(-174.5, 650.5) * mm, "end": v(-124.5, 650.5) * mm});
            skLineSegment(sketch, "E7.12.16.2", {"start": v(-174.5, 650.5) * mm, "end": v(-174.5, 600.5) * mm});
            skLineSegment(sketch, "E7.12.16.3", {"start": v(-174.5, 600.5) * mm, "end": v(-124.5, 600.5) * mm});
            skLineSegment(sketch, "E7.12.17.0", {"start": v(-124.5, 596.5) * mm, "end": v(-124.5, 546.5) * mm});
            skLineSegment(sketch, "E7.12.17.1", {"start": v(-174.5, 596.5) * mm, "end": v(-124.5, 596.5) * mm});
            skLineSegment(sketch, "E7.12.17.2", {"start": v(-174.5, 596.5) * mm, "end": v(-174.5, 546.5) * mm});
            skLineSegment(sketch, "E7.12.17.3", {"start": v(-174.5, 546.5) * mm, "end": v(-124.5, 546.5) * mm});
            skLineSegment(sketch, "E7.12.18.0", {"start": v(-124.5, 542.5) * mm, "end": v(-124.5, 492.5) * mm});
            skLineSegment(sketch, "E7.12.18.1", {"start": v(-174.5, 542.5) * mm, "end": v(-124.5, 542.5) * mm});
            skLineSegment(sketch, "E7.12.18.2", {"start": v(-174.5, 542.5) * mm, "end": v(-174.5, 492.5) * mm});
            skLineSegment(sketch, "E7.12.18.3", {"start": v(-174.5, 492.5) * mm, "end": v(-124.5, 492.5) * mm});
            skLineSegment(sketch, "E7.12.19.0", {"start": v(-124.5, 488.5) * mm, "end": v(-124.5, 438.5) * mm});
            skLineSegment(sketch, "E7.12.19.1", {"start": v(-174.5, 488.5) * mm, "end": v(-124.5, 488.5) * mm});
            skLineSegment(sketch, "E7.12.19.2", {"start": v(-174.5, 488.5) * mm, "end": v(-174.5, 438.5) * mm});
            skLineSegment(sketch, "E7.12.19.3", {"start": v(-174.5, 438.5) * mm, "end": v(-124.5, 438.5) * mm});
            skLineSegment(sketch, "E7.12.20.0", {"start": v(-124.5, 434.5) * mm, "end": v(-124.5, 384.5) * mm});
            skLineSegment(sketch, "E7.12.20.1", {"start": v(-174.5, 434.5) * mm, "end": v(-124.5, 434.5) * mm});
            skLineSegment(sketch, "E7.12.20.2", {"start": v(-174.5, 434.5) * mm, "end": v(-174.5, 384.5) * mm});
            skLineSegment(sketch, "E7.12.20.3", {"start": v(-174.5, 384.5) * mm, "end": v(-124.5, 384.5) * mm});
            skLineSegment(sketch, "E7.12.21.0", {"start": v(-124.5, 380.5) * mm, "end": v(-124.5, 330.5) * mm});
            skLineSegment(sketch, "E7.12.21.1", {"start": v(-174.5, 380.5) * mm, "end": v(-124.5, 380.5) * mm});
            skLineSegment(sketch, "E7.12.21.2", {"start": v(-174.5, 380.5) * mm, "end": v(-174.5, 330.5) * mm});
            skLineSegment(sketch, "E7.12.21.3", {"start": v(-174.5, 330.5) * mm, "end": v(-124.5, 330.5) * mm});
            skLineSegment(sketch, "E7.12.22.0", {"start": v(-124.5, 326.5) * mm, "end": v(-124.5, 276.5) * mm});
            skLineSegment(sketch, "E7.12.22.1", {"start": v(-174.5, 326.5) * mm, "end": v(-124.5, 326.5) * mm});
            skLineSegment(sketch, "E7.12.22.2", {"start": v(-174.5, 326.5) * mm, "end": v(-174.5, 276.5) * mm});
            skLineSegment(sketch, "E7.12.22.3", {"start": v(-174.5, 276.5) * mm, "end": v(-124.5, 276.5) * mm});
            skLineSegment(sketch, "E7.12.23.0", {"start": v(-124.5, 272.5) * mm, "end": v(-124.5, 222.5) * mm});
            skLineSegment(sketch, "E7.12.23.1", {"start": v(-174.5, 272.5) * mm, "end": v(-124.5, 272.5) * mm});
            skLineSegment(sketch, "E7.12.23.2", {"start": v(-174.5, 272.5) * mm, "end": v(-174.5, 222.5) * mm});
            skLineSegment(sketch, "E7.12.23.3", {"start": v(-174.5, 222.5) * mm, "end": v(-124.5, 222.5) * mm});
            skLineSegment(sketch, "E7.12.24.0", {"start": v(-124.5, 218.5) * mm, "end": v(-124.5, 168.5) * mm});
            skLineSegment(sketch, "E7.12.24.1", {"start": v(-174.5, 218.5) * mm, "end": v(-124.5, 218.5) * mm});
            skLineSegment(sketch, "E7.12.24.2", {"start": v(-174.5, 218.5) * mm, "end": v(-174.5, 168.5) * mm});
            skLineSegment(sketch, "E7.12.24.3", {"start": v(-174.5, 168.5) * mm, "end": v(-124.5, 168.5) * mm});
            skLineSegment(sketch, "E7.12.25.0", {"start": v(-124.5, 164.5) * mm, "end": v(-124.5, 114.5) * mm});
            skLineSegment(sketch, "E7.12.25.1", {"start": v(-174.5, 164.5) * mm, "end": v(-124.5, 164.5) * mm});
            skLineSegment(sketch, "E7.12.25.2", {"start": v(-174.5, 164.5) * mm, "end": v(-174.5, 114.5) * mm});
            skLineSegment(sketch, "E7.12.25.3", {"start": v(-174.5, 114.5) * mm, "end": v(-124.5, 114.5) * mm});
            skLineSegment(sketch, "E7.12.26.0", {"start": v(-124.5, 110.5) * mm, "end": v(-124.5, 60.5) * mm});
            skLineSegment(sketch, "E7.12.26.1", {"start": v(-174.5, 110.5) * mm, "end": v(-124.5, 110.5) * mm});
            skLineSegment(sketch, "E7.12.26.2", {"start": v(-174.5, 110.5) * mm, "end": v(-174.5, 60.5) * mm});
            skLineSegment(sketch, "E7.12.26.3", {"start": v(-174.5, 60.5) * mm, "end": v(-124.5, 60.5) * mm});
            skLineSegment(sketch, "E7.12.27.0", {"start": v(-124.5, 56.5) * mm, "end": v(-124.5, 6.5) * mm});
            skLineSegment(sketch, "E7.12.27.1", {"start": v(-174.5, 56.5) * mm, "end": v(-124.5, 56.5) * mm});
            skLineSegment(sketch, "E7.12.27.2", {"start": v(-174.5, 56.5) * mm, "end": v(-174.5, 6.5) * mm});
            skLineSegment(sketch, "E7.12.27.3", {"start": v(-174.5, 6.5) * mm, "end": v(-124.5, 6.5) * mm});
            skLineSegment(sketch, "E7.13.0.0", {"start": v(-70.5, 1514.5) * mm, "end": v(-70.5, 1464.5) * mm});
            skLineSegment(sketch, "E7.13.0.1", {"start": v(-120.5, 1514.5) * mm, "end": v(-70.5, 1514.5) * mm});
            skLineSegment(sketch, "E7.13.0.2", {"start": v(-120.5, 1514.5) * mm, "end": v(-120.5, 1464.5) * mm});
            skLineSegment(sketch, "E7.13.0.3", {"start": v(-120.5, 1464.5) * mm, "end": v(-70.5, 1464.5) * mm});
            skLineSegment(sketch, "E7.13.1.0", {"start": v(-70.5, 1460.5) * mm, "end": v(-70.5, 1410.5) * mm});
            skLineSegment(sketch, "E7.13.1.1", {"start": v(-120.5, 1460.5) * mm, "end": v(-70.5, 1460.5) * mm});
            skLineSegment(sketch, "E7.13.1.2", {"start": v(-120.5, 1460.5) * mm, "end": v(-120.5, 1410.5) * mm});
            skLineSegment(sketch, "E7.13.1.3", {"start": v(-120.5, 1410.5) * mm, "end": v(-70.5, 1410.5) * mm});
            skLineSegment(sketch, "E7.13.2.0", {"start": v(-70.5, 1406.5) * mm, "end": v(-70.5, 1356.5) * mm});
            skLineSegment(sketch, "E7.13.2.1", {"start": v(-120.5, 1406.5) * mm, "end": v(-70.5, 1406.5) * mm});
            skLineSegment(sketch, "E7.13.2.2", {"start": v(-120.5, 1406.5) * mm, "end": v(-120.5, 1356.5) * mm});
            skLineSegment(sketch, "E7.13.2.3", {"start": v(-120.5, 1356.5) * mm, "end": v(-70.5, 1356.5) * mm});
            skLineSegment(sketch, "E7.13.3.0", {"start": v(-70.5, 1352.5) * mm, "end": v(-70.5, 1302.5) * mm});
            skLineSegment(sketch, "E7.13.3.1", {"start": v(-120.5, 1352.5) * mm, "end": v(-70.5, 1352.5) * mm});
            skLineSegment(sketch, "E7.13.3.2", {"start": v(-120.5, 1352.5) * mm, "end": v(-120.5, 1302.5) * mm});
            skLineSegment(sketch, "E7.13.3.3", {"start": v(-120.5, 1302.5) * mm, "end": v(-70.5, 1302.5) * mm});
            skLineSegment(sketch, "E7.13.4.0", {"start": v(-70.5, 1298.5) * mm, "end": v(-70.5, 1248.5) * mm});
            skLineSegment(sketch, "E7.13.4.1", {"start": v(-120.5, 1298.5) * mm, "end": v(-70.5, 1298.5) * mm});
            skLineSegment(sketch, "E7.13.4.2", {"start": v(-120.5, 1298.5) * mm, "end": v(-120.5, 1248.5) * mm});
            skLineSegment(sketch, "E7.13.4.3", {"start": v(-120.5, 1248.5) * mm, "end": v(-70.5, 1248.5) * mm});
            skLineSegment(sketch, "E7.13.5.0", {"start": v(-70.5, 1244.5) * mm, "end": v(-70.5, 1194.5) * mm});
            skLineSegment(sketch, "E7.13.5.1", {"start": v(-120.5, 1244.5) * mm, "end": v(-70.5, 1244.5) * mm});
            skLineSegment(sketch, "E7.13.5.2", {"start": v(-120.5, 1244.5) * mm, "end": v(-120.5, 1194.5) * mm});
            skLineSegment(sketch, "E7.13.5.3", {"start": v(-120.5, 1194.5) * mm, "end": v(-70.5, 1194.5) * mm});
            skLineSegment(sketch, "E7.13.6.0", {"start": v(-70.5, 1190.5) * mm, "end": v(-70.5, 1140.5) * mm});
            skLineSegment(sketch, "E7.13.6.1", {"start": v(-120.5, 1190.5) * mm, "end": v(-70.5, 1190.5) * mm});
            skLineSegment(sketch, "E7.13.6.2", {"start": v(-120.5, 1190.5) * mm, "end": v(-120.5, 1140.5) * mm});
            skLineSegment(sketch, "E7.13.6.3", {"start": v(-120.5, 1140.5) * mm, "end": v(-70.5, 1140.5) * mm});
            skLineSegment(sketch, "E7.13.7.0", {"start": v(-70.5, 1136.5) * mm, "end": v(-70.5, 1086.5) * mm});
            skLineSegment(sketch, "E7.13.7.1", {"start": v(-120.5, 1136.5) * mm, "end": v(-70.5, 1136.5) * mm});
            skLineSegment(sketch, "E7.13.7.2", {"start": v(-120.5, 1136.5) * mm, "end": v(-120.5, 1086.5) * mm});
            skLineSegment(sketch, "E7.13.7.3", {"start": v(-120.5, 1086.5) * mm, "end": v(-70.5, 1086.5) * mm});
            skLineSegment(sketch, "E7.13.8.0", {"start": v(-70.5, 1082.5) * mm, "end": v(-70.5, 1032.5) * mm});
            skLineSegment(sketch, "E7.13.8.1", {"start": v(-120.5, 1082.5) * mm, "end": v(-70.5, 1082.5) * mm});
            skLineSegment(sketch, "E7.13.8.2", {"start": v(-120.5, 1082.5) * mm, "end": v(-120.5, 1032.5) * mm});
            skLineSegment(sketch, "E7.13.8.3", {"start": v(-120.5, 1032.5) * mm, "end": v(-70.5, 1032.5) * mm});
            skLineSegment(sketch, "E7.13.9.0", {"start": v(-70.5, 1028.5) * mm, "end": v(-70.5, 978.5) * mm});
            skLineSegment(sketch, "E7.13.9.1", {"start": v(-120.5, 1028.5) * mm, "end": v(-70.5, 1028.5) * mm});
            skLineSegment(sketch, "E7.13.9.2", {"start": v(-120.5, 1028.5) * mm, "end": v(-120.5, 978.5) * mm});
            skLineSegment(sketch, "E7.13.9.3", {"start": v(-120.5, 978.5) * mm, "end": v(-70.5, 978.5) * mm});
            skLineSegment(sketch, "E7.13.10.0", {"start": v(-70.5, 974.5) * mm, "end": v(-70.5, 924.5) * mm});
            skLineSegment(sketch, "E7.13.10.1", {"start": v(-120.5, 974.5) * mm, "end": v(-70.5, 974.5) * mm});
            skLineSegment(sketch, "E7.13.10.2", {"start": v(-120.5, 974.5) * mm, "end": v(-120.5, 924.5) * mm});
            skLineSegment(sketch, "E7.13.10.3", {"start": v(-120.5, 924.5) * mm, "end": v(-70.5, 924.5) * mm});
            skLineSegment(sketch, "E7.13.11.0", {"start": v(-70.5, 920.5) * mm, "end": v(-70.5, 870.5) * mm});
            skLineSegment(sketch, "E7.13.11.1", {"start": v(-120.5, 920.5) * mm, "end": v(-70.5, 920.5) * mm});
            skLineSegment(sketch, "E7.13.11.2", {"start": v(-120.5, 920.5) * mm, "end": v(-120.5, 870.5) * mm});
            skLineSegment(sketch, "E7.13.11.3", {"start": v(-120.5, 870.5) * mm, "end": v(-70.5, 870.5) * mm});
            skLineSegment(sketch, "E7.13.12.0", {"start": v(-70.5, 866.5) * mm, "end": v(-70.5, 816.5) * mm});
            skLineSegment(sketch, "E7.13.12.1", {"start": v(-120.5, 866.5) * mm, "end": v(-70.5, 866.5) * mm});
            skLineSegment(sketch, "E7.13.12.2", {"start": v(-120.5, 866.5) * mm, "end": v(-120.5, 816.5) * mm});
            skLineSegment(sketch, "E7.13.12.3", {"start": v(-120.5, 816.5) * mm, "end": v(-70.5, 816.5) * mm});
            skLineSegment(sketch, "E7.13.13.0", {"start": v(-70.5, 812.5) * mm, "end": v(-70.5, 762.5) * mm});
            skLineSegment(sketch, "E7.13.13.1", {"start": v(-120.5, 812.5) * mm, "end": v(-70.5, 812.5) * mm});
            skLineSegment(sketch, "E7.13.13.2", {"start": v(-120.5, 812.5) * mm, "end": v(-120.5, 762.5) * mm});
            skLineSegment(sketch, "E7.13.13.3", {"start": v(-120.5, 762.5) * mm, "end": v(-70.5, 762.5) * mm});
            skLineSegment(sketch, "E7.13.14.0", {"start": v(-70.5, 758.5) * mm, "end": v(-70.5, 708.5) * mm});
            skLineSegment(sketch, "E7.13.14.1", {"start": v(-120.5, 758.5) * mm, "end": v(-70.5, 758.5) * mm});
            skLineSegment(sketch, "E7.13.14.2", {"start": v(-120.5, 758.5) * mm, "end": v(-120.5, 708.5) * mm});
            skLineSegment(sketch, "E7.13.14.3", {"start": v(-120.5, 708.5) * mm, "end": v(-70.5, 708.5) * mm});
            skLineSegment(sketch, "E7.13.15.0", {"start": v(-70.5, 704.5) * mm, "end": v(-70.5, 654.5) * mm});
            skLineSegment(sketch, "E7.13.15.1", {"start": v(-120.5, 704.5) * mm, "end": v(-70.5, 704.5) * mm});
            skLineSegment(sketch, "E7.13.15.2", {"start": v(-120.5, 704.5) * mm, "end": v(-120.5, 654.5) * mm});
            skLineSegment(sketch, "E7.13.15.3", {"start": v(-120.5, 654.5) * mm, "end": v(-70.5, 654.5) * mm});
            skLineSegment(sketch, "E7.13.16.0", {"start": v(-70.5, 650.5) * mm, "end": v(-70.5, 600.5) * mm});
            skLineSegment(sketch, "E7.13.16.1", {"start": v(-120.5, 650.5) * mm, "end": v(-70.5, 650.5) * mm});
            skLineSegment(sketch, "E7.13.16.2", {"start": v(-120.5, 650.5) * mm, "end": v(-120.5, 600.5) * mm});
            skLineSegment(sketch, "E7.13.16.3", {"start": v(-120.5, 600.5) * mm, "end": v(-70.5, 600.5) * mm});
            skLineSegment(sketch, "E7.13.17.0", {"start": v(-70.5, 596.5) * mm, "end": v(-70.5, 546.5) * mm});
            skLineSegment(sketch, "E7.13.17.1", {"start": v(-120.5, 596.5) * mm, "end": v(-70.5, 596.5) * mm});
            skLineSegment(sketch, "E7.13.17.2", {"start": v(-120.5, 596.5) * mm, "end": v(-120.5, 546.5) * mm});
            skLineSegment(sketch, "E7.13.17.3", {"start": v(-120.5, 546.5) * mm, "end": v(-70.5, 546.5) * mm});
            skLineSegment(sketch, "E7.13.18.0", {"start": v(-70.5, 542.5) * mm, "end": v(-70.5, 492.5) * mm});
            skLineSegment(sketch, "E7.13.18.1", {"start": v(-120.5, 542.5) * mm, "end": v(-70.5, 542.5) * mm});
            skLineSegment(sketch, "E7.13.18.2", {"start": v(-120.5, 542.5) * mm, "end": v(-120.5, 492.5) * mm});
            skLineSegment(sketch, "E7.13.18.3", {"start": v(-120.5, 492.5) * mm, "end": v(-70.5, 492.5) * mm});
            skLineSegment(sketch, "E7.13.19.0", {"start": v(-70.5, 488.5) * mm, "end": v(-70.5, 438.5) * mm});
            skLineSegment(sketch, "E7.13.19.1", {"start": v(-120.5, 488.5) * mm, "end": v(-70.5, 488.5) * mm});
            skLineSegment(sketch, "E7.13.19.2", {"start": v(-120.5, 488.5) * mm, "end": v(-120.5, 438.5) * mm});
            skLineSegment(sketch, "E7.13.19.3", {"start": v(-120.5, 438.5) * mm, "end": v(-70.5, 438.5) * mm});
            skLineSegment(sketch, "E7.13.20.0", {"start": v(-70.5, 434.5) * mm, "end": v(-70.5, 384.5) * mm});
            skLineSegment(sketch, "E7.13.20.1", {"start": v(-120.5, 434.5) * mm, "end": v(-70.5, 434.5) * mm});
            skLineSegment(sketch, "E7.13.20.2", {"start": v(-120.5, 434.5) * mm, "end": v(-120.5, 384.5) * mm});
            skLineSegment(sketch, "E7.13.20.3", {"start": v(-120.5, 384.5) * mm, "end": v(-70.5, 384.5) * mm});
            skLineSegment(sketch, "E7.13.21.0", {"start": v(-70.5, 380.5) * mm, "end": v(-70.5, 330.5) * mm});
            skLineSegment(sketch, "E7.13.21.1", {"start": v(-120.5, 380.5) * mm, "end": v(-70.5, 380.5) * mm});
            skLineSegment(sketch, "E7.13.21.2", {"start": v(-120.5, 380.5) * mm, "end": v(-120.5, 330.5) * mm});
            skLineSegment(sketch, "E7.13.21.3", {"start": v(-120.5, 330.5) * mm, "end": v(-70.5, 330.5) * mm});
            skLineSegment(sketch, "E7.13.22.0", {"start": v(-70.5, 326.5) * mm, "end": v(-70.5, 276.5) * mm});
            skLineSegment(sketch, "E7.13.22.1", {"start": v(-120.5, 326.5) * mm, "end": v(-70.5, 326.5) * mm});
            skLineSegment(sketch, "E7.13.22.2", {"start": v(-120.5, 326.5) * mm, "end": v(-120.5, 276.5) * mm});
            skLineSegment(sketch, "E7.13.22.3", {"start": v(-120.5, 276.5) * mm, "end": v(-70.5, 276.5) * mm});
            skLineSegment(sketch, "E7.13.23.0", {"start": v(-70.5, 272.5) * mm, "end": v(-70.5, 222.5) * mm});
            skLineSegment(sketch, "E7.13.23.1", {"start": v(-120.5, 272.5) * mm, "end": v(-70.5, 272.5) * mm});
            skLineSegment(sketch, "E7.13.23.2", {"start": v(-120.5, 272.5) * mm, "end": v(-120.5, 222.5) * mm});
            skLineSegment(sketch, "E7.13.23.3", {"start": v(-120.5, 222.5) * mm, "end": v(-70.5, 222.5) * mm});
            skLineSegment(sketch, "E7.13.24.0", {"start": v(-70.5, 218.5) * mm, "end": v(-70.5, 168.5) * mm});
            skLineSegment(sketch, "E7.13.24.1", {"start": v(-120.5, 218.5) * mm, "end": v(-70.5, 218.5) * mm});
            skLineSegment(sketch, "E7.13.24.2", {"start": v(-120.5, 218.5) * mm, "end": v(-120.5, 168.5) * mm});
            skLineSegment(sketch, "E7.13.24.3", {"start": v(-120.5, 168.5) * mm, "end": v(-70.5, 168.5) * mm});
            skLineSegment(sketch, "E7.13.25.0", {"start": v(-70.5, 164.5) * mm, "end": v(-70.5, 114.5) * mm});
            skLineSegment(sketch, "E7.13.25.1", {"start": v(-120.5, 164.5) * mm, "end": v(-70.5, 164.5) * mm});
            skLineSegment(sketch, "E7.13.25.2", {"start": v(-120.5, 164.5) * mm, "end": v(-120.5, 114.5) * mm});
            skLineSegment(sketch, "E7.13.25.3", {"start": v(-120.5, 114.5) * mm, "end": v(-70.5, 114.5) * mm});
            skLineSegment(sketch, "E7.13.26.0", {"start": v(-70.5, 110.5) * mm, "end": v(-70.5, 60.5) * mm});
            skLineSegment(sketch, "E7.13.26.1", {"start": v(-120.5, 110.5) * mm, "end": v(-70.5, 110.5) * mm});
            skLineSegment(sketch, "E7.13.26.2", {"start": v(-120.5, 110.5) * mm, "end": v(-120.5, 60.5) * mm});
            skLineSegment(sketch, "E7.13.26.3", {"start": v(-120.5, 60.5) * mm, "end": v(-70.5, 60.5) * mm});
            skLineSegment(sketch, "E7.13.27.0", {"start": v(-70.5, 56.5) * mm, "end": v(-70.5, 6.5) * mm});
            skLineSegment(sketch, "E7.13.27.1", {"start": v(-120.5, 56.5) * mm, "end": v(-70.5, 56.5) * mm});
            skLineSegment(sketch, "E7.13.27.2", {"start": v(-120.5, 56.5) * mm, "end": v(-120.5, 6.5) * mm});
            skLineSegment(sketch, "E7.13.27.3", {"start": v(-120.5, 6.5) * mm, "end": v(-70.5, 6.5) * mm});
            skLineSegment(sketch, "E7.14.0.0", {"start": v(-16.5, 1514.5) * mm, "end": v(-16.5, 1464.5) * mm});
            skLineSegment(sketch, "E7.14.0.1", {"start": v(-66.5, 1514.5) * mm, "end": v(-16.5, 1514.5) * mm});
            skLineSegment(sketch, "E7.14.0.2", {"start": v(-66.5, 1514.5) * mm, "end": v(-66.5, 1464.5) * mm});
            skLineSegment(sketch, "E7.14.0.3", {"start": v(-66.5, 1464.5) * mm, "end": v(-16.5, 1464.5) * mm});
            skLineSegment(sketch, "E7.14.1.0", {"start": v(-16.5, 1460.5) * mm, "end": v(-16.5, 1410.5) * mm});
            skLineSegment(sketch, "E7.14.1.1", {"start": v(-66.5, 1460.5) * mm, "end": v(-16.5, 1460.5) * mm});
            skLineSegment(sketch, "E7.14.1.2", {"start": v(-66.5, 1460.5) * mm, "end": v(-66.5, 1410.5) * mm});
            skLineSegment(sketch, "E7.14.1.3", {"start": v(-66.5, 1410.5) * mm, "end": v(-16.5, 1410.5) * mm});
            skLineSegment(sketch, "E7.14.2.0", {"start": v(-16.5, 1406.5) * mm, "end": v(-16.5, 1356.5) * mm});
            skLineSegment(sketch, "E7.14.2.1", {"start": v(-66.5, 1406.5) * mm, "end": v(-16.5, 1406.5) * mm});
            skLineSegment(sketch, "E7.14.2.2", {"start": v(-66.5, 1406.5) * mm, "end": v(-66.5, 1356.5) * mm});
            skLineSegment(sketch, "E7.14.2.3", {"start": v(-66.5, 1356.5) * mm, "end": v(-16.5, 1356.5) * mm});
            skLineSegment(sketch, "E7.14.3.0", {"start": v(-16.5, 1352.5) * mm, "end": v(-16.5, 1302.5) * mm});
            skLineSegment(sketch, "E7.14.3.1", {"start": v(-66.5, 1352.5) * mm, "end": v(-16.5, 1352.5) * mm});
            skLineSegment(sketch, "E7.14.3.2", {"start": v(-66.5, 1352.5) * mm, "end": v(-66.5, 1302.5) * mm});
            skLineSegment(sketch, "E7.14.3.3", {"start": v(-66.5, 1302.5) * mm, "end": v(-16.5, 1302.5) * mm});
            skLineSegment(sketch, "E7.14.4.0", {"start": v(-16.5, 1298.5) * mm, "end": v(-16.5, 1248.5) * mm});
            skLineSegment(sketch, "E7.14.4.1", {"start": v(-66.5, 1298.5) * mm, "end": v(-16.5, 1298.5) * mm});
            skLineSegment(sketch, "E7.14.4.2", {"start": v(-66.5, 1298.5) * mm, "end": v(-66.5, 1248.5) * mm});
            skLineSegment(sketch, "E7.14.4.3", {"start": v(-66.5, 1248.5) * mm, "end": v(-16.5, 1248.5) * mm});
            skLineSegment(sketch, "E7.14.5.0", {"start": v(-16.5, 1244.5) * mm, "end": v(-16.5, 1194.5) * mm});
            skLineSegment(sketch, "E7.14.5.1", {"start": v(-66.5, 1244.5) * mm, "end": v(-16.5, 1244.5) * mm});
            skLineSegment(sketch, "E7.14.5.2", {"start": v(-66.5, 1244.5) * mm, "end": v(-66.5, 1194.5) * mm});
            skLineSegment(sketch, "E7.14.5.3", {"start": v(-66.5, 1194.5) * mm, "end": v(-16.5, 1194.5) * mm});
            skLineSegment(sketch, "E7.14.6.0", {"start": v(-16.5, 1190.5) * mm, "end": v(-16.5, 1140.5) * mm});
            skLineSegment(sketch, "E7.14.6.1", {"start": v(-66.5, 1190.5) * mm, "end": v(-16.5, 1190.5) * mm});
            skLineSegment(sketch, "E7.14.6.2", {"start": v(-66.5, 1190.5) * mm, "end": v(-66.5, 1140.5) * mm});
            skLineSegment(sketch, "E7.14.6.3", {"start": v(-66.5, 1140.5) * mm, "end": v(-16.5, 1140.5) * mm});
            skLineSegment(sketch, "E7.14.7.0", {"start": v(-16.5, 1136.5) * mm, "end": v(-16.5, 1086.5) * mm});
            skLineSegment(sketch, "E7.14.7.1", {"start": v(-66.5, 1136.5) * mm, "end": v(-16.5, 1136.5) * mm});
            skLineSegment(sketch, "E7.14.7.2", {"start": v(-66.5, 1136.5) * mm, "end": v(-66.5, 1086.5) * mm});
            skLineSegment(sketch, "E7.14.7.3", {"start": v(-66.5, 1086.5) * mm, "end": v(-16.5, 1086.5) * mm});
            skLineSegment(sketch, "E7.14.8.0", {"start": v(-16.5, 1082.5) * mm, "end": v(-16.5, 1032.5) * mm});
            skLineSegment(sketch, "E7.14.8.1", {"start": v(-66.5, 1082.5) * mm, "end": v(-16.5, 1082.5) * mm});
            skLineSegment(sketch, "E7.14.8.2", {"start": v(-66.5, 1082.5) * mm, "end": v(-66.5, 1032.5) * mm});
            skLineSegment(sketch, "E7.14.8.3", {"start": v(-66.5, 1032.5) * mm, "end": v(-16.5, 1032.5) * mm});
            skLineSegment(sketch, "E7.14.9.0", {"start": v(-16.5, 1028.5) * mm, "end": v(-16.5, 978.5) * mm});
            skLineSegment(sketch, "E7.14.9.1", {"start": v(-66.5, 1028.5) * mm, "end": v(-16.5, 1028.5) * mm});
            skLineSegment(sketch, "E7.14.9.2", {"start": v(-66.5, 1028.5) * mm, "end": v(-66.5, 978.5) * mm});
            skLineSegment(sketch, "E7.14.9.3", {"start": v(-66.5, 978.5) * mm, "end": v(-16.5, 978.5) * mm});
            skLineSegment(sketch, "E7.14.10.0", {"start": v(-16.5, 974.5) * mm, "end": v(-16.5, 924.5) * mm});
            skLineSegment(sketch, "E7.14.10.1", {"start": v(-66.5, 974.5) * mm, "end": v(-16.5, 974.5) * mm});
            skLineSegment(sketch, "E7.14.10.2", {"start": v(-66.5, 974.5) * mm, "end": v(-66.5, 924.5) * mm});
            skLineSegment(sketch, "E7.14.10.3", {"start": v(-66.5, 924.5) * mm, "end": v(-16.5, 924.5) * mm});
            skLineSegment(sketch, "E7.14.11.0", {"start": v(-16.5, 920.5) * mm, "end": v(-16.5, 870.5) * mm});
            skLineSegment(sketch, "E7.14.11.1", {"start": v(-66.5, 920.5) * mm, "end": v(-16.5, 920.5) * mm});
            skLineSegment(sketch, "E7.14.11.2", {"start": v(-66.5, 920.5) * mm, "end": v(-66.5, 870.5) * mm});
            skLineSegment(sketch, "E7.14.11.3", {"start": v(-66.5, 870.5) * mm, "end": v(-16.5, 870.5) * mm});
            skLineSegment(sketch, "E7.14.12.0", {"start": v(-16.5, 866.5) * mm, "end": v(-16.5, 816.5) * mm});
            skLineSegment(sketch, "E7.14.12.1", {"start": v(-66.5, 866.5) * mm, "end": v(-16.5, 866.5) * mm});
            skLineSegment(sketch, "E7.14.12.2", {"start": v(-66.5, 866.5) * mm, "end": v(-66.5, 816.5) * mm});
            skLineSegment(sketch, "E7.14.12.3", {"start": v(-66.5, 816.5) * mm, "end": v(-16.5, 816.5) * mm});
            skLineSegment(sketch, "E7.14.13.0", {"start": v(-16.5, 812.5) * mm, "end": v(-16.5, 762.5) * mm});
            skLineSegment(sketch, "E7.14.13.1", {"start": v(-66.5, 812.5) * mm, "end": v(-16.5, 812.5) * mm});
            skLineSegment(sketch, "E7.14.13.2", {"start": v(-66.5, 812.5) * mm, "end": v(-66.5, 762.5) * mm});
            skLineSegment(sketch, "E7.14.13.3", {"start": v(-66.5, 762.5) * mm, "end": v(-16.5, 762.5) * mm});
            skLineSegment(sketch, "E7.14.14.0", {"start": v(-16.5, 758.5) * mm, "end": v(-16.5, 708.5) * mm});
            skLineSegment(sketch, "E7.14.14.1", {"start": v(-66.5, 758.5) * mm, "end": v(-16.5, 758.5) * mm});
            skLineSegment(sketch, "E7.14.14.2", {"start": v(-66.5, 758.5) * mm, "end": v(-66.5, 708.5) * mm});
            skLineSegment(sketch, "E7.14.14.3", {"start": v(-66.5, 708.5) * mm, "end": v(-16.5, 708.5) * mm});
            skLineSegment(sketch, "E7.14.15.0", {"start": v(-16.5, 704.5) * mm, "end": v(-16.5, 654.5) * mm});
            skLineSegment(sketch, "E7.14.15.1", {"start": v(-66.5, 704.5) * mm, "end": v(-16.5, 704.5) * mm});
            skLineSegment(sketch, "E7.14.15.2", {"start": v(-66.5, 704.5) * mm, "end": v(-66.5, 654.5) * mm});
            skLineSegment(sketch, "E7.14.15.3", {"start": v(-66.5, 654.5) * mm, "end": v(-16.5, 654.5) * mm});
            skLineSegment(sketch, "E7.14.16.0", {"start": v(-16.5, 650.5) * mm, "end": v(-16.5, 600.5) * mm});
            skLineSegment(sketch, "E7.14.16.1", {"start": v(-66.5, 650.5) * mm, "end": v(-16.5, 650.5) * mm});
            skLineSegment(sketch, "E7.14.16.2", {"start": v(-66.5, 650.5) * mm, "end": v(-66.5, 600.5) * mm});
            skLineSegment(sketch, "E7.14.16.3", {"start": v(-66.5, 600.5) * mm, "end": v(-16.5, 600.5) * mm});
            skLineSegment(sketch, "E7.14.17.0", {"start": v(-16.5, 596.5) * mm, "end": v(-16.5, 546.5) * mm});
            skLineSegment(sketch, "E7.14.17.1", {"start": v(-66.5, 596.5) * mm, "end": v(-16.5, 596.5) * mm});
            skLineSegment(sketch, "E7.14.17.2", {"start": v(-66.5, 596.5) * mm, "end": v(-66.5, 546.5) * mm});
            skLineSegment(sketch, "E7.14.17.3", {"start": v(-66.5, 546.5) * mm, "end": v(-16.5, 546.5) * mm});
            skLineSegment(sketch, "E7.14.18.0", {"start": v(-16.5, 542.5) * mm, "end": v(-16.5, 492.5) * mm});
            skLineSegment(sketch, "E7.14.18.1", {"start": v(-66.5, 542.5) * mm, "end": v(-16.5, 542.5) * mm});
            skLineSegment(sketch, "E7.14.18.2", {"start": v(-66.5, 542.5) * mm, "end": v(-66.5, 492.5) * mm});
            skLineSegment(sketch, "E7.14.18.3", {"start": v(-66.5, 492.5) * mm, "end": v(-16.5, 492.5) * mm});
            skLineSegment(sketch, "E7.14.19.0", {"start": v(-16.5, 488.5) * mm, "end": v(-16.5, 438.5) * mm});
            skLineSegment(sketch, "E7.14.19.1", {"start": v(-66.5, 488.5) * mm, "end": v(-16.5, 488.5) * mm});
            skLineSegment(sketch, "E7.14.19.2", {"start": v(-66.5, 488.5) * mm, "end": v(-66.5, 438.5) * mm});
            skLineSegment(sketch, "E7.14.19.3", {"start": v(-66.5, 438.5) * mm, "end": v(-16.5, 438.5) * mm});
            skLineSegment(sketch, "E7.14.20.0", {"start": v(-16.5, 434.5) * mm, "end": v(-16.5, 384.5) * mm});
            skLineSegment(sketch, "E7.14.20.1", {"start": v(-66.5, 434.5) * mm, "end": v(-16.5, 434.5) * mm});
            skLineSegment(sketch, "E7.14.20.2", {"start": v(-66.5, 434.5) * mm, "end": v(-66.5, 384.5) * mm});
            skLineSegment(sketch, "E7.14.20.3", {"start": v(-66.5, 384.5) * mm, "end": v(-16.5, 384.5) * mm});
            skLineSegment(sketch, "E7.14.21.0", {"start": v(-16.5, 380.5) * mm, "end": v(-16.5, 330.5) * mm});
            skLineSegment(sketch, "E7.14.21.1", {"start": v(-66.5, 380.5) * mm, "end": v(-16.5, 380.5) * mm});
            skLineSegment(sketch, "E7.14.21.2", {"start": v(-66.5, 380.5) * mm, "end": v(-66.5, 330.5) * mm});
            skLineSegment(sketch, "E7.14.21.3", {"start": v(-66.5, 330.5) * mm, "end": v(-16.5, 330.5) * mm});
            skLineSegment(sketch, "E7.14.22.0", {"start": v(-16.5, 326.5) * mm, "end": v(-16.5, 276.5) * mm});
            skLineSegment(sketch, "E7.14.22.1", {"start": v(-66.5, 326.5) * mm, "end": v(-16.5, 326.5) * mm});
            skLineSegment(sketch, "E7.14.22.2", {"start": v(-66.5, 326.5) * mm, "end": v(-66.5, 276.5) * mm});
            skLineSegment(sketch, "E7.14.22.3", {"start": v(-66.5, 276.5) * mm, "end": v(-16.5, 276.5) * mm});
            skLineSegment(sketch, "E7.14.23.0", {"start": v(-16.5, 272.5) * mm, "end": v(-16.5, 222.5) * mm});
            skLineSegment(sketch, "E7.14.23.1", {"start": v(-66.5, 272.5) * mm, "end": v(-16.5, 272.5) * mm});
            skLineSegment(sketch, "E7.14.23.2", {"start": v(-66.5, 272.5) * mm, "end": v(-66.5, 222.5) * mm});
            skLineSegment(sketch, "E7.14.23.3", {"start": v(-66.5, 222.5) * mm, "end": v(-16.5, 222.5) * mm});
            skLineSegment(sketch, "E7.14.24.0", {"start": v(-16.5, 218.5) * mm, "end": v(-16.5, 168.5) * mm});
            skLineSegment(sketch, "E7.14.24.1", {"start": v(-66.5, 218.5) * mm, "end": v(-16.5, 218.5) * mm});
            skLineSegment(sketch, "E7.14.24.2", {"start": v(-66.5, 218.5) * mm, "end": v(-66.5, 168.5) * mm});
            skLineSegment(sketch, "E7.14.24.3", {"start": v(-66.5, 168.5) * mm, "end": v(-16.5, 168.5) * mm});
            skLineSegment(sketch, "E7.14.25.0", {"start": v(-16.5, 164.5) * mm, "end": v(-16.5, 114.5) * mm});
            skLineSegment(sketch, "E7.14.25.1", {"start": v(-66.5, 164.5) * mm, "end": v(-16.5, 164.5) * mm});
            skLineSegment(sketch, "E7.14.25.2", {"start": v(-66.5, 164.5) * mm, "end": v(-66.5, 114.5) * mm});
            skLineSegment(sketch, "E7.14.25.3", {"start": v(-66.5, 114.5) * mm, "end": v(-16.5, 114.5) * mm});
            skLineSegment(sketch, "E7.14.26.0", {"start": v(-16.5, 110.5) * mm, "end": v(-16.5, 60.5) * mm});
            skLineSegment(sketch, "E7.14.26.1", {"start": v(-66.5, 110.5) * mm, "end": v(-16.5, 110.5) * mm});
            skLineSegment(sketch, "E7.14.26.2", {"start": v(-66.5, 110.5) * mm, "end": v(-66.5, 60.5) * mm});
            skLineSegment(sketch, "E7.14.26.3", {"start": v(-66.5, 60.5) * mm, "end": v(-16.5, 60.5) * mm});
            skLineSegment(sketch, "E7.14.27.0", {"start": v(-16.5, 56.5) * mm, "end": v(-16.5, 6.5) * mm});
            skLineSegment(sketch, "E7.14.27.1", {"start": v(-66.5, 56.5) * mm, "end": v(-16.5, 56.5) * mm});
            skLineSegment(sketch, "E7.14.27.2", {"start": v(-66.5, 56.5) * mm, "end": v(-66.5, 6.5) * mm});
            skLineSegment(sketch, "E7.14.27.3", {"start": v(-66.5, 6.5) * mm, "end": v(-16.5, 6.5) * mm});
            skLineSegment(sketch, "E7.direction1", {"start": v(-772.5, 1464.5) * mm, "end": v(-718.5, 1464.5) * mm, "construction": true});
            skLineSegment(sketch, "E7.direction2", {"start": v(-772.5, 1464.5) * mm, "end": v(-772.5, 1410.5) * mm, "construction": true});
            skSolve(sketch);
        }
        {
            var Q0;
            Q0 = qSketchRegion(id + "F3", true);
            extrude(context, id + "F4", {"entities" : qUnion([Q0]), "depth" : 6 * mm, "offsetDistance" : 25 * mm});
        }
    });
